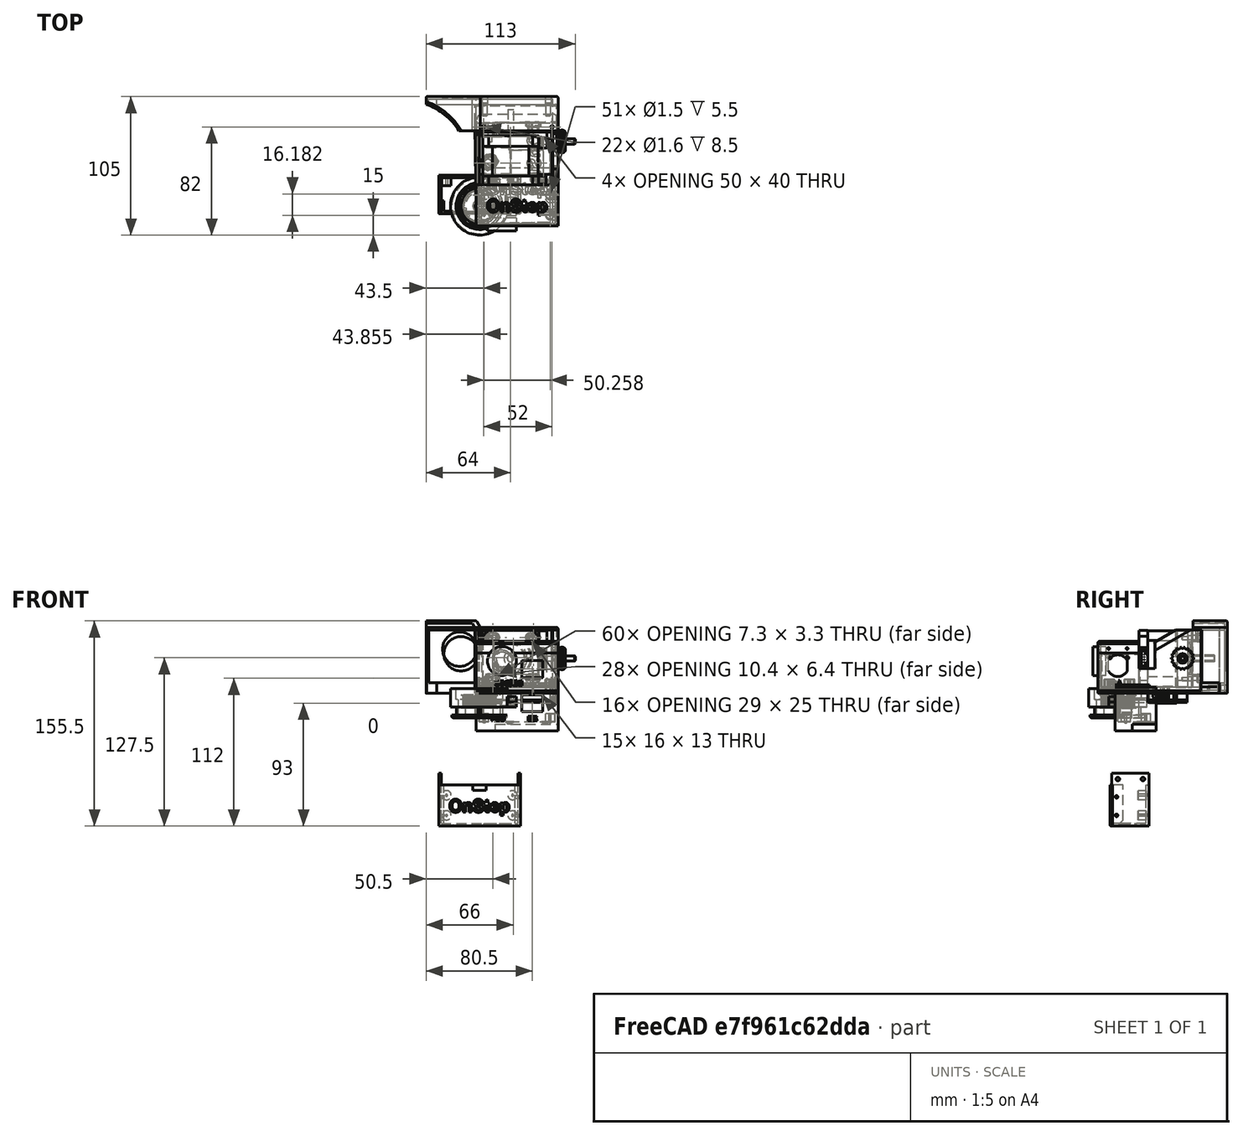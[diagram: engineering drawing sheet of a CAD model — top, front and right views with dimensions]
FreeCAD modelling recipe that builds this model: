
FCSTD DOCUMENT  (FreeCAD 0.20R29177 (Git))
Label: OnStep for EQ5
License: All rights reserved
LicenseURL: http://en.wikipedia.org/wiki/All_rights_reserved
objects: Part::Cylinder×304, Part::Box×205, Part::MultiFuse×163, Part::Cut×72, Part::Feature×53, Part::FeaturePython×28, Part::Part2DObjectPython×22, Part::Extrusion×22, Part::Fillet×14, App::Part×6, Mesh::Feature×4, Part::Chamfer×1
note: 884 computed .brp shape members not serialized (recipe doc carries the construction recipe); baked Part::Feature solids carry a one-line shape summary decoded from their .brp

FEATURE [Part::Part2DObjectPython] ShapeString016  # Draft 2D object (typed FeaturePython)
  FontFile = <path>
  Placement = pos=(15.3452,-2,30.5072) rot=(1,0,0;1.5708rad)
  Size = 0.01
  String = .
  Tracking = 0
FEATURE [Part::Part2DObjectPython] ShapeString013  # Draft 2D object (typed FeaturePython)
  FontFile = <path>
  Placement = pos=(15.3452,-2,30.5072) rot=(1,0,0;1.5708rad)
  Size = 10
  String = OnStep
  Tracking = 0
FEATURE [Part::Part2DObjectPython] ShapeString017  # Draft 2D object (typed FeaturePython)
  FontFile = <path>
  Placement = pos=(15.3452,-2,30.5072) rot=(1,0,0;1.5708rad)
  Size = 4
  String = DEC
  Tracking = 0
FEATURE [Part::Cylinder] Cylinder014005703  label="Válec620"
  Angle = 360
  AttacherType = Attacher::AttachEngine3D
  FirstAngle = 0
  Height = 70
  Placement = pos=(-5,6,16.5) rot=(0,1,0;1.5708rad)
  Radius = 1
  SecondAngle = 0
FEATURE [Part::Box] Box159  label="Krychle136"
  AttacherType = Attacher::AttachEngine3D
  Height = 2
  Length = 62
  Placement = pos=(-2.5,-2,23) rot=(0,0,1;0rad)
  Width = 31
FEATURE [Part::Box] Box161  label="Krychle138"
  AttacherType = Attacher::AttachEngine3D
  Height = 8
  Length = 58
  Placement = pos=(-0.5,0,15) rot=(0,0,1;0rad)
  Width = 29
FEATURE [Part::MultiFuse] Fusion001071
  Shapes = -> [Box159,Box161]
FEATURE [Part::Box] Box158  label="Krychle135"
  AttacherType = Attacher::AttachEngine3D
  Height = 4
  Length = 10
  Placement = pos=(-5,-8,-55) rot=(0,0,1;0rad)
  Width = 5
FEATURE [Part::Extrusion] Extrude071  label="OnStep005"
  Base = -> ShapeString013
  Dir = (0,-1,0)
  DirMode = 2
  FaceMakerClass = Part::FaceMakerBullseye
  LengthFwd = 1
  LengthRev = 0
  Placement = pos=(-10,-22,22) rot=(-1,0,0;1.5708rad)
  Solid = false
  Symmetric = false
FEATURE [Part::Cylinder] Cylinder014005704  label="Válec621"
  Angle = 360
  AttacherType = Attacher::AttachEngine3D
  FirstAngle = 0
  Height = 70
  Placement = pos=(-5,20,16.5) rot=(0,1,0;1.5708rad)
  Radius = 1
  SecondAngle = 0
FEATURE [Part::MultiFuse] Fusion001073  label="Horni diry009"
  Placement = pos=(0,0,3) rot=(0,0,1;0rad)
  Shapes = -> [Cylinder014005704,Cylinder014005703]
FEATURE [Part::Box] Box160  label="Krychle137"
  AttacherType = Attacher::AttachEngine3D
  Height = 8
  Length = 54
  Placement = pos=(1.5,0,15) rot=(0,0,1;0rad)
  Width = 29
FEATURE [Part::MultiFuse] Fusion001072
  Shapes = -> [Fusion001073,Box160]
FEATURE [Part::Cut] Cut061098066
  Base = -> Fusion001071
  Tool = -> Fusion001072
FEATURE [Part::Cut] Cut061098067  label="viko s texty005"
  Base = -> Cut061098066
  Tool = -> Extrude071
FEATURE [Part::Chamfer] Chamfer008017
  Base = -> Cut061098067
  Edges = 2 edges r=2.5: [Edge355,Edge357]
FEATURE [Part::Fillet] Fillet009  label="DEC vicko003"
  Base = -> Chamfer008017
  Edges = 3 edges r=1: [Edge36,Edge38,Edge39]
  Placement = pos=(-28.5,19,-80) rot=(1,0,0;1.5708rad)
FEATURE [Part::Cut] Cut061098065  label="DEC PCB Cap"
  Base = -> Fillet009
  Tool = -> Box158
FEATURE [Part::Extrusion] Extrude086  label="Text RA002"
  Base = -> ShapeString017
  Dir = (0,-1,0)
  DirMode = 2
  FaceMakerClass = Part::FaceMakerBullseye
  LengthFwd = 1
  LengthRev = 0
  Placement = pos=(18,0.5,-33) rot=(0,0,1;0rad)
  Solid = false
  Symmetric = false
FEATURE [Part::Cylinder] Cylinder014005791  label="Válec704"
  Angle = 360
  AttacherType = Attacher::AttachEngine3D
  FirstAngle = 0
  Height = 70
  Placement = pos=(-5,6,16.5) rot=(0,1,0;1.5708rad)
  Radius = 1
  SecondAngle = 0
FEATURE [Part::Cylinder] Cylinder014005799  label="Válec712"
  Angle = 360
  AttacherType = Attacher::AttachEngine3D
  FirstAngle = 0
  Height = 70
  Placement = pos=(-5,20,16.5) rot=(0,1,0;1.5708rad)
  Radius = 1
  SecondAngle = 0
FEATURE [Part::Cylinder] Cylinder014005792  label="Válec705"
  Angle = 360
  AttacherType = Attacher::AttachEngine3D
  FirstAngle = 0
  Height = 8
  Placement = pos=(53.5,21.25,0) rot=(0,0,1;0rad)
  Radius = 0.75
  SecondAngle = 0
FEATURE [Part::Cylinder] Cylinder014005795  label="Válec708"
  Angle = 360
  AttacherType = Attacher::AttachEngine3D
  FirstAngle = 0
  Height = 6.5
  Placement = pos=(53.5,6,0) rot=(0,0,1;0rad)
  Radius = 3.5
  SecondAngle = 0
FEATURE [Part::Box] Box203  label="Krychle178"
  AttacherType = Attacher::AttachEngine3D
  Height = 13
  Length = 2
  Placement = pos=(-31,-4.5,-55) rot=(0,0,1;0rad)
  Width = 28
FEATURE [Part::Cylinder] Cylinder014005796  label="Válec709"
  Angle = 360
  AttacherType = Attacher::AttachEngine3D
  FirstAngle = 0
  Height = 8
  Placement = pos=(53.5,6,0) rot=(0,0,1;0rad)
  Radius = 0.75
  SecondAngle = 0
FEATURE [Part::Box] Box202  label="Krychle177"
  AttacherType = Attacher::AttachEngine3D
  Height = 13
  Length = 2
  Placement = pos=(29,-4.5,-55) rot=(0,0,1;0rad)
  Width = 28
FEATURE [Part::Box] Box201  label="RJ056"
  AttacherType = Attacher::AttachEngine3D
  Height = 13
  Length = 16
  Placement = pos=(32,-5,4.5) rot=(0,0,1;0rad)
  Width = 18.5
FEATURE [Part::Cylinder] Cylinder014005793  label="Válec706"
  Angle = 360
  AttacherType = Attacher::AttachEngine3D
  FirstAngle = 0
  Height = 6.5
  Placement = pos=(3.5,21.25,0) rot=(0,0,1;0rad)
  Radius = 3.5
  SecondAngle = 0
FEATURE [Part::Cylinder] Cylinder014005802  label="Válec715"
  Angle = 360
  AttacherType = Attacher::AttachEngine3D
  FirstAngle = 0
  Height = 74
  Placement = pos=(-40,19,-46.5) rot=(0,1,0;1.5708rad)
  Radius = 1.4
  SecondAngle = 0
FEATURE [Part::Box] Box204  label="Krychle179"
  AttacherType = Attacher::AttachEngine3D
  Height = 28
  Length = 62
  Placement = pos=(-2.5,-2,-5) rot=(0,0,1;0rad)
  Width = 31
FEATURE [Part::Box] Box200  label="Krychle176"
  AttacherType = Attacher::AttachEngine3D
  Height = 26
  Length = 58
  Placement = pos=(-0.5,0,-3) rot=(0,0,1;0rad)
  Width = 29
FEATURE [Part::Cut] Cut061098120  label="Základ002"
  Base = -> Box204
  Tool = -> Box200
FEATURE [Part::Extrusion] Extrude087  label="Text TR002"
  Base = -> ShapeString016
  Dir = (0,-1,0)
  DirMode = 2
  FaceMakerClass = Part::FaceMakerBullseye
  LengthFwd = 1
  LengthRev = 0
  Placement = pos=(-6.75,0.5,-33) rot=(0,0,1;0rad)
  Solid = false
  Symmetric = false
FEATURE [Part::Cylinder] Cylinder014005800  label="Válec713"
  Angle = 360
  AttacherType = Attacher::AttachEngine3D
  FirstAngle = 0
  Height = 8
  Placement = pos=(3.5,21.25,0) rot=(0,0,1;0rad)
  Radius = 0.75
  SecondAngle = 0
FEATURE [Part::Cylinder] Cylinder014005801  label="Válec714"
  Angle = 360
  AttacherType = Attacher::AttachEngine3D
  FirstAngle = 0
  Height = 5
  Placement = pos=(14.25,1,9.5) rot=(1,0,0;1.5708rad)
  Radius = 0.01
  SecondAngle = 0
FEATURE [Part::Cylinder] Cylinder014005803  label="Válec716"
  Angle = 360
  AttacherType = Attacher::AttachEngine3D
  FirstAngle = 0
  Height = 74
  Placement = pos=(-40,0,-46.5) rot=(0,1,0;1.5708rad)
  Radius = 1.4
  SecondAngle = 0
FEATURE [Part::Cylinder] Cylinder014005797  label="Válec710"
  Angle = 360
  AttacherType = Attacher::AttachEngine3D
  FirstAngle = 0
  Height = 6.5
  Placement = pos=(53.5,21.25,0) rot=(0,0,1;0rad)
  Radius = 3.5
  SecondAngle = 0
FEATURE [Part::Cylinder] Cylinder014005798  label="Válec711"
  Angle = 360
  AttacherType = Attacher::AttachEngine3D
  FirstAngle = 0
  Height = 8
  Placement = pos=(3.5,6,0) rot=(0,0,1;0rad)
  Radius = 0.7
  SecondAngle = 0
FEATURE [Part::Cylinder] Cylinder014005794  label="Válec707"
  Angle = 360
  AttacherType = Attacher::AttachEngine3D
  FirstAngle = 0
  Height = 6.5
  Placement = pos=(3.5,6,0) rot=(0,0,1;0rad)
  Radius = 3.5
  SecondAngle = 0
FEATURE [Part::MultiFuse] Fusion001089071  label="Horni diry011"
  Placement = pos=(0,0,3) rot=(0,0,1;0rad)
  Shapes = -> [Cylinder014005799,Cylinder014005791]
FEATURE [Part::MultiFuse] Fusion001089075
  Shapes = -> [Extrude087,Extrude086]
FEATURE [Part::MultiFuse] Fusion001089077
  Shapes = -> [Box202,Box203]
FEATURE [Part::MultiFuse] Fusion001089068  label="diry017"
  Placement = pos=(0,0,-4) rot=(0,0,1;0rad)
  Shapes = -> [Cylinder014005800,Cylinder014005798,Cylinder014005792,Cylinder014005796]
FEATURE [Part::MultiFuse] Fusion001089070  label="RJ a LED002"
  Shapes = -> [Box201,Cylinder014005801]
FEATURE [Part::MultiFuse] Fusion001089072  label="sloupky005"
  Placement = pos=(0,0,-3.5) rot=(0,0,1;0rad)
  Shapes = -> [Cylinder014005793,Cylinder014005794,Cylinder014005797,Cylinder014005795]
FEATURE [Part::MultiFuse] Fusion001089073
  Shapes = -> [Cylinder014005803,Cylinder014005802]
FEATURE [Part::MultiFuse] Fusion001089074  label="bez der002"
  Shapes = -> [Cut061098120,Fusion001089072]
FEATURE [Part::MultiFuse] Fusion001089069
  Shapes = -> [Fusion001089068,Fusion001089070,Fusion001089071]
FEATURE [Part::Cut] Cut061098121
  Base = -> Fusion001089074
  Tool = -> Fusion001089069
FEATURE [Part::Cut] Cut061098118
  Base = -> Cut061098121
  Placement = pos=(-28.5,18.5,-80) rot=(1,0,0;1.5708rad)
  Tool = -> Fusion001089075
FEATURE [Part::MultiFuse] Fusion001089076  label="RA pcb box002"
  Shapes = -> [Cut061098118,Fusion001089077]
FEATURE [Part::Cut] Cut061098119  label="DEC PCB BOX For MiniPCB2"
  Base = -> Fusion001089076
  Tool = -> Fusion001089073
FEATURE [Part::Feature] Cut061098127012  label="DE 012"
  shape: bbox 62 x 31 x 33 mm, 80 faces (baked)
FEATURE [Part::Fillet] Fillet004005002  label="DE final"
  Base = -> Cut061098127012
  Edges = 5 edges r=1: [Edge94,Edge95,Edge96,Edge97,Edge98]
FEATURE [Part::Feature] Cut005023015002001  label="RA PCB003"
  shape: bbox 62 x 31 x 33 mm, 145 faces (baked)
FEATURE [App::Part] Part
  Group = -> [Fusion001089075,Fusion001089068,Fusion001089076,Fusion001089077,Fusion001089070,Fusion001089074,Fusion001089069,Fusion001089071,Fusion001089072,Fusion001089073,Cut061098118,Cut061098121,Cut061098120,Cylinder014005802,Box201,Cylinder014005803,Cylinder014005799,Cylinder014005795,Box202,Cylinder014005793,Box203,Extrude086,Cylinder014005791,Box200,Cylinder014005800,Cylinder014005797,Cylinder014005794,+28 more]
  Origin = -> Origin
FEATURE [Mesh::Feature] support_nema17_EQ5_A_D__v1_1  label="support_nema17_EQ5_A.D._v1.1"
FEATURE [Mesh::Feature] support_nema17_EQ5_Dec_v1_1  label="support_nema17_EQ5_Dec_v1.1"
  Placement = pos=(-2,-2,13) rot=(0,0,1;0rad)
FEATURE [Mesh::Feature] holderDEC
  Placement = pos=(0,0,6) rot=(0,0,1;0rad)
FEATURE [Mesh::Feature] holderRA
FEATURE [Part::Feature] Pocket004
  Placement = pos=(22.5,32.5,13.5) rot=(0,0,1;1.5708rad)
  shape: bbox 61 x 74.5 x 11 mm, 39 faces (baked)
FEATURE [Part::Box] Box  label="Krychle"
  AttacherType = Attacher::AttachEngine3D
  Height = 43
  Length = 59.5
  Placement = pos=(0,56,23) rot=(0,0,1;0rad)
  Width = 7
FEATURE [Part::Box] Box205  label="Krychle180"
  AttacherType = Attacher::AttachEngine3D
  Height = 43
  Length = 43
  Placement = pos=(2,53,23) rot=(0,0,1;0rad)
  Width = 3
FEATURE [Part::Cylinder] Cylinder014005804  label="Válec717"
  Angle = 360
  AttacherType = Attacher::AttachEngine3D
  FirstAngle = 0
  Height = 10
  Placement = pos=(8,57,29.5) rot=(1,0,0;1.5708rad)
  Radius = 1.65
  SecondAngle = 0
FEATURE [Part::Cylinder] Cylinder014005805  label="Válec718"
  Angle = 360
  AttacherType = Attacher::AttachEngine3D
  FirstAngle = 0
  Height = 10
  Placement = pos=(39,57,60.5) rot=(1,0,0;1.5708rad)
  Radius = 1.65
  SecondAngle = 0
FEATURE [Part::Cylinder] Cylinder014005806  label="Válec719"
  Angle = 360
  AttacherType = Attacher::AttachEngine3D
  FirstAngle = 0
  Height = 10
  Placement = pos=(39,57,29.5) rot=(1,0,0;1.5708rad)
  Radius = 1.65
  SecondAngle = 0
FEATURE [Part::Cylinder] Cylinder014005807  label="Válec720"
  Angle = 360
  AttacherType = Attacher::AttachEngine3D
  FirstAngle = 0
  Height = 10
  Placement = pos=(8,57,60.5) rot=(1,0,0;1.5708rad)
  Radius = 1.65
  SecondAngle = 0
FEATURE [Part::Cylinder] Cylinder014005808  label="Válec721"
  Angle = 360
  AttacherType = Attacher::AttachEngine3D
  FirstAngle = 0
  Height = 10
  Placement = pos=(23.5,59,45) rot=(1,0,0;1.5708rad)
  Radius = 12.5
  SecondAngle = 0
FEATURE [Part::Box] Box206  label="Krychle181"
  AttacherType = Attacher::AttachEngine3D
  Height = 43
  Length = 6
  Placement = pos=(45,44,23) rot=(0,0,1;0rad)
  Width = 12
FEATURE [Part::FeaturePython] Screw010  label="M4x25-Screw001"  # Fasteners workbench fastener (typed FeaturePython)
  Placement = pos=(47.5,49,45) rot=(0,-1,0;1.5708rad)
  diameter = 6
  invert = false
  length = 0
  matchOuter = false
  offset = 0
  thread = false
  type = 13
FEATURE [Part::MultiFuse] Fusion  label="diry jezdec"
  Shapes = -> [Cylinder014005804,Cylinder014005808,Cylinder014005807,Cylinder014005806,Cylinder014005805,Screw010]
FEATURE [Part::MultiFuse] Fusion001089078
  Shapes = -> [Box205,Box206]
FEATURE [Part::Cut] Cut  label="Jezdec"
  Base = -> Fusion001089078
  Tool = -> Fusion
FEATURE [Part::Cylinder] Cylinder014005809  label="Válec722"
  Angle = 360
  AttacherType = Attacher::AttachEngine3D
  FirstAngle = 0
  Height = 20
  Placement = pos=(23.5,64,45) rot=(1,0,0;1.5708rad)
  Radius = 12.5
  SecondAngle = 0
FEATURE [Part::Cylinder] Cylinder014005810  label="Válec723"
  Angle = 360
  AttacherType = Attacher::AttachEngine3D
  FirstAngle = 0
  Height = 10
  Placement = pos=(8,64,29.5) rot=(1,0,0;1.5708rad)
  Radius = 1.65
  SecondAngle = 0
FEATURE [Part::Cylinder] Cylinder014005811  label="Válec724"
  Angle = 360
  AttacherType = Attacher::AttachEngine3D
  FirstAngle = 0
  Height = 10
  Placement = pos=(8,64,60.5) rot=(1,0,0;1.5708rad)
  Radius = 1.65
  SecondAngle = 0
FEATURE [Part::Cylinder] Cylinder014005812  label="Válec725"
  Angle = 360
  AttacherType = Attacher::AttachEngine3D
  FirstAngle = 0
  Height = 10
  Placement = pos=(39,64,29.5) rot=(1,0,0;1.5708rad)
  Radius = 1.65
  SecondAngle = 0
FEATURE [Part::Cylinder] Cylinder014005813  label="Válec726"
  Angle = 360
  AttacherType = Attacher::AttachEngine3D
  FirstAngle = 0
  Height = 10
  Placement = pos=(39,64,60.5) rot=(1,0,0;1.5708rad)
  Radius = 1.65
  SecondAngle = 0
FEATURE [Part::FeaturePython] Screw011  label="M4x25-Screw002"  # Fasteners workbench fastener (typed FeaturePython)
  Placement = pos=(47.5,49,45) rot=(0,-1,0;1.5708rad)
  diameter = 6
  invert = false
  length = 0
  matchOuter = false
  offset = 0
  thread = false
  type = 13
FEATURE [Part::Box] Box207  label="Krychle182"
  AttacherType = Attacher::AttachEngine3D
  Height = 43
  Length = 4
  Placement = pos=(55.5,16,23) rot=(0,0,1;0rad)
  Width = 40
FEATURE [Part::Cylinder] Cylinder014005814  label="Válec727"
  Angle = 360
  AttacherType = Attacher::AttachEngine3D
  FirstAngle = 0
  Height = 10
  Placement = pos=(8,64,29.5) rot=(1,0,0;1.5708rad)
  Radius = 1.65
  SecondAngle = 0
FEATURE [Part::Cylinder] Cylinder014005815  label="Válec728"
  Angle = 360
  AttacherType = Attacher::AttachEngine3D
  FirstAngle = 0
  Height = 20
  Placement = pos=(23.5,64,45) rot=(1,0,0;1.5708rad)
  Radius = 12.5
  SecondAngle = 0
FEATURE [Part::Cylinder] Cylinder014005816  label="Válec729"
  Angle = 360
  AttacherType = Attacher::AttachEngine3D
  FirstAngle = 0
  Height = 10
  Placement = pos=(8,64,60.5) rot=(1,0,0;1.5708rad)
  Radius = 1.65
  SecondAngle = 0
FEATURE [Part::Cylinder] Cylinder014005817  label="Válec730"
  Angle = 360
  AttacherType = Attacher::AttachEngine3D
  FirstAngle = 0
  Height = 10
  Placement = pos=(39,64,29.5) rot=(1,0,0;1.5708rad)
  Radius = 1.65
  SecondAngle = 0
FEATURE [Part::Cylinder] Cylinder014005818  label="Válec731"
  Angle = 360
  AttacherType = Attacher::AttachEngine3D
  FirstAngle = 0
  Height = 10
  Placement = pos=(39,64,60.5) rot=(1,0,0;1.5708rad)
  Radius = 1.65
  SecondAngle = 0
FEATURE [Part::MultiFuse] Fusion001089080
  Placement = pos=(4,0,0) rot=(0,0,1;0rad)
  Shapes = -> [Cylinder014005814,Cylinder014005816,Cylinder014005818,Cylinder014005815,Cylinder014005817]
FEATURE [Part::Box] Box208  label="Krychle183"
  AttacherType = Attacher::AttachEngine3D
  Height = 25
  Length = 4
  Placement = pos=(23.5,56,32.5) rot=(0,0,1;0rad)
  Width = 8
FEATURE [Part::Box] Box209  label="Krychle184"
  AttacherType = Attacher::AttachEngine3D
  Height = 3.3
  Length = 4
  Placement = pos=(8,56,27.85) rot=(0,0,1;0rad)
  Width = 8
FEATURE [Part::Box] Box210  label="Krychle185"
  AttacherType = Attacher::AttachEngine3D
  Height = 3.3
  Length = 4
  Placement = pos=(39,56,58.85) rot=(0,0,1;0rad)
  Width = 8
FEATURE [Part::Box] Box211  label="Krychle186"
  AttacherType = Attacher::AttachEngine3D
  Height = 3.3
  Length = 4
  Placement = pos=(39,56,27.85) rot=(0,0,1;0rad)
  Width = 8
FEATURE [Part::Box] Box212  label="Krychle187"
  AttacherType = Attacher::AttachEngine3D
  Height = 3.3
  Length = 4
  Placement = pos=(8,56,58.85) rot=(0,0,1;0rad)
  Width = 8
FEATURE [Part::MultiFuse] Fusion001089081  label="Main"
  Placement = pos=(0,0,0.5) rot=(0,0,1;0rad)
  Shapes = -> [Box,Box207]
FEATURE [Part::Box] Box213  label="konektor"
  AttacherType = Attacher::AttachEngine3D
  Height = 29
  Length = 10
  Placement = pos=(50,16,37) rot=(0,0,1;0rad)
  Width = 12
FEATURE [Part::Box] Box214  label="Krychle188"
  AttacherType = Attacher::AttachEngine3D
  Height = 43
  Length = 4
  Placement = pos=(55.5,22,47) rot=(1,0,0;0.523599rad)
  Width = 40
FEATURE [Part::MultiFuse] Fusion001089079  label="diry"
  Placement = pos=(0,0,0.5) rot=(0,0,1;0rad)
  Shapes = -> [Cylinder014005810,Cylinder014005809,Cylinder014005811,Cylinder014005812,Cylinder014005813,Screw011,Fusion001089080,Box208,Box209,Box210,Box211,Box212,Box213,Box214]
FEATURE [Part::Cut] Cut005023015002002  label="RA"
  Base = -> Fusion001089081
  Tool = -> Fusion001089079
FEATURE [Part::Part2DObjectPython] ShapeString015  # Draft 2D object (typed FeaturePython)
  FontFile = <path>
  Placement = pos=(15.3452,-2,30.5072) rot=(1,0,0;1.5708rad)
  Size = 0.01
  String = .
  Tracking = 0
FEATURE [Part::Part2DObjectPython] ShapeString014  # Draft 2D object (typed FeaturePython)
  FontFile = <path>
  Placement = pos=(15.3452,-2,30.5072) rot=(1,0,0;1.5708rad)
  Size = 4
  String = RA
  Tracking = 0
FEATURE [Part::Cylinder] Cylinder014005783  label="Válec696"
  Angle = 360
  AttacherType = Attacher::AttachEngine3D
  FirstAngle = 0
  Height = 70
  Placement = pos=(-5,20,16.5) rot=(0,1,0;1.5708rad)
  Radius = 1
  SecondAngle = 0
FEATURE [Part::Extrusion] Extrude084  label="Text RA001"
  Base = -> ShapeString014
  Dir = (0,-1,0)
  DirMode = 2
  FaceMakerClass = Part::FaceMakerBullseye
  LengthFwd = 1
  LengthRev = 0
  Placement = pos=(4,0.7,-23.5) rot=(0,0,1;0rad)
  Solid = false
  Symmetric = false
FEATURE [Part::Cylinder] Cylinder014005778  label="Válec691"
  Angle = 360
  AttacherType = Attacher::AttachEngine3D
  FirstAngle = 0
  Height = 8
  Placement = pos=(3.5,6,0) rot=(0,0,1;0rad)
  Radius = 0.7
  SecondAngle = 0
FEATURE [Part::Cylinder] Cylinder014005779  label="Válec692"
  Angle = 360
  AttacherType = Attacher::AttachEngine3D
  FirstAngle = 0
  Height = 8
  Placement = pos=(53.5,21.25,0) rot=(0,0,1;0rad)
  Radius = 0.75
  SecondAngle = 0
FEATURE [Part::Cylinder] Cylinder014005780  label="Válec693"
  Angle = 360
  AttacherType = Attacher::AttachEngine3D
  FirstAngle = 0
  Height = 6.5
  Placement = pos=(3.5,6,0) rot=(0,0,1;0rad)
  Radius = 3.5
  SecondAngle = 0
FEATURE [Part::Box] Box195  label="Krychle172"
  AttacherType = Attacher::AttachEngine3D
  Height = 26
  Length = 58
  Placement = pos=(-0.5,0,-3) rot=(0,0,1;0rad)
  Width = 29
FEATURE [Part::Cylinder] Cylinder014005781  label="Válec694"
  Angle = 360
  AttacherType = Attacher::AttachEngine3D
  FirstAngle = 0
  Height = 6.5
  Placement = pos=(53.5,21.25,0) rot=(0,0,1;0rad)
  Radius = 3.5
  SecondAngle = 0
FEATURE [Part::Cylinder] Cylinder014005782  label="Válec695"
  Angle = 360
  AttacherType = Attacher::AttachEngine3D
  FirstAngle = 0
  Height = 8
  Placement = pos=(53.5,6,0) rot=(0,0,1;0rad)
  Radius = 0.75
  SecondAngle = 0
FEATURE [Part::Cylinder] Cylinder014005784  label="Válec697"
  Angle = 360
  AttacherType = Attacher::AttachEngine3D
  FirstAngle = 0
  Height = 70
  Placement = pos=(-5,6,16.5) rot=(0,1,0;1.5708rad)
  Radius = 1
  SecondAngle = 0
FEATURE [Part::Box] Box196  label="RJ055"
  AttacherType = Attacher::AttachEngine3D
  Height = 13
  Length = 16
  Placement = pos=(32,-5,4.5) rot=(0,0,1;0rad)
  Width = 18.5
FEATURE [Part::Cylinder] Cylinder014005786  label="Válec699"
  Angle = 360
  AttacherType = Attacher::AttachEngine3D
  FirstAngle = 0
  Height = 8
  Placement = pos=(3.5,21.25,0) rot=(0,0,1;0rad)
  Radius = 0.75
  SecondAngle = 0
FEATURE [Part::Cylinder] Cylinder014005787  label="Válec700"
  Angle = 360
  AttacherType = Attacher::AttachEngine3D
  FirstAngle = 0
  Height = 6.5
  Placement = pos=(3.5,21.25,0) rot=(0,0,1;0rad)
  Radius = 3.5
  SecondAngle = 0
FEATURE [Part::Cylinder] Cylinder014005785  label="Válec698"
  Angle = 360
  AttacherType = Attacher::AttachEngine3D
  FirstAngle = 0
  Height = 5
  Placement = pos=(14.25,1,9.5) rot=(1,0,0;1.5708rad)
  Radius = 0.01
  SecondAngle = 0
FEATURE [Part::Cylinder] Cylinder014005788  label="Válec701"
  Angle = 360
  AttacherType = Attacher::AttachEngine3D
  FirstAngle = 0
  Height = 6.5
  Placement = pos=(53.5,6,0) rot=(0,0,1;0rad)
  Radius = 3.5
  SecondAngle = 0
FEATURE [Part::Box] Box199  label="Krychle175"
  AttacherType = Attacher::AttachEngine3D
  Height = 28
  Length = 62
  Placement = pos=(-2.5,-2,-5) rot=(0,0,1;0rad)
  Width = 31
FEATURE [Part::Cut] Cut061098114  label="Základ001"
  Base = -> Box199
  Tool = -> Box195
FEATURE [Part::Extrusion] Extrude085  label="Text TR001"
  Base = -> ShapeString015
  Dir = (0,-1,0)
  DirMode = 2
  FaceMakerClass = Part::FaceMakerBullseye
  LengthFwd = 1
  LengthRev = 0
  Placement = pos=(-6.75,1,-33) rot=(0,0,1;0rad)
  Solid = false
  Symmetric = false
FEATURE [Part::MultiFuse] Fusion001089063
  Shapes = -> [Extrude085,Extrude084]
FEATURE [Part::MultiFuse] Fusion001089058  label="RJ a LED001"
  Shapes = -> [Box196,Cylinder014005785]
FEATURE [Part::MultiFuse] Fusion001089059  label="Horni diry010"
  Placement = pos=(0,0,3) rot=(0,0,1;0rad)
  Shapes = -> [Cylinder014005783,Cylinder014005784]
FEATURE [Part::MultiFuse] Fusion001089060  label="diry016"
  Placement = pos=(0,0,-4) rot=(0,0,1;0rad)
  Shapes = -> [Cylinder014005786,Cylinder014005778,Cylinder014005779,Cylinder014005782]
FEATURE [Part::MultiFuse] Fusion001089062
  Shapes = -> [Fusion001089060,Fusion001089058,Fusion001089059]
FEATURE [Part::MultiFuse] Fusion001089061  label="sloupky004"
  Placement = pos=(0,0,-3.5) rot=(0,0,1;0rad)
  Shapes = -> [Cylinder014005787,Cylinder014005780,Cylinder014005781,Cylinder014005788]
FEATURE [Part::MultiFuse] Fusion001089067  label="bez der001"
  Shapes = -> [Cut061098114,Fusion001089061]
FEATURE [Part::Cut] Cut061098117
  Base = -> Fusion001089067
  Tool = -> Fusion001089062
FEATURE [Part::Cut] Cut061098115  label="PCB"
  Base = -> Cut061098117
  Placement = pos=(0,-13,26) rot=(1,0,0;0rad)
  Tool = -> Fusion001089063
FEATURE [Part::Box] Box215  label="Krychle189"
  AttacherType = Attacher::AttachEngine3D
  Height = 3
  Length = 62
  Placement = pos=(-2.5,-15,20.5) rot=(0,0,1;0rad)
  Width = 78
FEATURE [Part::Box] Box216  label="Krychle190"
  AttacherType = Attacher::AttachEngine3D
  Height = 8
  Length = 24
  Placement = pos=(-1.5,12.5,13.5) rot=(0,0,1;0rad)
  Width = 40
FEATURE [Part::Box] Box217  label="Krychle191"
  AttacherType = Attacher::AttachEngine3D
  Height = 8
  Length = 26
  Placement = pos=(22.5,22.5,13.5) rot=(0,0,1;0rad)
  Width = 20
FEATURE [Part::Box] Box218  label="Krychle192"
  AttacherType = Attacher::AttachEngine3D
  Height = 8
  Length = 6
  Placement = pos=(53.5,22.5,13.5) rot=(0,0,1;0rad)
  Width = 20
FEATURE [Part::MultiFuse] Fusion001089082  label="spodek"
  Shapes = -> [Box215,Box218,Box216,Box217]
FEATURE [Part::FeaturePython] Screw  label="M6x12-Screw"  # Fasteners workbench fastener (typed FeaturePython)
  Placement = pos=(6.5,32.5,19.5) rot=(1,0,0;0rad)
  diameter = 8
  invert = false
  length = 0
  matchOuter = false
  offset = 0
  thread = false
  type = 14
FEATURE [Part::Cylinder] Cylinder  label="Válec"
  Angle = 360
  AttacherType = Attacher::AttachEngine3D
  FirstAngle = 0
  Height = 10
  Placement = pos=(52,28,16.5) rot=(0,1,0;1.5708rad)
  Radius = 1.65
  SecondAngle = 0
FEATURE [Part::Cylinder] Cylinder014005819  label="Válec732"
  Angle = 360
  AttacherType = Attacher::AttachEngine3D
  FirstAngle = 0
  Height = 10
  Placement = pos=(52,37,16.5) rot=(0,1,0;1.5708rad)
  Radius = 1.65
  SecondAngle = 0
FEATURE [Part::Box] Box219  label="Krychle193"
  AttacherType = Attacher::AttachEngine3D
  Height = 3.3
  Length = 10
  Placement = pos=(52,28,14.85) rot=(0,0,1;0rad)
  Width = 9
FEATURE [Part::MultiFuse] Fusion001089083  label="Diryspodek"
  Shapes = -> [Box219,Cylinder,Cylinder014005819,Screw]
FEATURE [Part::Cut] Cut005023015002003  label="Spodek"
  Base = -> Fusion001089082
  Tool = -> Fusion001089083
FEATURE [Part::MultiFuse] Fusion001089084
  Shapes = -> [Cut061098115,Cut005023015002003,Cut005023015002002]
FEATURE [Part::FeaturePython] Screw012  label="M4x25-Screw003"  # Fasteners workbench fastener (typed FeaturePython)
  Placement = pos=(47.5,49,45) rot=(0,-1,0;1.5708rad)
  diameter = 6
  invert = false
  length = 0
  matchOuter = false
  offset = 0
  thread = false
  type = 13
FEATURE [Part::FeaturePython] Screw013  label="M6x12-Screw001"  # Fasteners workbench fastener (typed FeaturePython)
  Placement = pos=(8.5,34,19.5) rot=(1,0,0;0rad)
  diameter = 8
  invert = false
  length = 0
  matchOuter = false
  offset = 0
  thread = false
  type = 14
FEATURE [Part::Cylinder] Cylinder014005820  label="Válec733"
  Angle = 360
  AttacherType = Attacher::AttachEngine3D
  FirstAngle = 0
  Height = 10
  Placement = pos=(8,64,60.5) rot=(1,0,0;1.5708rad)
  Radius = 1.65
  SecondAngle = 0
FEATURE [Part::Cylinder] Cylinder014005821  label="Válec734"
  Angle = 360
  AttacherType = Attacher::AttachEngine3D
  FirstAngle = 0
  Height = 10
  Placement = pos=(39,64,29.5) rot=(1,0,0;1.5708rad)
  Radius = 1.65
  SecondAngle = 0
FEATURE [Part::Cylinder] Cylinder014005822  label="Válec735"
  Angle = 360
  AttacherType = Attacher::AttachEngine3D
  FirstAngle = 0
  Height = 10
  Placement = pos=(8,64,60.5) rot=(1,0,0;1.5708rad)
  Radius = 1.65
  SecondAngle = 0
FEATURE [Part::Cylinder] Cylinder014005823  label="Válec736"
  Angle = 360
  AttacherType = Attacher::AttachEngine3D
  FirstAngle = 0
  Height = 10
  Placement = pos=(8,64,29.5) rot=(1,0,0;1.5708rad)
  Radius = 1.65
  SecondAngle = 0
FEATURE [Part::Cylinder] Cylinder014005824  label="Válec737"
  Angle = 360
  AttacherType = Attacher::AttachEngine3D
  FirstAngle = 0
  Height = 10
  Placement = pos=(39,64,29.5) rot=(1,0,0;1.5708rad)
  Radius = 1.65
  SecondAngle = 0
FEATURE [Part::Box] Box220  label="Krychle194"
  AttacherType = Attacher::AttachEngine3D
  Height = 43
  Length = 59.5
  Placement = pos=(0,56,23) rot=(0,0,1;0rad)
  Width = 7
FEATURE [Part::Box] Box221  label="Krychle195"
  AttacherType = Attacher::AttachEngine3D
  Height = 43
  Length = 4
  Placement = pos=(55.5,16,23) rot=(0,0,1;0rad)
  Width = 40
FEATURE [Part::Cylinder] Cylinder014005825  label="Válec738"
  Angle = 360
  AttacherType = Attacher::AttachEngine3D
  FirstAngle = 0
  Height = 20
  Placement = pos=(23.5,64,45) rot=(1,0,0;1.5708rad)
  Radius = 12.5
  SecondAngle = 0
FEATURE [Part::Cylinder] Cylinder014005826  label="Válec739"
  Angle = 360
  AttacherType = Attacher::AttachEngine3D
  FirstAngle = 0
  Height = 10
  Placement = pos=(39,64,60.5) rot=(1,0,0;1.5708rad)
  Radius = 1.65
  SecondAngle = 0
FEATURE [Part::Cylinder] Cylinder014005827  label="Válec740"
  Angle = 360
  AttacherType = Attacher::AttachEngine3D
  FirstAngle = 0
  Height = 10
  Placement = pos=(8,64,29.5) rot=(1,0,0;1.5708rad)
  Radius = 1.65
  SecondAngle = 0
FEATURE [Part::Cylinder] Cylinder014005828  label="Válec741"
  Angle = 360
  AttacherType = Attacher::AttachEngine3D
  FirstAngle = 0
  Height = 20
  Placement = pos=(23.5,64,45) rot=(1,0,0;1.5708rad)
  Radius = 12.5
  SecondAngle = 0
FEATURE [Part::MultiFuse] Fusion001089085  label="Main001"
  Placement = pos=(0,0,0.5) rot=(0,0,1;0rad)
  Shapes = -> [Box220,Box221]
FEATURE [Part::Cylinder] Cylinder014005829  label="Válec742"
  Angle = 360
  AttacherType = Attacher::AttachEngine3D
  FirstAngle = 0
  Height = 10
  Placement = pos=(39,64,60.5) rot=(1,0,0;1.5708rad)
  Radius = 1.65
  SecondAngle = 0
FEATURE [Part::MultiFuse] Fusion001089090
  Placement = pos=(4,0,0) rot=(0,0,1;0rad)
  Shapes = -> [Cylinder014005827,Cylinder014005820,Cylinder014005829,Cylinder014005828,Cylinder014005821]
FEATURE [Part::Box] Box224  label="Krychle198"
  AttacherType = Attacher::AttachEngine3D
  Height = 9
  Length = 26
  Placement = pos=(-2,24,13) rot=(0,0,1;0rad)
  Width = 20
FEATURE [Part::Box] Box225  label="Krychle199"
  AttacherType = Attacher::AttachEngine3D
  Height = 25
  Length = 4
  Placement = pos=(23.5,56,32.5) rot=(0,0,1;0rad)
  Width = 8
FEATURE [Part::Box] Box226  label="Krychle200"
  AttacherType = Attacher::AttachEngine3D
  Height = 3.3
  Length = 4
  Placement = pos=(39,56,58.85) rot=(0,0,1;0rad)
  Width = 8
FEATURE [Part::Box] Box227  label="Krychle201"
  AttacherType = Attacher::AttachEngine3D
  Height = 43
  Length = 4
  Placement = pos=(55.5,22,47) rot=(1,0,0;0.523599rad)
  Width = 40
FEATURE [Part::Box] Box228  label="konektor001"
  AttacherType = Attacher::AttachEngine3D
  Height = 29
  Length = 10
  Placement = pos=(50,16,37) rot=(0,0,1;0rad)
  Width = 12
FEATURE [Part::Box] Box229  label="Krychle202"
  AttacherType = Attacher::AttachEngine3D
  Height = 3.3
  Length = 4
  Placement = pos=(39,56,27.85) rot=(0,0,1;0rad)
  Width = 8
FEATURE [Part::Box] Box230  label="Krychle203"
  AttacherType = Attacher::AttachEngine3D
  Height = 3.3
  Length = 4
  Placement = pos=(8,56,27.85) rot=(0,0,1;0rad)
  Width = 8
FEATURE [Part::Box] Box232  label="Krychle204"
  AttacherType = Attacher::AttachEngine3D
  Height = 3
  Length = 62
  Placement = pos=(-2.5,-15,20.5) rot=(0,0,1;0rad)
  Width = 78
FEATURE [Part::MultiFuse] Fusion001089088  label="spodek001"
  Shapes = -> [Box232,Box224]
FEATURE [Part::Box] Box233  label="Krychle205"
  AttacherType = Attacher::AttachEngine3D
  Height = 3.3
  Length = 4
  Placement = pos=(8,56,58.85) rot=(0,0,1;0rad)
  Width = 8
FEATURE [Part::MultiFuse] Fusion001089091  label="diry018"
  Placement = pos=(0,0,0.5) rot=(0,0,1;0rad)
  Shapes = -> [Cylinder014005823,Cylinder014005825,Cylinder014005822,Cylinder014005824,Cylinder014005826,Screw012,Fusion001089090,Box225,Box230,Box226,Box229,Box233,Box228,Box227]
FEATURE [Part::Cut] Cut005023015002008  label="DEC"
  Base = -> Fusion001089085
  Tool = -> Fusion001089091
FEATURE [Part::Cut] Cut005023015002009  label="dec spodek"
  Base = -> Fusion001089088
  Tool = -> Screw013
FEATURE [Part::Part2DObjectPython] ShapeString018  # Draft 2D object (typed FeaturePython)
  FontFile = <path>
  Placement = pos=(15.3452,-2,30.5072) rot=(1,0,0;1.5708rad)
  Size = 4
  String = DEC
  Tracking = 0
FEATURE [Part::Part2DObjectPython] ShapeString019  # Draft 2D object (typed FeaturePython)
  FontFile = <path>
  Placement = pos=(15.3452,-2,30.5072) rot=(1,0,0;1.5708rad)
  Size = 0.01
  String = .
  Tracking = 0
FEATURE [Part::Box] Box234  label="Krychle206"
  AttacherType = Attacher::AttachEngine3D
  Height = 26
  Length = 58
  Placement = pos=(-0.5,0,-3) rot=(0,0,1;0rad)
  Width = 29
FEATURE [Part::Box] Box235  label="Krychle207"
  AttacherType = Attacher::AttachEngine3D
  Height = 28
  Length = 62
  Placement = pos=(-2.5,-2,-5) rot=(0,0,1;0rad)
  Width = 31
FEATURE [Part::Cut] Cut005023015002010  label="Základ003"
  Base = -> Box235
  Tool = -> Box234
FEATURE [Part::Cylinder] Cylinder014005830  label="Válec743"
  Angle = 360
  AttacherType = Attacher::AttachEngine3D
  FirstAngle = 0
  Height = 70
  Placement = pos=(-5,20,16.5) rot=(0,1,0;1.5708rad)
  Radius = 1
  SecondAngle = 0
FEATURE [Part::Extrusion] Extrude088  label="Text TR003"
  Base = -> ShapeString019
  Dir = (0,-1,0)
  DirMode = 2
  FaceMakerClass = Part::FaceMakerBullseye
  LengthFwd = 1
  LengthRev = 0
  Placement = pos=(-6.75,0.5,-33) rot=(0,0,1;0rad)
  Solid = false
  Symmetric = false
FEATURE [Part::Cylinder] Cylinder014005831  label="Válec744"
  Angle = 360
  AttacherType = Attacher::AttachEngine3D
  FirstAngle = 0
  Height = 8
  Placement = pos=(3.5,6,0) rot=(0,0,1;0rad)
  Radius = 0.7
  SecondAngle = 0
FEATURE [Part::Cylinder] Cylinder014005832  label="Válec745"
  Angle = 360
  AttacherType = Attacher::AttachEngine3D
  FirstAngle = 0
  Height = 8
  Placement = pos=(53.5,21.25,0) rot=(0,0,1;0rad)
  Radius = 0.75
  SecondAngle = 0
FEATURE [Part::Cylinder] Cylinder014005833  label="Válec746"
  Angle = 360
  AttacherType = Attacher::AttachEngine3D
  FirstAngle = 0
  Height = 6.5
  Placement = pos=(3.5,6,0) rot=(0,0,1;0rad)
  Radius = 3.5
  SecondAngle = 0
FEATURE [Part::Cylinder] Cylinder014005834  label="Válec747"
  Angle = 360
  AttacherType = Attacher::AttachEngine3D
  FirstAngle = 0
  Height = 6.5
  Placement = pos=(53.5,21.25,0) rot=(0,0,1;0rad)
  Radius = 3.5
  SecondAngle = 0
FEATURE [Part::Cylinder] Cylinder014005835  label="Válec748"
  Angle = 360
  AttacherType = Attacher::AttachEngine3D
  FirstAngle = 0
  Height = 8
  Placement = pos=(53.5,6,0) rot=(0,0,1;0rad)
  Radius = 0.75
  SecondAngle = 0
FEATURE [Part::Cylinder] Cylinder014005836  label="Válec749"
  Angle = 360
  AttacherType = Attacher::AttachEngine3D
  FirstAngle = 0
  Height = 70
  Placement = pos=(-5,6,16.5) rot=(0,1,0;1.5708rad)
  Radius = 1
  SecondAngle = 0
FEATURE [Part::MultiFuse] Fusion001089097  label="Horni diry012"
  Placement = pos=(0,0,3) rot=(0,0,1;0rad)
  Shapes = -> [Cylinder014005830,Cylinder014005836]
FEATURE [Part::Extrusion] Extrude089  label="Text RA003"
  Base = -> ShapeString018
  Dir = (0,-1,0)
  DirMode = 2
  FaceMakerClass = Part::FaceMakerBullseye
  LengthFwd = 1
  LengthRev = 0
  Placement = pos=(40,1,43.5) rot=(0,1,0;3.14159rad)
  Solid = false
  Symmetric = false
FEATURE [Part::MultiFuse] Fusion001089095
  Shapes = -> [Extrude088,Extrude089]
FEATURE [Part::Box] Box236  label="RJ057"
  AttacherType = Attacher::AttachEngine3D
  Height = 13
  Length = 16
  Placement = pos=(32,-5,4.5) rot=(0,0,1;0rad)
  Width = 18.5
FEATURE [Part::Cylinder] Cylinder014005837  label="Válec750"
  Angle = 360
  AttacherType = Attacher::AttachEngine3D
  FirstAngle = 0
  Height = 8
  Placement = pos=(3.5,21.25,0) rot=(0,0,1;0rad)
  Radius = 0.75
  SecondAngle = 0
FEATURE [Part::MultiFuse] Fusion001089098  label="diry019"
  Placement = pos=(0,0,-4) rot=(0,0,1;0rad)
  Shapes = -> [Cylinder014005837,Cylinder014005831,Cylinder014005832,Cylinder014005835]
FEATURE [Part::Cylinder] Cylinder014005838  label="Válec751"
  Angle = 360
  AttacherType = Attacher::AttachEngine3D
  FirstAngle = 0
  Height = 6.5
  Placement = pos=(3.5,21.25,0) rot=(0,0,1;0rad)
  Radius = 3.5
  SecondAngle = 0
FEATURE [Part::Cylinder] Cylinder014005839  label="Válec752"
  Angle = 360
  AttacherType = Attacher::AttachEngine3D
  FirstAngle = 0
  Height = 5
  Placement = pos=(14.25,1,9.5) rot=(1,0,0;1.5708rad)
  Radius = 0.01
  SecondAngle = 0
FEATURE [Part::MultiFuse] Fusion001089096  label="RJ a LED003"
  Shapes = -> [Box236,Cylinder014005839]
FEATURE [Part::MultiFuse] Fusion001089092
  Shapes = -> [Fusion001089098,Fusion001089096,Fusion001089097]
FEATURE [Part::Cylinder] Cylinder014005840  label="Válec753"
  Angle = 360
  AttacherType = Attacher::AttachEngine3D
  FirstAngle = 0
  Height = 6.5
  Placement = pos=(53.5,6,0) rot=(0,0,1;0rad)
  Radius = 3.5
  SecondAngle = 0
FEATURE [Part::MultiFuse] Fusion001089093  label="sloupky006"
  Placement = pos=(0,0,-3.5) rot=(0,0,1;0rad)
  Shapes = -> [Cylinder014005838,Cylinder014005833,Cylinder014005834,Cylinder014005840]
FEATURE [Part::MultiFuse] Fusion001089094  label="bez der003"
  Shapes = -> [Cut005023015002010,Fusion001089093]
FEATURE [Part::Cut] Cut005023015002011
  Base = -> Fusion001089094
  Tool = -> Fusion001089092
FEATURE [Part::Cut] Cut005023015002012  label="PCB001"
  Base = -> Cut005023015002011
  Placement = pos=(0,-13,26) rot=(1,0,0;0rad)
  Tool = -> Fusion001089095
FEATURE [Part::MultiFuse] Fusion001089099  label="Dec-fin"
  Shapes = -> [Cut005023015002012,Cut005023015002008,Cut005023015002009]
FEATURE [Part::Fillet] Fillet  label="RAv1"
  Base = -> Fusion001089084
  Edges = 2 edges r=2: [Edge279,Edge287]
FEATURE [Part::Part2DObjectPython] ShapeString020  # Draft 2D object (typed FeaturePython)
  FontFile = <path>
  Placement = pos=(15.3452,-2,30.5072) rot=(1,0,0;1.5708rad)
  Size = 0.01
  String = .
  Tracking = 0
FEATURE [Part::Extrusion] Extrude091  label="Text TR004"
  Base = -> ShapeString020
  Dir = (0,-1,0)
  DirMode = 2
  FaceMakerClass = Part::FaceMakerBullseye
  LengthFwd = 1
  LengthRev = 0
  Placement = pos=(-6.75,1,-33) rot=(0,0,1;0rad)
  Solid = false
  Symmetric = false
FEATURE [Part::Box] Box237  label="Krychle208"
  AttacherType = Attacher::AttachEngine3D
  Height = 43
  Length = 59.5
  Placement = pos=(0,56,23) rot=(0,0,1;0rad)
  Width = 7
FEATURE [Part::FeaturePython] Screw014  label="M6x12-Screw002"  # Fasteners workbench fastener (typed FeaturePython)
  Placement = pos=(6.5,32.5,20.5) rot=(1,0,0;0rad)
  diameter = 8
  invert = false
  length = 0
  matchOuter = false
  offset = 0
  thread = false
  type = 14
FEATURE [Part::FeaturePython] Screw015  label="M4x25-Screw004"  # Fasteners workbench fastener (typed FeaturePython)
  Placement = pos=(47.5,49,45) rot=(0,-1,0;1.5708rad)
  diameter = 6
  invert = false
  length = 0
  matchOuter = false
  offset = 0
  thread = false
  type = 13
FEATURE [Part::Part2DObjectPython] ShapeString021  # Draft 2D object (typed FeaturePython)
  FontFile = <path>
  Placement = pos=(15.3452,-2,30.5072) rot=(1,0,0;1.5708rad)
  Size = 4
  String = RA
  Tracking = 0
FEATURE [Part::Extrusion] Extrude090  label="Text RA004"
  Base = -> ShapeString021
  Dir = (0,-1,0)
  DirMode = 2
  FaceMakerClass = Part::FaceMakerBullseye
  LengthFwd = 1
  LengthRev = 0
  Placement = pos=(4,0.7,-23.5) rot=(0,0,1;0rad)
  Solid = false
  Symmetric = false
FEATURE [Part::MultiFuse] Fusion001089103
  Shapes = -> [Extrude091,Extrude090]
FEATURE [Part::Box] Box238  label="Krychle209"
  AttacherType = Attacher::AttachEngine3D
  Height = 3.3
  Length = 4
  Placement = pos=(39,56,58.85) rot=(0,0,1;0rad)
  Width = 8
FEATURE [Part::Cylinder] Cylinder014005841  label="Válec754"
  Angle = 360
  AttacherType = Attacher::AttachEngine3D
  FirstAngle = 0
  Height = 6.5
  Placement = pos=(53.5,21.25,0) rot=(0,0,1;0rad)
  Radius = 3.5
  SecondAngle = 0
FEATURE [Part::Cylinder] Cylinder014005842  label="Válec755"
  Angle = 360
  AttacherType = Attacher::AttachEngine3D
  FirstAngle = 0
  Height = 10
  Placement = pos=(8,64,60.5) rot=(1,0,0;1.5708rad)
  Radius = 1.65
  SecondAngle = 0
FEATURE [Part::Cylinder] Cylinder014005843  label="Válec756"
  Angle = 360
  AttacherType = Attacher::AttachEngine3D
  FirstAngle = 0
  Height = 20
  Placement = pos=(23.5,64,45) rot=(1,0,0;1.5708rad)
  Radius = 12.5
  SecondAngle = 0
FEATURE [Part::Box] Box239  label="konektor002"
  AttacherType = Attacher::AttachEngine3D
  Height = 29
  Length = 10
  Placement = pos=(50,16,37) rot=(0,0,1;0rad)
  Width = 12
FEATURE [Part::Box] Box240  label="Krychle210"
  AttacherType = Attacher::AttachEngine3D
  Height = 43
  Length = 65
  Placement = pos=(-5,15.5,49.5) rot=(1,0,0;0.523599rad)
  Width = 48
FEATURE [Part::Cylinder] Cylinder014005844  label="Válec757"
  Angle = 360
  AttacherType = Attacher::AttachEngine3D
  FirstAngle = 0
  Height = 10
  Placement = pos=(8,64,29.5) rot=(1,0,0;1.5708rad)
  Radius = 1.65
  SecondAngle = 0
FEATURE [Part::Cylinder] Cylinder014005845  label="Válec758"
  Angle = 360
  AttacherType = Attacher::AttachEngine3D
  FirstAngle = 0
  Height = 10
  Placement = pos=(39,64,29.5) rot=(1,0,0;1.5708rad)
  Radius = 1.65
  SecondAngle = 0
FEATURE [Part::Box] Box241  label="Krychle211"
  AttacherType = Attacher::AttachEngine3D
  Height = 43
  Length = 4
  Placement = pos=(55.5,16,23) rot=(0,0,1;0rad)
  Width = 40
FEATURE [Part::Cylinder] Cylinder014005846  label="Válec759"
  Angle = 360
  AttacherType = Attacher::AttachEngine3D
  FirstAngle = 0
  Height = 10
  Placement = pos=(8,64,29.5) rot=(1,0,0;1.5708rad)
  Radius = 1.65
  SecondAngle = 0
FEATURE [Part::Cylinder] Cylinder014005847  label="Válec760"
  Angle = 360
  AttacherType = Attacher::AttachEngine3D
  FirstAngle = 0
  Height = 8
  Placement = pos=(3.5,6,0) rot=(0,0,1;0rad)
  Radius = 0.7
  SecondAngle = 0
FEATURE [Part::Box] Box242  label="Krychle212"
  AttacherType = Attacher::AttachEngine3D
  Height = 3.3
  Length = 4
  Placement = pos=(8,56,58.85) rot=(0,0,1;0rad)
  Width = 8
FEATURE [Part::Cylinder] Cylinder014005848  label="Válec761"
  Angle = 360
  AttacherType = Attacher::AttachEngine3D
  FirstAngle = 0
  Height = 10
  Placement = pos=(8,64,60.5) rot=(1,0,0;1.5708rad)
  Radius = 1.65
  SecondAngle = 0
FEATURE [Part::Box] Box243  label="Krychle213"
  AttacherType = Attacher::AttachEngine3D
  Height = 3.3
  Length = 4
  Placement = pos=(39,56,27.85) rot=(0,0,1;0rad)
  Width = 8
FEATURE [Part::Cylinder] Cylinder014005849  label="Válec762"
  Angle = 360
  AttacherType = Attacher::AttachEngine3D
  FirstAngle = 0
  Height = 20
  Placement = pos=(23.5,64,45) rot=(1,0,0;1.5708rad)
  Radius = 12.5
  SecondAngle = 0
FEATURE [Part::Cylinder] Cylinder014005850  label="Válec763"
  Angle = 360
  AttacherType = Attacher::AttachEngine3D
  FirstAngle = 0
  Height = 10
  Placement = pos=(39,64,29.5) rot=(1,0,0;1.5708rad)
  Radius = 1.65
  SecondAngle = 0
FEATURE [Part::Box] Box244  label="Krychle214"
  AttacherType = Attacher::AttachEngine3D
  Height = 3.3
  Length = 4
  Placement = pos=(8,56,27.85) rot=(0,0,1;0rad)
  Width = 8
FEATURE [Part::Cylinder] Cylinder014005851  label="Válec764"
  Angle = 360
  AttacherType = Attacher::AttachEngine3D
  FirstAngle = 0
  Height = 70
  Placement = pos=(-5,20,16.5) rot=(0,1,0;1.5708rad)
  Radius = 1
  SecondAngle = 0
FEATURE [Part::Cylinder] Cylinder014005852  label="Válec765"
  Angle = 360
  AttacherType = Attacher::AttachEngine3D
  FirstAngle = 0
  Height = 10
  Placement = pos=(39,64,60.5) rot=(1,0,0;1.5708rad)
  Radius = 1.65
  SecondAngle = 0
FEATURE [Part::Box] Box245  label="Krychle215"
  AttacherType = Attacher::AttachEngine3D
  Height = 25
  Length = 4
  Placement = pos=(23.5,56,32.5) rot=(0,0,1;0rad)
  Width = 8
FEATURE [Part::Cylinder] Cylinder014005853  label="Válec766"
  Angle = 360
  AttacherType = Attacher::AttachEngine3D
  FirstAngle = 0
  Height = 8
  Placement = pos=(53.5,21.25,0) rot=(0,0,1;0rad)
  Radius = 0.75
  SecondAngle = 0
FEATURE [Part::Cylinder] Cylinder014005854  label="Válec767"
  Angle = 360
  AttacherType = Attacher::AttachEngine3D
  FirstAngle = 0
  Height = 10
  Placement = pos=(39,64,60.5) rot=(1,0,0;1.5708rad)
  Radius = 1.65
  SecondAngle = 0
FEATURE [Part::MultiFuse] Fusion001089102
  Placement = pos=(4,0,0) rot=(0,0,1;0rad)
  Shapes = -> [Cylinder014005846,Cylinder014005842,Cylinder014005854,Cylinder014005843,Cylinder014005850]
FEATURE [Part::Box] Box246  label="Krychle216"
  AttacherType = Attacher::AttachEngine3D
  Height = 26
  Length = 58
  Placement = pos=(-0.5,0,-3) rot=(0,0,1;0rad)
  Width = 29
FEATURE [Part::Cylinder] Cylinder014005855  label="Válec768"
  Angle = 360
  AttacherType = Attacher::AttachEngine3D
  FirstAngle = 0
  Height = 6.5
  Placement = pos=(3.5,6,0) rot=(0,0,1;0rad)
  Radius = 3.5
  SecondAngle = 0
FEATURE [Part::Box] Box247  label="Krychle217"
  AttacherType = Attacher::AttachEngine3D
  Height = 28
  Length = 62
  Placement = pos=(-2.5,-2,-5) rot=(0,0,1;0rad)
  Width = 31
FEATURE [Part::Cut] Cut005023015002016  label="Základ004"
  Base = -> Box247
  Tool = -> Box246
FEATURE [Part::Box] Box248  label="Krychle218"
  AttacherType = Attacher::AttachEngine3D
  Height = 8
  Length = 26
  Placement = pos=(22.5,22.5,13.5) rot=(0,0,1;0rad)
  Width = 20
FEATURE [Part::Cylinder] Cylinder014005856  label="Válec769"
  Angle = 360
  AttacherType = Attacher::AttachEngine3D
  FirstAngle = 0
  Height = 6.5
  Placement = pos=(53.5,6,0) rot=(0,0,1;0rad)
  Radius = 3.5
  SecondAngle = 0
FEATURE [Part::Box] Box249  label="Krychle219"
  AttacherType = Attacher::AttachEngine3D
  Height = 8
  Length = 24
  Placement = pos=(-1.5,12.5,13.5) rot=(0,0,1;0rad)
  Width = 40
FEATURE [Part::Cylinder] Cylinder014005857  label="Válec770"
  Angle = 360
  AttacherType = Attacher::AttachEngine3D
  FirstAngle = 0
  Height = 8
  Placement = pos=(3.5,21.25,0) rot=(0,0,1;0rad)
  Radius = 0.75
  SecondAngle = 0
FEATURE [Part::Cylinder] Cylinder014005858  label="Válec771"
  Angle = 360
  AttacherType = Attacher::AttachEngine3D
  FirstAngle = 0
  Height = 70
  Placement = pos=(-5,6,16.5) rot=(0,1,0;1.5708rad)
  Radius = 1
  SecondAngle = 0
FEATURE [Part::MultiFuse] Fusion001089104  label="Horni diry013"
  Placement = pos=(0,0,3) rot=(0,0,1;0rad)
  Shapes = -> [Cylinder014005851,Cylinder014005858]
FEATURE [Part::Box] Box250  label="RJ058"
  AttacherType = Attacher::AttachEngine3D
  Height = 13
  Length = 16
  Placement = pos=(32,-5,4.5) rot=(0,0,1;0rad)
  Width = 18.5
FEATURE [Part::Cylinder] Cylinder014005859  label="Válec772"
  Angle = 360
  AttacherType = Attacher::AttachEngine3D
  FirstAngle = 0
  Height = 6.5
  Placement = pos=(3.5,21.25,0) rot=(0,0,1;0rad)
  Radius = 3.5
  SecondAngle = 0
FEATURE [Part::MultiFuse] Fusion001089108  label="sloupky007"
  Placement = pos=(0,0,-3.5) rot=(0,0,1;0rad)
  Shapes = -> [Cylinder014005859,Cylinder014005855,Cylinder014005841,Cylinder014005856]
FEATURE [Part::MultiFuse] Fusion001089107  label="bez der004"
  Shapes = -> [Cut005023015002016,Fusion001089108]
FEATURE [Part::Box] Box251  label="Krychle220"
  AttacherType = Attacher::AttachEngine3D
  Height = 5
  Length = 62
  Placement = pos=(-2.5,-15,20.5) rot=(0,0,1;0rad)
  Width = 92
FEATURE [Part::Cylinder] Cylinder014005860  label="Válec773"
  Angle = 360
  AttacherType = Attacher::AttachEngine3D
  FirstAngle = 0
  Height = 8
  Placement = pos=(53.5,6,0) rot=(0,0,1;0rad)
  Radius = 0.75
  SecondAngle = 0
FEATURE [Part::MultiFuse] Fusion001089106  label="diry021"
  Placement = pos=(0,0,-4) rot=(0,0,1;0rad)
  Shapes = -> [Cylinder014005857,Cylinder014005847,Cylinder014005853,Cylinder014005860]
FEATURE [Part::Cylinder] Cylinder014005861  label="Válec774"
  Angle = 360
  AttacherType = Attacher::AttachEngine3D
  FirstAngle = 0
  Height = 5
  Placement = pos=(14.25,1,9.5) rot=(1,0,0;1.5708rad)
  Radius = 0.01
  SecondAngle = 0
FEATURE [Part::MultiFuse] Fusion001089100  label="RJ a LED004"
  Shapes = -> [Box250,Cylinder014005861]
FEATURE [Part::MultiFuse] Fusion001089111
  Shapes = -> [Fusion001089106,Fusion001089100,Fusion001089104]
FEATURE [Part::Cut] Cut005023015002017
  Base = -> Fusion001089107
  Tool = -> Fusion001089111
FEATURE [Part::Cut] Cut005023015002013  label="PCB002"
  Base = -> Cut005023015002017
  Placement = pos=(0,-13,26) rot=(1,0,0;0rad)
  Tool = -> Fusion001089103
FEATURE [Part::Box] Box252  label="Krychle221"
  AttacherType = Attacher::AttachEngine3D
  Height = 3.3
  Length = 10
  Placement = pos=(52,31,14.85) rot=(0,0,1;0rad)
  Width = 6
FEATURE [Part::Cylinder] Cylinder014005862  label="Válec775"
  Angle = 360
  AttacherType = Attacher::AttachEngine3D
  FirstAngle = 0
  Height = 10
  Placement = pos=(52,37,16.5) rot=(0,1,0;1.5708rad)
  Radius = 1.65
  SecondAngle = 0
FEATURE [Part::Box] Box253  label="Krychle222"
  AttacherType = Attacher::AttachEngine3D
  Height = 8
  Length = 6
  Placement = pos=(53.5,22.5,13.5) rot=(0,0,1;0rad)
  Width = 20
FEATURE [Part::MultiFuse] Fusion001089109  label="spodek002"
  Shapes = -> [Box251,Box253,Box249,Box248]
FEATURE [Part::Cylinder] Cylinder014005863  label="Válec776"
  Angle = 360
  AttacherType = Attacher::AttachEngine3D
  FirstAngle = 0
  Height = 10
  Placement = pos=(52,31,16.5) rot=(0,1,0;1.5708rad)
  Radius = 1.65
  SecondAngle = 0
FEATURE [Part::FeaturePython] Screw016  label="M6x12-Screw003"  # Fasteners workbench fastener (typed FeaturePython)
  Placement = pos=(6.5,32.5,21.5) rot=(1,0,0;0rad)
  diameter = 8
  invert = false
  length = 0
  matchOuter = false
  offset = 0
  thread = false
  type = 14
FEATURE [Part::MultiFuse] Fusion001089101  label="Diryspodek001"
  Shapes = -> [Box252,Cylinder014005863,Cylinder014005862,Screw014,Screw016]
FEATURE [Part::Cut] Cut005023015002014  label="Spodek001"
  Base = -> Fusion001089109
  Placement = pos=(0,0,-2) rot=(0,0,1;0rad)
  Tool = -> Fusion001089101
FEATURE [Part::Box] Box254  label="Krychle223"
  AttacherType = Attacher::AttachEngine3D
  Height = 43
  Length = 2.5
  Placement = pos=(-2.5,16,23) rot=(0,0,1;0rad)
  Width = 47
FEATURE [Part::MultiFuse] Fusion001089112  label="Main002"
  Placement = pos=(0,0,0.5) rot=(0,0,1;0rad)
  Shapes = -> [Box237,Box241,Box254]
FEATURE [Part::Cylinder] Cylinder014005864  label="Válec777"
  Angle = 360
  AttacherType = Attacher::AttachEngine3D
  FirstAngle = 0
  Height = 3
  Placement = pos=(12,63,29.5) rot=(1,0,0;1.5708rad)
  Radius = 3.2
  SecondAngle = 0
FEATURE [Part::Cylinder] Cylinder014005865  label="Válec778"
  Angle = 360
  AttacherType = Attacher::AttachEngine3D
  FirstAngle = 0
  Height = 3
  Placement = pos=(8,63,29.5) rot=(1,0,0;1.5708rad)
  Radius = 3.2
  SecondAngle = 0
FEATURE [Part::Box] Box255  label="Krychle224"
  AttacherType = Attacher::AttachEngine3D
  Height = 6.4
  Length = 4
  Placement = pos=(8,60,26.3) rot=(0,0,1;0rad)
  Width = 3
FEATURE [Part::MultiFuse] Fusion001089113  label="Imbus"
  Shapes = -> [Cylinder014005864,Cylinder014005865,Box255]
FEATURE [Part::Feature] Fusion001089113001  label="Imbus001"
  Placement = pos=(31,0,0) rot=(0,0,1;0rad)
  shape: bbox 10.4 x 3 x 6.4 mm, 6 faces (baked)
FEATURE [Part::Feature] Fusion001089113002  label="Imbus002"
  Placement = pos=(31,0,31) rot=(0,0,1;0rad)
  shape: bbox 10.4 x 3 x 6.4 mm, 6 faces (baked)
FEATURE [Part::Feature] Fusion001089113003  label="Imbus003"
  Placement = pos=(0,0,31) rot=(0,0,1;0rad)
  shape: bbox 10.4 x 3 x 6.4 mm, 6 faces (baked)
FEATURE [Part::MultiFuse] Fusion001089105  label="diry020"
  Placement = pos=(0,0,0.5) rot=(0,0,1;0rad)
  Shapes = -> [Cylinder014005844,Cylinder014005849,Cylinder014005848,Cylinder014005845,Cylinder014005852,Screw015,Fusion001089102,Box245,Box244,Box238,Box243,Box242,Box239,Box240,Fusion001089113,Fusion001089113001,Fusion001089113002,Fusion001089113003]
FEATURE [Part::Cut] Cut005023015002015  label="RA002"
  Base = -> Fusion001089112
  Tool = -> Fusion001089105
FEATURE [Part::MultiFuse] Fusion001089110  label="Raxxx"
  Shapes = -> [Cut005023015002013,Cut005023015002014,Cut005023015002015]
FEATURE [Part::Fillet] Fillet004005003  label="RA FinV2"
  Base = -> Fusion001089110
  Edges = 12 edges: [Edge1 r=1,Edge5 r=1,Edge8 r=1,Edge13 r=1,Edge16 r=2,Edge21 r=1,Edge58 r=1,Edge59 r=1,Edge78 r=1,Edge79 r=2,Edge221 r=2,Edge229 r=2]
FEATURE [Part::Feature] Fusion001089113007  label="Motor-with-connector-final003"
  Placement = pos=(23.5,16,45) rot=(-1,0,0;1.5708rad)
  shape: bbox 48 x 60.1 x 42.3 mm, 110 faces (baked)
FEATURE [Part::Box] Box258  label="Krychle227"
  AttacherType = Attacher::AttachEngine3D
  Height = 70
  Length = 73
  Width = 19
FEATURE [Part::Cut] Cut005023015002020  label="Motor"
  Base = -> Fusion001089113007
  Placement = pos=(0,-3,0) rot=(0,0,1;0rad)
  Tool = -> Box258
FEATURE [App::Part] Part001
  Group = -> [support_nema17_EQ5_A_D__v1_1,support_nema17_EQ5_Dec_v1_1,holderDEC,holderRA,Box258,Fusion001089113007,Cut005023015002020]
  Origin = -> Origin001
FEATURE [Part::Feature] Cut005023015002020001  label="Motor001"
  shape: bbox 48 x 57.1 x 42.3 mm, 100 faces (baked)
FEATURE [Part::FeaturePython] Screw018  label="M6x12-Screw004"  # Fasteners workbench fastener (typed FeaturePython)
  Placement = pos=(8.5,34,20.5) rot=(1,0,0;0rad)
  diameter = 8
  invert = false
  length = 0
  matchOuter = false
  offset = 0
  thread = false
  type = 14
FEATURE [Part::Part2DObjectPython] ShapeString022  # Draft 2D object (typed FeaturePython)
  FontFile = <path>
  Placement = pos=(15.3452,-2,30.5072) rot=(1,0,0;1.5708rad)
  Size = 4
  String = DEC
  Tracking = 0
FEATURE [Part::Part2DObjectPython] ShapeString023  # Draft 2D object (typed FeaturePython)
  FontFile = <path>
  Placement = pos=(15.3452,-2,30.5072) rot=(1,0,0;1.5708rad)
  Size = 0.01
  String = .
  Tracking = 0
FEATURE [Part::Extrusion] Extrude092  label="Text TR005"
  Base = -> ShapeString023
  Dir = (0,-1,0)
  DirMode = 2
  FaceMakerClass = Part::FaceMakerBullseye
  LengthFwd = 1
  LengthRev = 0
  Placement = pos=(-6.75,0.5,-33) rot=(0,0,1;0rad)
  Solid = false
  Symmetric = false
FEATURE [Part::Extrusion] Extrude093  label="Text RA005"
  Base = -> ShapeString022
  Dir = (0,-1,0)
  DirMode = 2
  FaceMakerClass = Part::FaceMakerBullseye
  LengthFwd = 1
  LengthRev = 0
  Placement = pos=(40,1,43.5) rot=(0,1,0;3.14159rad)
  Solid = false
  Symmetric = false
FEATURE [Part::Cylinder] Cylinder014005873  label="Válec786"
  Angle = 360
  AttacherType = Attacher::AttachEngine3D
  FirstAngle = 0
  Height = 6.5
  Placement = pos=(53.5,21.25,0) rot=(0,0,1;0rad)
  Radius = 3.5
  SecondAngle = 0
FEATURE [Part::Cylinder] Cylinder014005874  label="Válec787"
  Angle = 360
  AttacherType = Attacher::AttachEngine3D
  FirstAngle = 0
  Height = 8
  Placement = pos=(3.5,21.25,0) rot=(0,0,1;0rad)
  Radius = 0.75
  SecondAngle = 0
FEATURE [Part::Cylinder] Cylinder014005876  label="Válec789"
  Angle = 360
  AttacherType = Attacher::AttachEngine3D
  FirstAngle = 0
  Height = 70
  Placement = pos=(-5,20,16.5) rot=(0,1,0;1.5708rad)
  Radius = 1
  SecondAngle = 0
FEATURE [Part::Box] Box263  label="Krychle232"
  AttacherType = Attacher::AttachEngine3D
  Height = 9
  Length = 26
  Placement = pos=(-2,24,13) rot=(0,0,1;0rad)
  Width = 20
FEATURE [Part::Cylinder] Cylinder014005877  label="Válec790"
  Angle = 360
  AttacherType = Attacher::AttachEngine3D
  FirstAngle = 0
  Height = 8
  Placement = pos=(53.5,21.25,0) rot=(0,0,1;0rad)
  Radius = 0.75
  SecondAngle = 0
FEATURE [Part::Box] Box264  label="RJ059"
  AttacherType = Attacher::AttachEngine3D
  Height = 13
  Length = 16
  Placement = pos=(32,-5,4.5) rot=(0,0,1;0rad)
  Width = 18.5
FEATURE [Part::Cylinder] Cylinder014005878  label="Válec791"
  Angle = 360
  AttacherType = Attacher::AttachEngine3D
  FirstAngle = 0
  Height = 8
  Placement = pos=(3.5,6,0) rot=(0,0,1;0rad)
  Radius = 0.7
  SecondAngle = 0
FEATURE [Part::Cylinder] Cylinder014005879  label="Válec792"
  Angle = 360
  AttacherType = Attacher::AttachEngine3D
  FirstAngle = 0
  Height = 6.5
  Placement = pos=(3.5,21.25,0) rot=(0,0,1;0rad)
  Radius = 3.5
  SecondAngle = 0
FEATURE [Part::Cylinder] Cylinder014005881  label="Válec794"
  Angle = 360
  AttacherType = Attacher::AttachEngine3D
  FirstAngle = 0
  Height = 8
  Placement = pos=(53.5,6,0) rot=(0,0,1;0rad)
  Radius = 0.75
  SecondAngle = 0
FEATURE [Part::Box] Box269  label="Krychle237"
  AttacherType = Attacher::AttachEngine3D
  Height = 26
  Length = 58
  Placement = pos=(-0.5,0,-3) rot=(0,0,1;0rad)
  Width = 29
FEATURE [Part::Cylinder] Cylinder014005882  label="Válec795"
  Angle = 360
  AttacherType = Attacher::AttachEngine3D
  FirstAngle = 0
  Height = 70
  Placement = pos=(-5,6,16.5) rot=(0,1,0;1.5708rad)
  Radius = 1
  SecondAngle = 0
FEATURE [Part::Box] Box271  label="Krychle238"
  AttacherType = Attacher::AttachEngine3D
  Height = 28
  Length = 62
  Placement = pos=(-2.5,-2,-5) rot=(0,0,1;0rad)
  Width = 31
FEATURE [Part::Cut] Cut005023015002020006  label="Základ005"
  Base = -> Box271
  Tool = -> Box269
FEATURE [Part::Cylinder] Cylinder014005884  label="Válec797"
  Angle = 360
  AttacherType = Attacher::AttachEngine3D
  FirstAngle = 0
  Height = 6.5
  Placement = pos=(3.5,6,0) rot=(0,0,1;0rad)
  Radius = 3.5
  SecondAngle = 0
FEATURE [Part::Box] Box272  label="Krychle239"
  AttacherType = Attacher::AttachEngine3D
  Height = 5
  Length = 62
  Placement = pos=(-2.5,-15,20.5) rot=(0,0,1;0rad)
  Width = 78
FEATURE [Part::MultiFuse] Fusion001089113009  label="spodek003"
  Shapes = -> [Box272,Box263]
FEATURE [Part::MultiFuse] Fusion001089113012  label="diry022"
  Placement = pos=(0,0,-4) rot=(0,0,1;0rad)
  Shapes = -> [Cylinder014005874,Cylinder014005878,Cylinder014005877,Cylinder014005881]
FEATURE [Part::MultiFuse] Fusion001089113015  label="Horni diry014"
  Placement = pos=(0,0,3) rot=(0,0,1;0rad)
  Shapes = -> [Cylinder014005876,Cylinder014005882]
FEATURE [Part::MultiFuse] Fusion001089113018
  Shapes = -> [Extrude092,Extrude093]
FEATURE [Part::Cylinder] Cylinder014005885  label="Válec798"
  Angle = 360
  AttacherType = Attacher::AttachEngine3D
  FirstAngle = 0
  Height = 5
  Placement = pos=(14.25,1,9.5) rot=(1,0,0;1.5708rad)
  Radius = 0.01
  SecondAngle = 0
FEATURE [Part::MultiFuse] Fusion001089113016  label="RJ a LED005"
  Shapes = -> [Box264,Cylinder014005885]
FEATURE [Part::MultiFuse] Fusion001089113017
  Shapes = -> [Fusion001089113012,Fusion001089113016,Fusion001089113015]
FEATURE [Part::Cylinder] Cylinder014005886  label="Válec799"
  Angle = 360
  AttacherType = Attacher::AttachEngine3D
  FirstAngle = 0
  Height = 6.5
  Placement = pos=(53.5,6,0) rot=(0,0,1;0rad)
  Radius = 3.5
  SecondAngle = 0
FEATURE [Part::MultiFuse] Fusion001089113014  label="sloupky008"
  Placement = pos=(0,0,-3.5) rot=(0,0,1;0rad)
  Shapes = -> [Cylinder014005879,Cylinder014005884,Cylinder014005873,Cylinder014005886]
FEATURE [Part::MultiFuse] Fusion001089113010  label="bez der005"
  Shapes = -> [Cut005023015002020006,Fusion001089113014]
FEATURE [Part::Cut] Cut005023015002020004
  Base = -> Fusion001089113010
  Tool = -> Fusion001089113017
FEATURE [Part::Cut] Cut005023015002020003  label="PCB003"
  Base = -> Cut005023015002020004
  Placement = pos=(0,-13,26) rot=(1,0,0;0rad)
  Tool = -> Fusion001089113018
FEATURE [Part::FeaturePython] Screw019  label="M4x25-Screw006"  # Fasteners workbench fastener (typed FeaturePython)
  Placement = pos=(47.5,49,45) rot=(0,-1,0;1.5708rad)
  diameter = 6
  invert = false
  length = 0
  matchOuter = false
  offset = 0
  thread = false
  type = 13
FEATURE [Part::Feature] Fusion001089113020  label="Imbus004"
  Placement = pos=(0,0,31) rot=(0,0,1;0rad)
  shape: bbox 10.4 x 3 x 6.4 mm, 6 faces (baked)
FEATURE [Part::Feature] Fusion001089113021  label="Imbus005"
  Placement = pos=(31,0,31) rot=(0,0,1;0rad)
  shape: bbox 10.4 x 3 x 6.4 mm, 6 faces (baked)
FEATURE [Part::Feature] Fusion001089113022  label="Imbus006"
  Placement = pos=(31,0,0) rot=(0,0,1;0rad)
  shape: bbox 10.4 x 3 x 6.4 mm, 6 faces (baked)
FEATURE [Part::Box] Box273  label="Krychle240"
  AttacherType = Attacher::AttachEngine3D
  Height = 43
  Length = 65
  Placement = pos=(-5,15.5,49.5) rot=(1,0,0;0.523599rad)
  Width = 48
FEATURE [Part::Cylinder] Cylinder014005887  label="Válec800"
  Angle = 360
  AttacherType = Attacher::AttachEngine3D
  FirstAngle = 0
  Height = 10
  Placement = pos=(8,64,29.5) rot=(1,0,0;1.5708rad)
  Radius = 1.65
  SecondAngle = 0
FEATURE [Part::Box] Box274  label="konektor004"
  AttacherType = Attacher::AttachEngine3D
  Height = 29
  Length = 10
  Placement = pos=(50,16,37) rot=(0,0,1;0rad)
  Width = 12
FEATURE [Part::Box] Box275  label="Krychle241"
  AttacherType = Attacher::AttachEngine3D
  Height = 43
  Length = 4
  Placement = pos=(55.5,16,23) rot=(0,0,1;0rad)
  Width = 40
FEATURE [Part::Box] Box276  label="Krychle242"
  AttacherType = Attacher::AttachEngine3D
  Height = 25
  Length = 4
  Placement = pos=(23.5,56,32.5) rot=(0,0,1;0rad)
  Width = 8
FEATURE [Part::Box] Box277  label="Krychle243"
  AttacherType = Attacher::AttachEngine3D
  Height = 3.3
  Length = 4
  Placement = pos=(8,56,27.85) rot=(0,0,1;0rad)
  Width = 8
FEATURE [Part::Cylinder] Cylinder014005888  label="Válec801"
  Angle = 360
  AttacherType = Attacher::AttachEngine3D
  FirstAngle = 0
  Height = 10
  Placement = pos=(39,64,60.5) rot=(1,0,0;1.5708rad)
  Radius = 1.65
  SecondAngle = 0
FEATURE [Part::Box] Box278  label="Krychle244"
  AttacherType = Attacher::AttachEngine3D
  Height = 43
  Length = 59.5
  Placement = pos=(0,56,23) rot=(0,0,1;0rad)
  Width = 7
FEATURE [Part::Cylinder] Cylinder014005889  label="Válec802"
  Angle = 360
  AttacherType = Attacher::AttachEngine3D
  FirstAngle = 0
  Height = 10
  Placement = pos=(8,64,60.5) rot=(1,0,0;1.5708rad)
  Radius = 1.65
  SecondAngle = 0
FEATURE [Part::Cylinder] Cylinder014005890  label="Válec803"
  Angle = 360
  AttacherType = Attacher::AttachEngine3D
  FirstAngle = 0
  Height = 20
  Placement = pos=(23.5,64,45) rot=(1,0,0;1.5708rad)
  Radius = 12.5
  SecondAngle = 0
FEATURE [Part::Cylinder] Cylinder014005891  label="Válec804"
  Angle = 360
  AttacherType = Attacher::AttachEngine3D
  FirstAngle = 0
  Height = 10
  Placement = pos=(8,64,60.5) rot=(1,0,0;1.5708rad)
  Radius = 1.65
  SecondAngle = 0
FEATURE [Part::Box] Box279  label="Krychle245"
  AttacherType = Attacher::AttachEngine3D
  Height = 3.3
  Length = 4
  Placement = pos=(8,56,58.85) rot=(0,0,1;0rad)
  Width = 8
FEATURE [Part::Box] Box280  label="Krychle246"
  AttacherType = Attacher::AttachEngine3D
  Height = 3.3
  Length = 4
  Placement = pos=(39,56,27.85) rot=(0,0,1;0rad)
  Width = 8
FEATURE [Part::Cylinder] Cylinder014005892  label="Válec805"
  Angle = 360
  AttacherType = Attacher::AttachEngine3D
  FirstAngle = 0
  Height = 10
  Placement = pos=(39,64,29.5) rot=(1,0,0;1.5708rad)
  Radius = 1.65
  SecondAngle = 0
FEATURE [Part::Cylinder] Cylinder014005893  label="Válec806"
  Angle = 360
  AttacherType = Attacher::AttachEngine3D
  FirstAngle = 0
  Height = 10
  Placement = pos=(39,64,29.5) rot=(1,0,0;1.5708rad)
  Radius = 1.65
  SecondAngle = 0
FEATURE [Part::Cylinder] Cylinder014005894  label="Válec807"
  Angle = 360
  AttacherType = Attacher::AttachEngine3D
  FirstAngle = 0
  Height = 10
  Placement = pos=(8,64,29.5) rot=(1,0,0;1.5708rad)
  Radius = 1.65
  SecondAngle = 0
FEATURE [Part::Cylinder] Cylinder014005895  label="Válec808"
  Angle = 360
  AttacherType = Attacher::AttachEngine3D
  FirstAngle = 0
  Height = 20
  Placement = pos=(23.5,64,45) rot=(1,0,0;1.5708rad)
  Radius = 12.5
  SecondAngle = 0
FEATURE [Part::Box] Box281  label="Krychle247"
  AttacherType = Attacher::AttachEngine3D
  Height = 3.3
  Length = 4
  Placement = pos=(39,56,58.85) rot=(0,0,1;0rad)
  Width = 8
FEATURE [Part::Cylinder] Cylinder014005896  label="Válec809"
  Angle = 360
  AttacherType = Attacher::AttachEngine3D
  FirstAngle = 0
  Height = 10
  Placement = pos=(39,64,60.5) rot=(1,0,0;1.5708rad)
  Radius = 1.65
  SecondAngle = 0
FEATURE [Part::MultiFuse] Fusion001089113023
  Placement = pos=(4,0,0) rot=(0,0,1;0rad)
  Shapes = -> [Cylinder014005894,Cylinder014005889,Cylinder014005896,Cylinder014005890,Cylinder014005893]
FEATURE [Part::Cylinder] Cylinder014005897  label="Válec810"
  Angle = 360
  AttacherType = Attacher::AttachEngine3D
  FirstAngle = 0
  Height = 3
  Placement = pos=(8,63,29.5) rot=(1,0,0;1.5708rad)
  Radius = 3.2
  SecondAngle = 0
FEATURE [Part::Box] Box282  label="Krychle248"
  AttacherType = Attacher::AttachEngine3D
  Height = 6.4
  Length = 4
  Placement = pos=(8,60,26.3) rot=(0,0,1;0rad)
  Width = 3
FEATURE [Part::Box] Box283  label="Krychle249"
  AttacherType = Attacher::AttachEngine3D
  Height = 43
  Length = 2.5
  Placement = pos=(-2.5,16,23) rot=(0,0,1;0rad)
  Width = 47
FEATURE [Part::MultiFuse] Fusion001089113025  label="Main004"
  Placement = pos=(0,0,0.5) rot=(0,0,1;0rad)
  Shapes = -> [Box278,Box275,Box283]
FEATURE [Part::Cylinder] Cylinder014005898  label="Válec811"
  Angle = 360
  AttacherType = Attacher::AttachEngine3D
  FirstAngle = 0
  Height = 3
  Placement = pos=(12,63,29.5) rot=(1,0,0;1.5708rad)
  Radius = 3.2
  SecondAngle = 0
FEATURE [Part::MultiFuse] Fusion001089113026  label="Imbus007"
  Shapes = -> [Cylinder014005898,Cylinder014005897,Box282]
FEATURE [Part::MultiFuse] Fusion001089113024  label="diry024"
  Placement = pos=(0,0,0.5) rot=(0,0,1;0rad)
  Shapes = -> [Cylinder014005887,Cylinder014005895,Cylinder014005891,Cylinder014005892,Cylinder014005888,Screw019,Fusion001089113023,Box276,Box277,Box281,Box280,Box279,Box274,Box273,Fusion001089113026,Fusion001089113022,Fusion001089113021,Fusion001089113020]
FEATURE [Part::Cut] Cut005023015002020007  label="DE003"
  Base = -> Fusion001089113025
  Tool = -> Fusion001089113024
FEATURE [Part::FeaturePython] Screw020  label="M6x12-Screw005"  # Fasteners workbench fastener (typed FeaturePython)
  Placement = pos=(8.5,34,21.5) rot=(1,0,0;0rad)
  diameter = 8
  invert = false
  length = 0
  matchOuter = false
  offset = 0
  thread = false
  type = 14
FEATURE [Part::MultiFuse] Fusion001089113027
  Shapes = -> [Screw020,Screw018]
FEATURE [Part::Cut] Cut005023015002020008
  Base = -> Fusion001089113009
  Placement = pos=(0,0,-2) rot=(0,0,1;0rad)
  Tool = -> Fusion001089113027
FEATURE [Part::MultiFuse] Fusion001089113028  label="DECV2"
  Shapes = -> [Cut005023015002020003,Cut005023015002020007,Cut005023015002020008]
FEATURE [Part::Fillet] Fillet004005003002  label="DEv2"
  Base = -> Fusion001089113028
  Edges = 13 edges r=1: [Edge9,Edge48,Edge101,Edge104,Edge181,Edge273,Edge274,Edge375,Edge376,Edge388,Edge389,Edge391,Edge396]
FEATURE [Part::Feature] Fillet004005003002001  label="DEv003"
  shape: bbox 62 x 78 x 55.5 mm, 180 faces (baked)
FEATURE [Part::Feature] Cut005023015002020009  label="Jezdec001"
  shape: bbox 49 x 12 x 43 mm, 24 faces (baked)
FEATURE [Part::FeaturePython] Screw021  label="M4x25-Screw007"  # Fasteners workbench fastener (typed FeaturePython)
  Placement = pos=(47.5,49,45) rot=(0,-1,0;1.5708rad)
  diameter = 6
  invert = false
  length = 0
  matchOuter = false
  offset = 0
  thread = false
  type = 13
FEATURE [Part::Feature] Fillet004005003002002  label="RA FinV003"
  shape: bbox 62 x 92 x 55 mm, 179 faces (baked)
FEATURE [Part::Part2DObjectPython] ShapeString004  # Draft 2D object (typed FeaturePython)
  FontFile = <path>
  Placement = pos=(15.3452,-2,30.5072) rot=(1,0,0;1.5708rad)
  Size = 10
  String = OnStep
  Tracking = 0
FEATURE [Part::Box] Box022  label="Krychle011"
  AttacherType = Attacher::AttachEngine3D
  Height = 2
  Length = 62
  Placement = pos=(-2.5,-2,23) rot=(0,0,1;0rad)
  Width = 26
FEATURE [Part::Box] Box023  label="Krychle012"
  AttacherType = Attacher::AttachEngine3D
  Height = 8
  Length = 58
  Placement = pos=(-0.5,0,15) rot=(0,0,1;0rad)
  Width = 23
FEATURE [Part::MultiFuse] Fusion029
  Shapes = -> [Box022,Box023]
FEATURE [Part::Box] Box024  label="Krychle013"
  AttacherType = Attacher::AttachEngine3D
  Height = 8
  Length = 54
  Placement = pos=(1.5,0,15) rot=(0,0,1;0rad)
  Width = 29
FEATURE [Part::Cylinder] Cylinder040  label="Válec039"
  Angle = 360
  AttacherType = Attacher::AttachEngine3D
  FirstAngle = 0
  Height = 70
  Placement = pos=(-5,20,16.5) rot=(0,1,0;1.5708rad)
  Radius = 1
  SecondAngle = 0
FEATURE [Part::Cylinder] Cylinder039  label="Válec038"
  Angle = 360
  AttacherType = Attacher::AttachEngine3D
  FirstAngle = 0
  Height = 70
  Placement = pos=(-5,6,16.5) rot=(0,1,0;1.5708rad)
  Radius = 1
  SecondAngle = 0
FEATURE [Part::MultiFuse] Fusion028  label="Horni diry002"
  Placement = pos=(0,0,3) rot=(0,0,1;0rad)
  Shapes = -> [Cylinder040,Cylinder039]
FEATURE [Part::MultiFuse] Fusion030
  Shapes = -> [Fusion028,Box024]
FEATURE [Part::Cut] Cut018
  Base = -> Fusion029
  Tool = -> Fusion030
FEATURE [Part::Extrusion] Extrude004  label="OnStep"
  Base = -> ShapeString004
  Dir = (0,-1,0)
  DirMode = 2
  FaceMakerClass = Part::FaceMakerBullseye
  LengthFwd = 1
  LengthRev = 0
  Placement = pos=(-10,-22,22) rot=(-1,0,0;1.5708rad)
  Solid = false
  Symmetric = false
FEATURE [Part::Cut] Cut019  label="viko s texty"
  Base = -> Cut018
  Tool = -> Extrude004
FEATURE [Part::FeaturePython] Screw009  label="M4x30-Screw003"  # Fasteners workbench fastener (typed FeaturePython)
  Placement = pos=(0,0,2.25) rot=(0,0,1;0rad)
  diameter = 6
  invert = false
  length = 1
  matchOuter = false
  offset = 0
  thread = false
  type = 13
FEATURE [Part::Feature] Cylinder112024025003003006010004077  label="Válec229"
  Placement = pos=(0,0,0) rot=(0,0,1;0.349066rad)
  shape: bbox 2 x 2 x 10 mm, 3 faces (baked)
FEATURE [Part::Feature] Fusion005043005007002046
  Placement = pos=(0,0,0) rot=(0,0,1;2.0944rad)
  shape: bbox 6.25 x 14.82 x 10 mm, 18 faces, 6 solids (baked)
FEATURE [Part::Feature] Cylinder112024025003003006010004078  label="Válec230"
  Placement = pos=(0,0,0) rot=(0,0,1;0.698132rad)
  shape: bbox 2 x 2 x 10 mm, 3 faces (baked)
FEATURE [Part::Cylinder] Cylinder112024025003003006010004076  label="Válec228"
  Angle = 360
  AttacherType = Attacher::AttachEngine3D
  FirstAngle = 0
  Height = 5
  Radius = 8.5
  SecondAngle = 0
FEATURE [Part::Cut] Cut018020020009027020002003004004023
  Base = -> Cylinder112024025003003006010004076
  Tool = -> Screw009
FEATURE [Part::Fillet] Fillet024  label="knob003"
  Base = -> Cut018020020009027020002003004004023
  Edges = 2 edges r=2: [Edge1,Edge3]
FEATURE [Part::Cylinder] Cylinder112024025003003006010004075  label="Válec227"
  Angle = 360
  AttacherType = Attacher::AttachEngine3D
  FirstAngle = 0
  Height = 10
  Placement = pos=(8.5,0,0) rot=(0,0,1;0.349066rad)
  Radius = 1
  SecondAngle = 0
FEATURE [Part::MultiFuse] Fusion005043005007002045
  Shapes = -> [Cylinder112024025003003006010004075,Cylinder112024025003003006010004077,Cylinder112024025003003006010004078]
FEATURE [Part::Feature] Fusion005043005007002048
  Placement = pos=(0,0,0) rot=(0,0,1;4.18879rad)
  shape: bbox 14.24 x 7.464 x 10 mm, 18 faces, 6 solids (baked)
FEATURE [Part::Feature] Fusion005043005007002047
  Placement = pos=(0,0,0) rot=(0,0,1;1.0472rad)
  shape: bbox 7.726 x 3.01 x 10 mm, 9 faces, 3 solids (baked)
FEATURE [Part::MultiFuse] Fusion005043005007002044
  Shapes = -> [Fusion005043005007002045,Fusion005043005007002047]
FEATURE [Part::MultiFuse] Fusion005043005007002043
  Shapes = -> [Fusion005043005007002048,Fusion005043005007002046,Fusion005043005007002044]
FEATURE [Part::Cut] Cut018020020009027020002003004004024  label="Knob M4 v003"
  Base = -> Fillet024
  Placement = pos=(60,49,45) rot=(0,1,0;1.5708rad)
  Tool = -> Fusion005043005007002043
FEATURE [Part::Cylinder] Cylinder112024025003003006010004079  label="Válec812"
  Angle = 360
  AttacherType = Attacher::AttachEngine3D
  FirstAngle = 0
  Height = 22
  Radius = 17.6
  SecondAngle = 0
FEATURE [Part::Cylinder] Cylinder112024025003003006010004080  label="Válec813"
  Angle = 360
  AttacherType = Attacher::AttachEngine3D
  FirstAngle = 0
  Height = 14
  Placement = pos=(0,0,8) rot=(0,0,1;0rad)
  Radius = 22
  SecondAngle = 0
FEATURE [Part::Cylinder] Cylinder112024025003003006010004081  label="Válec814"
  Angle = 360
  AttacherType = Attacher::AttachEngine3D
  FirstAngle = 0
  Height = 8
  Placement = pos=(0,0,14) rot=(0,0,1;0rad)
  Radius = 17.8
  SecondAngle = 0
FEATURE [Part::Cylinder] Cylinder112024025003003006010004082  label="Válec815"
  Angle = 360
  AttacherType = Attacher::AttachEngine3D
  FirstAngle = 0
  Height = 25
  Radius = 16
  SecondAngle = 0
FEATURE [Part::Cylinder] Cylinder112024025003003006010004083  label="Válec816"
  Angle = 360
  AttacherType = Attacher::AttachEngine3D
  FirstAngle = 0
  Height = 13
  Placement = pos=(15,0,12) rot=(0,1,0;1.5708rad)
  Radius = 1.8
  SecondAngle = 0
FEATURE [Part::Box] Box284  label="Krychle250"
  AttacherType = Attacher::AttachEngine3D
  Height = 8
  Length = 10
  Placement = pos=(18,-7,8) rot=(0,0,1;0rad)
  Width = 14
FEATURE [Part::MultiFuse] Fusion005043005007002049  label="telo"
  Shapes = -> [Cylinder112024025003003006010004079,Cylinder112024025003003006010004080,Box284]
FEATURE [Part::Box] Box285  label="Krychle251"
  AttacherType = Attacher::AttachEngine3D
  Height = 8
  Length = 2
  Placement = pos=(-1,-20,0) rot=(0,0,1;0rad)
  Width = 40
FEATURE [Part::Box] Box286  label="Krychle252"
  AttacherType = Attacher::AttachEngine3D
  Height = 8
  Length = 40
  Placement = pos=(-20,-1,0) rot=(0,0,1;0rad)
  Width = 2
FEATURE [Part::Cylinder] Cylinder112024025003003006010004084  label="Válec817"
  Angle = 360
  AttacherType = Attacher::AttachEngine3D
  FirstAngle = 0
  Height = 11
  Placement = pos=(25,4,12) rot=(0,0,1;0rad)
  Radius = 1
  SecondAngle = 0
FEATURE [Part::Cylinder] Cylinder112024025003003006010004085  label="Válec818"
  Angle = 360
  AttacherType = Attacher::AttachEngine3D
  FirstAngle = 0
  Height = 11
  Placement = pos=(25,-4,12) rot=(0,0,1;0rad)
  Radius = 1
  SecondAngle = 0
FEATURE [Part::Box] Box287  label="Krychle253"
  AttacherType = Attacher::AttachEngine3D
  Height = 4
  Length = 6
  Placement = pos=(22,-7,12) rot=(0,0,1;0rad)
  Width = 14
FEATURE [Part::Box] Box288  label="Krychle254"
  AttacherType = Attacher::AttachEngine3D
  Height = 4
  Length = 6
  Placement = pos=(22,-7,12) rot=(0,0,1;0rad)
  Width = 14
FEATURE [Part::Cylinder] Cylinder112024025003003006010004086  label="Válec819"
  Angle = 360
  AttacherType = Attacher::AttachEngine3D
  FirstAngle = 0
  Height = 11
  Placement = pos=(25,4,12) rot=(0,0,1;0rad)
  Radius = 1
  SecondAngle = 0
FEATURE [Part::Cylinder] Cylinder112024025003003006010004087  label="Válec820"
  Angle = 360
  AttacherType = Attacher::AttachEngine3D
  FirstAngle = 0
  Height = 11
  Placement = pos=(25,-4,12) rot=(0,0,1;0rad)
  Radius = 1
  SecondAngle = 0
FEATURE [Part::Cylinder] Cylinder112024025003003006010004088  label="Válec821"
  Angle = 360
  AttacherType = Attacher::AttachEngine3D
  FirstAngle = 0
  Height = 13
  Placement = pos=(15,0,12) rot=(0,1,0;1.5708rad)
  Radius = 1.5
  SecondAngle = 0
FEATURE [Part::MultiFuse] Fusion005043005007002051
  Shapes = -> [Cylinder112024025003003006010004086,Cylinder112024025003003006010004087,Cylinder112024025003003006010004088]
FEATURE [Part::Cut] Cut018020020009027020002003004004026  label="CableHolder"
  Base = -> Box288
  Tool = -> Fusion005043005007002051
FEATURE [Part::Cylinder] Cylinder112024025003003006010004089  label="Válec822"
  Angle = 360
  AttacherType = Attacher::AttachEngine3D
  FirstAngle = 0
  Height = 13
  Placement = pos=(9,0,11.5) rot=(0,1,0;1.5708rad)
  Radius = 2.2
  SecondAngle = 0
FEATURE [Part::MultiFuse] Fusion005043005007002050  label="diry025"
  Shapes = -> [Cylinder112024025003003006010004081,Cylinder112024025003003006010004082,Cylinder112024025003003006010004083,Box285,Box286,Cylinder112024025003003006010004084,Cylinder112024025003003006010004085,Box287,Cylinder112024025003003006010004089]
FEATURE [Part::Cut] Cut018020020009027020002003004004025  label="Polar scope Iluminator"
  Base = -> Fusion005043005007002049
  Tool = -> Fusion005043005007002050
FEATURE [App::Part] Part003  label="iIluminator"
  Group = -> [Fusion005043005007002050,Fusion005043005007002049,Box285,Cylinder112024025003003006010004085,Cylinder112024025003003006010004079,Cylinder112024025003003006010004082,Cylinder112024025003003006010004080,Cylinder112024025003003006010004081,Cylinder112024025003003006010004083,Box284,Box286,Box287,Cylinder112024025003003006010004089,Cylinder112024025003003006010004084,+7 more]
  Origin = -> Origin003
FEATURE [Part::Box] Box289  label="Krychle255"
  AttacherType = Attacher::AttachEngine3D
  Height = 16.5
  Length = 10
  Placement = pos=(-5,1.6,0) rot=(0,0,1;0rad)
  Width = 1.6
FEATURE [Part::Cylinder] Cylinder112024025003003006010004090  label="Válec823"
  Angle = 360
  AttacherType = Attacher::AttachEngine3D
  FirstAngle = 0
  Height = 13
  Placement = pos=(0,12,5.5) rot=(1,0,0;1.5708rad)
  Radius = 1.5
  SecondAngle = 0
FEATURE [Part::Feature] difference001002  label="difference003"
  Placement = pos=(0,0,0) rot=(0,0,1;1.0472rad)
  shape: bbox 27.96 x 27.96 x 17.5 mm, 1020 faces (baked)
FEATURE [Part::Cylinder] Cylinder112024025003003006010004091  label="Válec824"
  Angle = 360
  AttacherType = Attacher::AttachEngine3D
  FirstAngle = 0
  Height = 1.5
  Radius = 5
  SecondAngle = 0
FEATURE [Part::Cylinder] Cylinder112024025003003006010004092  label="Válec825"
  Angle = 360
  AttacherType = Attacher::AttachEngine3D
  FirstAngle = 0
  Height = 10
  Radius = 3.3
  SecondAngle = 0
FEATURE [Part::Cut] Cut018020020009027020002003004004028  label="Ring"
  Base = -> Cylinder112024025003003006010004091
  Tool = -> Cylinder112024025003003006010004092
FEATURE [Part::Cylinder] Cylinder112024025003003006010004093  label="Válec826"
  Angle = 360
  AttacherType = Attacher::AttachEngine3D
  FirstAngle = 0
  Height = 10
  Radius = 10.5
  SecondAngle = 0
FEATURE [Part::Cylinder] Cylinder112024025003003006010004094  label="Válec827"
  Angle = 360
  AttacherType = Attacher::AttachEngine3D
  FirstAngle = 0
  Height = 10
  Radius = 3.2
  SecondAngle = 0
FEATURE [Part::Cut] Cut018020020009027020002003004004029
  Base = -> Cylinder112024025003003006010004093
  Tool = -> Cylinder112024025003003006010004094
FEATURE [Part::MultiFuse] Fusion005043005007002052
  Shapes = -> [Box289,difference001002,Cut018020020009027020002003004004029]
FEATURE [Part::Cut] Cut018020020009027020002003004004027  label="Pulley40"
  Base = -> Fusion005043005007002052
  Tool = -> Cylinder112024025003003006010004090
FEATURE [Part::Feature] Cut018020020009027020002003004004027001  label="Pulley041"
  shape: bbox 27.96 x 27.96 x 17.5 mm, 994 faces (baked)
FEATURE [Part::FeaturePython] Screw022  label="M6x12-Screw006"  # Fasteners workbench fastener (typed FeaturePython)
  Placement = pos=(6.5,32.5,20.5) rot=(1,0,0;0rad)
  diameter = 8
  invert = false
  length = 0
  matchOuter = false
  offset = 0
  thread = false
  type = 14
FEATURE [Part::FeaturePython] Screw023  label="M4x25-Screw008"  # Fasteners workbench fastener (typed FeaturePython)
  Placement = pos=(47.5,49,45) rot=(0,-1,0;1.5708rad)
  diameter = 6
  invert = false
  length = 0
  matchOuter = false
  offset = 0
  thread = false
  type = 13
FEATURE [Part::FeaturePython] Screw024  label="M6x12-Screw007"  # Fasteners workbench fastener (typed FeaturePython)
  Placement = pos=(6.5,32.5,21.5) rot=(1,0,0;0rad)
  diameter = 8
  invert = false
  length = 0
  matchOuter = false
  offset = 0
  thread = false
  type = 14
FEATURE [Part::Feature] Fusion005043005007002053  label="Imbus008"
  Placement = pos=(31,0,0) rot=(0,0,1;0rad)
  shape: bbox 10.4 x 3 x 6.4 mm, 6 faces (baked)
FEATURE [Part::Feature] Fusion005043005007002054  label="Imbus009"
  Placement = pos=(31,0,31) rot=(0,0,1;0rad)
  shape: bbox 10.4 x 3 x 6.4 mm, 6 faces (baked)
FEATURE [Part::Feature] Fusion005043005007002055  label="Imbus010"
  Placement = pos=(0,0,31) rot=(0,0,1;0rad)
  shape: bbox 10.4 x 3 x 6.4 mm, 6 faces (baked)
FEATURE [Part::Part2DObjectPython] ShapeString024  # Draft 2D object (typed FeaturePython)
  FontFile = <path>
  Placement = pos=(15.3452,-2,30.5072) rot=(1,0,0;1.5708rad)
  Size = 4
  String = RA
  Tracking = 0
FEATURE [Part::Part2DObjectPython] ShapeString025  # Draft 2D object (typed FeaturePython)
  FontFile = <path>
  Placement = pos=(15.3452,-2,30.5072) rot=(1,0,0;1.5708rad)
  Size = 0.01
  String = .
  Tracking = 0
FEATURE [Part::Extrusion] Extrude094  label="Text TR006"
  Base = -> ShapeString025
  Dir = (0,-1,0)
  DirMode = 2
  FaceMakerClass = Part::FaceMakerBullseye
  LengthFwd = 1
  LengthRev = 0
  Placement = pos=(-6.75,1,-33) rot=(0,0,1;0rad)
  Solid = false
  Symmetric = false
FEATURE [Part::Extrusion] Extrude095  label="Text RA006"
  Base = -> ShapeString024
  Dir = (0,-1,0)
  DirMode = 2
  FaceMakerClass = Part::FaceMakerBullseye
  LengthFwd = 1
  LengthRev = 0
  Placement = pos=(4,0.7,-23.5) rot=(0,0,1;0rad)
  Solid = false
  Symmetric = false
FEATURE [Part::Cylinder] Cylinder112024025003003006010004095  label="Válec828"
  Angle = 360
  AttacherType = Attacher::AttachEngine3D
  FirstAngle = 0
  Height = 6.5
  Placement = pos=(53.5,21.25,0) rot=(0,0,1;0rad)
  Radius = 3.5
  SecondAngle = 0
FEATURE [Part::Cylinder] Cylinder112024025003003006010004096  label="Válec829"
  Angle = 360
  AttacherType = Attacher::AttachEngine3D
  FirstAngle = 0
  Height = 10
  Placement = pos=(8,64,60.5) rot=(1,0,0;1.5708rad)
  Radius = 1.65
  SecondAngle = 0
FEATURE [Part::Cylinder] Cylinder112024025003003006010004097  label="Válec830"
  Angle = 360
  AttacherType = Attacher::AttachEngine3D
  FirstAngle = 0
  Height = 10
  Placement = pos=(8,64,29.5) rot=(1,0,0;1.5708rad)
  Radius = 1.65
  SecondAngle = 0
FEATURE [Part::Box] Box290  label="Krychle256"
  AttacherType = Attacher::AttachEngine3D
  Height = 43
  Length = 65
  Placement = pos=(-5,15.5,49.5) rot=(1,0,0;0.523599rad)
  Width = 48
FEATURE [Part::Cylinder] Cylinder112024025003003006010004098  label="Válec831"
  Angle = 360
  AttacherType = Attacher::AttachEngine3D
  FirstAngle = 0
  Height = 10
  Placement = pos=(39,64,29.5) rot=(1,0,0;1.5708rad)
  Radius = 1.65
  SecondAngle = 0
FEATURE [Part::Box] Box291  label="konektor005"
  AttacherType = Attacher::AttachEngine3D
  Height = 29
  Length = 10
  Placement = pos=(50,16,37) rot=(0,0,1;0rad)
  Width = 12
FEATURE [Part::Box] Box292  label="Krychle257"
  AttacherType = Attacher::AttachEngine3D
  Height = 43
  Length = 59.5
  Placement = pos=(0,56,23) rot=(0,0,1;0rad)
  Width = 7
FEATURE [Part::Cylinder] Cylinder112024025003003006010004099  label="Válec832"
  Angle = 360
  AttacherType = Attacher::AttachEngine3D
  FirstAngle = 0
  Height = 20
  Placement = pos=(23.5,64,45) rot=(1,0,0;1.5708rad)
  Radius = 12.5
  SecondAngle = 0
FEATURE [Part::Box] Box293  label="Krychle258"
  AttacherType = Attacher::AttachEngine3D
  Height = 3.3
  Length = 4
  Placement = pos=(39,56,58.85) rot=(0,0,1;0rad)
  Width = 8
FEATURE [Part::MultiFuse] Fusion005043005007002058
  Shapes = -> [Extrude094,Extrude095]
FEATURE [Part::Box] Box294  label="Krychle259"
  AttacherType = Attacher::AttachEngine3D
  Height = 26
  Length = 58
  Placement = pos=(-0.5,0,-3) rot=(0,0,1;0rad)
  Width = 29
FEATURE [Part::Box] Box295  label="Krychle260"
  AttacherType = Attacher::AttachEngine3D
  Height = 3.3
  Length = 4
  Placement = pos=(8,56,27.85) rot=(0,0,1;0rad)
  Width = 8
FEATURE [Part::Cylinder] Cylinder112024025003003006010004100  label="Válec833"
  Angle = 360
  AttacherType = Attacher::AttachEngine3D
  FirstAngle = 0
  Height = 20
  Placement = pos=(23.5,64,45) rot=(1,0,0;1.5708rad)
  Radius = 12.5
  SecondAngle = 0
FEATURE [Part::Cylinder] Cylinder112024025003003006010004101  label="Válec834"
  Angle = 360
  AttacherType = Attacher::AttachEngine3D
  FirstAngle = 0
  Height = 10
  Placement = pos=(39,64,60.5) rot=(1,0,0;1.5708rad)
  Radius = 1.65
  SecondAngle = 0
FEATURE [Part::Box] Box296  label="Krychle261"
  AttacherType = Attacher::AttachEngine3D
  Height = 43
  Length = 4
  Placement = pos=(55.5,16,23) rot=(0,0,1;0rad)
  Width = 40
FEATURE [Part::Cylinder] Cylinder112024025003003006010004102  label="Válec835"
  Angle = 360
  AttacherType = Attacher::AttachEngine3D
  FirstAngle = 0
  Height = 10
  Placement = pos=(52,31,16.5) rot=(0,1,0;1.5708rad)
  Radius = 1.65
  SecondAngle = 0
FEATURE [Part::Box] Box297  label="Krychle262"
  AttacherType = Attacher::AttachEngine3D
  Height = 3.3
  Length = 4
  Placement = pos=(8,56,58.85) rot=(0,0,1;0rad)
  Width = 8
FEATURE [Part::Cylinder] Cylinder112024025003003006010004103  label="Válec836"
  Angle = 360
  AttacherType = Attacher::AttachEngine3D
  FirstAngle = 0
  Height = 8
  Placement = pos=(3.5,6,0) rot=(0,0,1;0rad)
  Radius = 0.7
  SecondAngle = 0
FEATURE [Part::Box] Box298  label="Krychle263"
  AttacherType = Attacher::AttachEngine3D
  Height = 3.3
  Length = 4
  Placement = pos=(39,56,27.85) rot=(0,0,1;0rad)
  Width = 8
FEATURE [Part::Cylinder] Cylinder112024025003003006010004104  label="Válec837"
  Angle = 360
  AttacherType = Attacher::AttachEngine3D
  FirstAngle = 0
  Height = 10
  Placement = pos=(39,64,60.5) rot=(1,0,0;1.5708rad)
  Radius = 1.65
  SecondAngle = 0
FEATURE [Part::Cylinder] Cylinder112024025003003006010004105  label="Válec838"
  Angle = 360
  AttacherType = Attacher::AttachEngine3D
  FirstAngle = 0
  Height = 70
  Placement = pos=(-5,20,16.5) rot=(0,1,0;1.5708rad)
  Radius = 1
  SecondAngle = 0
FEATURE [Part::Cylinder] Cylinder112024025003003006010004106  label="Válec839"
  Angle = 360
  AttacherType = Attacher::AttachEngine3D
  FirstAngle = 0
  Height = 10
  Placement = pos=(8,64,29.5) rot=(1,0,0;1.5708rad)
  Radius = 1.65
  SecondAngle = 0
FEATURE [Part::Box] Box299  label="Krychle264"
  AttacherType = Attacher::AttachEngine3D
  Height = 25
  Length = 4
  Placement = pos=(23.5,56,32.5) rot=(0,0,1;0rad)
  Width = 8
FEATURE [Part::Cylinder] Cylinder112024025003003006010004107  label="Válec840"
  Angle = 360
  AttacherType = Attacher::AttachEngine3D
  FirstAngle = 0
  Height = 6.5
  Placement = pos=(3.5,6,0) rot=(0,0,1;0rad)
  Radius = 3.5
  SecondAngle = 0
FEATURE [Part::Box] Box300  label="RJ060"
  AttacherType = Attacher::AttachEngine3D
  Height = 13
  Length = 16
  Placement = pos=(32,-5,4.5) rot=(0,0,1;0rad)
  Width = 18.5
FEATURE [Part::Cylinder] Cylinder112024025003003006010004108  label="Válec841"
  Angle = 360
  AttacherType = Attacher::AttachEngine3D
  FirstAngle = 0
  Height = 6.5
  Placement = pos=(53.5,6,0) rot=(0,0,1;0rad)
  Radius = 3.5
  SecondAngle = 0
FEATURE [Part::Cylinder] Cylinder112024025003003006010004109  label="Válec842"
  Angle = 360
  AttacherType = Attacher::AttachEngine3D
  FirstAngle = 0
  Height = 10
  Placement = pos=(39,64,29.5) rot=(1,0,0;1.5708rad)
  Radius = 1.65
  SecondAngle = 0
FEATURE [Part::MultiFuse] Fusion005043005007002059
  Placement = pos=(4,0,0) rot=(0,0,1;0rad)
  Shapes = -> [Cylinder112024025003003006010004106,Cylinder112024025003003006010004096,Cylinder112024025003003006010004104,Cylinder112024025003003006010004099,Cylinder112024025003003006010004109]
FEATURE [Part::Box] Box301  label="Krychle265"
  AttacherType = Attacher::AttachEngine3D
  Height = 8
  Length = 24
  Placement = pos=(-1.5,12.5,13.5) rot=(0,0,1;0rad)
  Width = 40
FEATURE [Part::Box] Box302  label="Krychle266"
  AttacherType = Attacher::AttachEngine3D
  Height = 28
  Length = 62
  Placement = pos=(-2.5,-2,-5) rot=(0,0,1;0rad)
  Width = 31
FEATURE [Part::Cut] Cut018020020009027020002003004004027006  label="Základ006"
  Base = -> Box302
  Tool = -> Box294
FEATURE [Part::Cylinder] Cylinder112024025003003006010004110  label="Válec843"
  Angle = 360
  AttacherType = Attacher::AttachEngine3D
  FirstAngle = 0
  Height = 8
  Placement = pos=(3.5,21.25,0) rot=(0,0,1;0rad)
  Radius = 0.75
  SecondAngle = 0
FEATURE [Part::Cylinder] Cylinder112024025003003006010004111  label="Válec844"
  Angle = 360
  AttacherType = Attacher::AttachEngine3D
  FirstAngle = 0
  Height = 6.5
  Placement = pos=(3.5,21.25,0) rot=(0,0,1;0rad)
  Radius = 3.5
  SecondAngle = 0
FEATURE [Part::MultiFuse] Fusion005043005007002065  label="sloupky009"
  Placement = pos=(0,0,-3.5) rot=(0,0,1;0rad)
  Shapes = -> [Cylinder112024025003003006010004111,Cylinder112024025003003006010004107,Cylinder112024025003003006010004095,Cylinder112024025003003006010004108]
FEATURE [Part::MultiFuse] Fusion005043005007002060  label="bez der006"
  Shapes = -> [Cut018020020009027020002003004004027006,Fusion005043005007002065]
FEATURE [Part::Box] Box303  label="Krychle267"
  AttacherType = Attacher::AttachEngine3D
  Height = 5
  Length = 62
  Placement = pos=(-2.5,-15,20.5) rot=(0,0,1;0rad)
  Width = 92
FEATURE [Part::Cylinder] Cylinder112024025003003006010004112  label="Válec845"
  Angle = 360
  AttacherType = Attacher::AttachEngine3D
  FirstAngle = 0
  Height = 8
  Placement = pos=(53.5,6,0) rot=(0,0,1;0rad)
  Radius = 0.75
  SecondAngle = 0
FEATURE [Part::Cylinder] Cylinder112024025003003006010004113  label="Válec846"
  Angle = 360
  AttacherType = Attacher::AttachEngine3D
  FirstAngle = 0
  Height = 10
  Placement = pos=(8,64,60.5) rot=(1,0,0;1.5708rad)
  Radius = 1.65
  SecondAngle = 0
FEATURE [Part::Cylinder] Cylinder112024025003003006010004114  label="Válec847"
  Angle = 360
  AttacherType = Attacher::AttachEngine3D
  FirstAngle = 0
  Height = 8
  Placement = pos=(53.5,21.25,0) rot=(0,0,1;0rad)
  Radius = 0.75
  SecondAngle = 0
FEATURE [Part::MultiFuse] Fusion005043005007002064  label="diry027"
  Placement = pos=(0,0,-4) rot=(0,0,1;0rad)
  Shapes = -> [Cylinder112024025003003006010004110,Cylinder112024025003003006010004103,Cylinder112024025003003006010004114,Cylinder112024025003003006010004112]
FEATURE [Part::Box] Box304  label="Krychle268"
  AttacherType = Attacher::AttachEngine3D
  Height = 8
  Length = 26
  Placement = pos=(22.5,22.5,13.5) rot=(0,0,1;0rad)
  Width = 20
FEATURE [Part::Cylinder] Cylinder112024025003003006010004115  label="Válec848"
  Angle = 360
  AttacherType = Attacher::AttachEngine3D
  FirstAngle = 0
  Height = 70
  Placement = pos=(-5,6,16.5) rot=(0,1,0;1.5708rad)
  Radius = 1
  SecondAngle = 0
FEATURE [Part::MultiFuse] Fusion005043005007002062  label="Horni diry015"
  Placement = pos=(0,0,3) rot=(0,0,1;0rad)
  Shapes = -> [Cylinder112024025003003006010004105,Cylinder112024025003003006010004115]
FEATURE [Part::Cylinder] Cylinder112024025003003006010004116  label="Válec849"
  Angle = 360
  AttacherType = Attacher::AttachEngine3D
  FirstAngle = 0
  Height = 5
  Placement = pos=(14.25,1,9.5) rot=(1,0,0;1.5708rad)
  Radius = 0.01
  SecondAngle = 0
FEATURE [Part::MultiFuse] Fusion005043005007002057  label="RJ a LED006"
  Shapes = -> [Box300,Cylinder112024025003003006010004116]
FEATURE [Part::MultiFuse] Fusion005043005007002067
  Shapes = -> [Fusion005043005007002064,Fusion005043005007002057,Fusion005043005007002062]
FEATURE [Part::Cut] Cut018020020009027020002003004004027002
  Base = -> Fusion005043005007002060
  Tool = -> Fusion005043005007002067
FEATURE [Part::Cut] Cut018020020009027020002003004004027004  label="PCB004"
  Base = -> Cut018020020009027020002003004004027002
  Placement = pos=(0,-13,26) rot=(1,0,0;0rad)
  Tool = -> Fusion005043005007002058
FEATURE [Part::Box] Box305  label="Krychle269"
  AttacherType = Attacher::AttachEngine3D
  Height = 3.3
  Length = 10
  Placement = pos=(52,31,14.85) rot=(0,0,1;0rad)
  Width = 6
FEATURE [Part::Cylinder] Cylinder112024025003003006010004117  label="Válec850"
  Angle = 360
  AttacherType = Attacher::AttachEngine3D
  FirstAngle = 0
  Height = 10
  Placement = pos=(52,37,16.5) rot=(0,1,0;1.5708rad)
  Radius = 1.65
  SecondAngle = 0
FEATURE [Part::MultiFuse] Fusion005043005007002061  label="Diryspodek002"
  Shapes = -> [Box305,Cylinder112024025003003006010004102,Cylinder112024025003003006010004117,Screw022,Screw024]
FEATURE [Part::Box] Box306  label="Krychle270"
  AttacherType = Attacher::AttachEngine3D
  Height = 8
  Length = 6
  Placement = pos=(53.5,22.5,13.5) rot=(0,0,1;0rad)
  Width = 20
FEATURE [Part::MultiFuse] Fusion005043005007002056  label="spodek004"
  Shapes = -> [Box303,Box306,Box301,Box304]
FEATURE [Part::Cut] Cut018020020009027020002003004004027003  label="Spodek002"
  Base = -> Fusion005043005007002056
  Placement = pos=(0,0,-2) rot=(0,0,1;0rad)
  Tool = -> Fusion005043005007002061
FEATURE [Part::Cylinder] Cylinder112024025003003006010004118  label="Válec851"
  Angle = 360
  AttacherType = Attacher::AttachEngine3D
  FirstAngle = 0
  Height = 3
  Placement = pos=(8,63,29.5) rot=(1,0,0;1.5708rad)
  Radius = 3.2
  SecondAngle = 0
FEATURE [Part::Box] Box307  label="Krychle271"
  AttacherType = Attacher::AttachEngine3D
  Height = 6.4
  Length = 4
  Placement = pos=(8,60,26.3) rot=(0,0,1;0rad)
  Width = 3
FEATURE [Part::Cylinder] Cylinder112024025003003006010004119  label="Válec852"
  Angle = 360
  AttacherType = Attacher::AttachEngine3D
  FirstAngle = 0
  Height = 3
  Placement = pos=(12,63,29.5) rot=(1,0,0;1.5708rad)
  Radius = 3.2
  SecondAngle = 0
FEATURE [Part::MultiFuse] Fusion005043005007002069  label="Imbus011"
  Shapes = -> [Cylinder112024025003003006010004119,Cylinder112024025003003006010004118,Box307]
FEATURE [Part::MultiFuse] Fusion005043005007002063  label="diry026"
  Placement = pos=(0,0,0.5) rot=(0,0,1;0rad)
  Shapes = -> [Cylinder112024025003003006010004097,Cylinder112024025003003006010004100,Cylinder112024025003003006010004113,Cylinder112024025003003006010004098,Cylinder112024025003003006010004101,Screw023,Fusion005043005007002059,Box299,Box295,Box293,Box298,Box297,Box291,Box290,Fusion005043005007002069,Fusion005043005007002053,Fusion005043005007002054,Fusion005043005007002055]
FEATURE [Part::Box] Box308  label="Krychle272"
  AttacherType = Attacher::AttachEngine3D
  Height = 43
  Length = 2.5
  Placement = pos=(-2.5,16,23) rot=(0,0,1;0rad)
  Width = 47
FEATURE [Part::MultiFuse] Fusion005043005007002068  label="Main005"
  Placement = pos=(0,0,0.5) rot=(0,0,1;0rad)
  Shapes = -> [Box292,Box296,Box308]
FEATURE [Part::Cut] Cut018020020009027020002003004004027005  label="RA003"
  Base = -> Fusion005043005007002068
  Tool = -> Fusion005043005007002063
FEATURE [Part::Box] Box309  label="Krychle273"
  AttacherType = Attacher::AttachEngine3D
  Height = 8
  Length = 62
  Placement = pos=(-2.5,63,18.5) rot=(0,0,1;0rad)
  Width = 14
FEATURE [Part::MultiFuse] Fusion005043005007002066  label="Raxxx001"
  Shapes = -> [Cut018020020009027020002003004004027004,Cut018020020009027020002003004004027003,Cut018020020009027020002003004004027005,Box309]
FEATURE [Part::Cylinder] Cylinder112024025003003006010004120  label="Válec853"
  Angle = 360
  AttacherType = Attacher::AttachEngine3D
  FirstAngle = 0
  Height = 10
  Placement = pos=(3,60,58) rot=(0,0,1;0rad)
  Radius = 0.8
  SecondAngle = 0
FEATURE [Part::Cylinder] Cylinder112024025003003006010004121  label="Válec854"
  Angle = 360
  AttacherType = Attacher::AttachEngine3D
  FirstAngle = 0
  Height = 10
  Placement = pos=(55,60,58) rot=(0,0,1;0rad)
  Radius = 0.8
  SecondAngle = 0
FEATURE [Part::FeaturePython] Screw025  label="M6x12-Screw008"  # Fasteners workbench fastener (typed FeaturePython)
  Placement = pos=(8.5,34,21.5) rot=(1,0,0;0rad)
  diameter = 8
  invert = false
  length = 0
  matchOuter = false
  offset = 0
  thread = false
  type = 14
FEATURE [Part::FeaturePython] Screw026  label="M6x12-Screw009"  # Fasteners workbench fastener (typed FeaturePython)
  Placement = pos=(8.5,34,20.5) rot=(1,0,0;0rad)
  diameter = 8
  invert = false
  length = 0
  matchOuter = false
  offset = 0
  thread = false
  type = 14
FEATURE [Part::FeaturePython] Screw027  label="M4x25-Screw009"  # Fasteners workbench fastener (typed FeaturePython)
  Placement = pos=(47.5,49,45) rot=(0,-1,0;1.5708rad)
  diameter = 6
  invert = false
  length = 0
  matchOuter = false
  offset = 0
  thread = false
  type = 13
FEATURE [Part::Part2DObjectPython] ShapeString026  # Draft 2D object (typed FeaturePython)
  FontFile = <path>
  Placement = pos=(15.3452,-2,30.5072) rot=(1,0,0;1.5708rad)
  Size = 4
  String = DEC
  Tracking = 0
FEATURE [Part::MultiFuse] Fusion005043005007002080
  Shapes = -> [Screw025,Screw026]
FEATURE [Part::Cylinder] Cylinder112024025003003006010004124  label="Válec857"
  Angle = 360
  AttacherType = Attacher::AttachEngine3D
  FirstAngle = 0
  Height = 6.5
  Placement = pos=(53.5,21.25,0) rot=(0,0,1;0rad)
  Radius = 3.5
  SecondAngle = 0
FEATURE [Part::Cylinder] Cylinder112024025003003006010004125  label="Válec858"
  Angle = 360
  AttacherType = Attacher::AttachEngine3D
  FirstAngle = 0
  Height = 70
  Placement = pos=(-5,20,16.5) rot=(0,1,0;1.5708rad)
  Radius = 1
  SecondAngle = 0
FEATURE [Part::Box] Box310  label="Krychle274"
  AttacherType = Attacher::AttachEngine3D
  Height = 9
  Length = 26
  Placement = pos=(-2,24,13) rot=(0,0,1;0rad)
  Width = 20
FEATURE [Part::Cylinder] Cylinder112024025003003006010004126  label="Válec859"
  Angle = 360
  AttacherType = Attacher::AttachEngine3D
  FirstAngle = 0
  Height = 8
  Placement = pos=(53.5,21.25,0) rot=(0,0,1;0rad)
  Radius = 0.75
  SecondAngle = 0
FEATURE [Part::Cylinder] Cylinder112024025003003006010004127  label="Válec860"
  Angle = 360
  AttacherType = Attacher::AttachEngine3D
  FirstAngle = 0
  Height = 8
  Placement = pos=(3.5,6,0) rot=(0,0,1;0rad)
  Radius = 0.7
  SecondAngle = 0
FEATURE [Part::Extrusion] Extrude097  label="Text RA007"
  Base = -> ShapeString026
  Dir = (0,-1,0)
  DirMode = 2
  FaceMakerClass = Part::FaceMakerBullseye
  LengthFwd = 1
  LengthRev = 0
  Placement = pos=(48,1,32.5) rot=(0,1,0;3.14159rad)
  Solid = false
  Symmetric = false
FEATURE [Part::Cylinder] Cylinder112024025003003006010004128  label="Válec861"
  Angle = 360
  AttacherType = Attacher::AttachEngine3D
  FirstAngle = 0
  Height = 8
  Placement = pos=(53.5,6,0) rot=(0,0,1;0rad)
  Radius = 0.75
  SecondAngle = 0
FEATURE [Part::Box] Box311  label="Krychle275"
  AttacherType = Attacher::AttachEngine3D
  Height = 26
  Length = 58
  Placement = pos=(-0.5,0,-3) rot=(0,0,1;0rad)
  Width = 29
FEATURE [Part::Box] Box312  label="RJ061"
  AttacherType = Attacher::AttachEngine3D
  Height = 13
  Length = 16
  Placement = pos=(32,-5,4.5) rot=(0,0,1;0rad)
  Width = 18.5
FEATURE [Part::Cylinder] Cylinder112024025003003006010004129  label="Válec862"
  Angle = 360
  AttacherType = Attacher::AttachEngine3D
  FirstAngle = 0
  Height = 70
  Placement = pos=(-5,6,16.5) rot=(0,1,0;1.5708rad)
  Radius = 1
  SecondAngle = 0
FEATURE [Part::MultiFuse] Fusion005043005007002072  label="Horni diry016"
  Placement = pos=(0,0,3) rot=(0,0,1;0rad)
  Shapes = -> [Cylinder112024025003003006010004125,Cylinder112024025003003006010004129]
FEATURE [Part::Box] Box313  label="Krychle276"
  AttacherType = Attacher::AttachEngine3D
  Height = 28
  Length = 62
  Placement = pos=(-2.5,-2,-5) rot=(0,0,1;0rad)
  Width = 31
FEATURE [Part::Cylinder] Cylinder112024025003003006010004130  label="Válec863"
  Angle = 360
  AttacherType = Attacher::AttachEngine3D
  FirstAngle = 0
  Height = 6.5
  Placement = pos=(3.5,21.25,0) rot=(0,0,1;0rad)
  Radius = 3.5
  SecondAngle = 0
FEATURE [Part::Cylinder] Cylinder112024025003003006010004131  label="Válec864"
  Angle = 360
  AttacherType = Attacher::AttachEngine3D
  FirstAngle = 0
  Height = 6.5
  Placement = pos=(3.5,6,0) rot=(0,0,1;0rad)
  Radius = 3.5
  SecondAngle = 0
FEATURE [Part::Box] Box314  label="Krychle277"
  AttacherType = Attacher::AttachEngine3D
  Height = 5
  Length = 62
  Placement = pos=(-2.5,-15,20.5) rot=(0,0,1;0rad)
  Width = 78
FEATURE [Part::MultiFuse] Fusion005043005007002081  label="spodek005"
  Shapes = -> [Box314,Box310]
FEATURE [Part::Cylinder] Cylinder112024025003003006010004132  label="Válec865"
  Angle = 360
  AttacherType = Attacher::AttachEngine3D
  FirstAngle = 0
  Height = 5
  Placement = pos=(14.25,1,9.5) rot=(1,0,0;1.5708rad)
  Radius = 0.01
  SecondAngle = 0
FEATURE [Part::MultiFuse] Fusion005043005007002075  label="RJ a LED007"
  Shapes = -> [Box312,Cylinder112024025003003006010004132]
FEATURE [Part::Cylinder] Cylinder112024025003003006010004133  label="Válec866"
  Angle = 360
  AttacherType = Attacher::AttachEngine3D
  FirstAngle = 0
  Height = 8
  Placement = pos=(3.5,21.25,0) rot=(0,0,1;0rad)
  Radius = 0.75
  SecondAngle = 0
FEATURE [Part::MultiFuse] Fusion005043005007002078  label="diry028"
  Placement = pos=(0,0,-4) rot=(0,0,1;0rad)
  Shapes = -> [Cylinder112024025003003006010004133,Cylinder112024025003003006010004127,Cylinder112024025003003006010004126,Cylinder112024025003003006010004128]
FEATURE [Part::MultiFuse] Fusion005043005007002083
  Shapes = -> [Fusion005043005007002078,Fusion005043005007002075,Fusion005043005007002072]
FEATURE [Part::Cut] Cut018020020009027020002003004004027010  label="Základ007"
  Base = -> Box313
  Tool = -> Box311
FEATURE [Part::Cut] Cut018020020009027020002003004004027011
  Base = -> Fusion005043005007002081
  Placement = pos=(0,0,-2) rot=(0,0,1;0rad)
  Tool = -> Fusion005043005007002080
FEATURE [Part::Feature] Fusion005043005007002085  label="Imbus013"
  Placement = pos=(31,0,0) rot=(0,0,1;0rad)
  shape: bbox 10.4 x 3 x 6.4 mm, 6 faces (baked)
FEATURE [Part::Feature] Fusion005043005007002086  label="Imbus014"
  Placement = pos=(31,0,31) rot=(0,0,1;0rad)
  shape: bbox 10.4 x 3 x 6.4 mm, 6 faces (baked)
FEATURE [Part::Feature] Fusion005043005007002087  label="Imbus015"
  Placement = pos=(0,0,31) rot=(0,0,1;0rad)
  shape: bbox 10.4 x 3 x 6.4 mm, 6 faces (baked)
FEATURE [Part::Cylinder] Cylinder112024025003003006010004134  label="Válec867"
  Angle = 360
  AttacherType = Attacher::AttachEngine3D
  FirstAngle = 0
  Height = 10
  Placement = pos=(39,64,60.5) rot=(1,0,0;1.5708rad)
  Radius = 1.65
  SecondAngle = 0
FEATURE [Part::Box] Box315  label="konektor006"
  AttacherType = Attacher::AttachEngine3D
  Height = 29
  Length = 10
  Placement = pos=(50,16,37) rot=(0,0,1;0rad)
  Width = 12
FEATURE [Part::Cylinder] Cylinder112024025003003006010004135  label="Válec868"
  Angle = 360
  AttacherType = Attacher::AttachEngine3D
  FirstAngle = 0
  Height = 10
  Placement = pos=(8,64,29.5) rot=(1,0,0;1.5708rad)
  Radius = 1.65
  SecondAngle = 0
FEATURE [Part::Box] Box316  label="Krychle278"
  AttacherType = Attacher::AttachEngine3D
  Height = 3.3
  Length = 4
  Placement = pos=(8,56,27.85) rot=(0,0,1;0rad)
  Width = 8
FEATURE [Part::Cylinder] Cylinder112024025003003006010004136  label="Válec869"
  Angle = 360
  AttacherType = Attacher::AttachEngine3D
  FirstAngle = 0
  Height = 3
  Placement = pos=(12,63,29.5) rot=(1,0,0;1.5708rad)
  Radius = 3.2
  SecondAngle = 0
FEATURE [Part::Cylinder] Cylinder112024025003003006010004137  label="Válec870"
  Angle = 360
  AttacherType = Attacher::AttachEngine3D
  FirstAngle = 0
  Height = 6.5
  Placement = pos=(53.5,6,0) rot=(0,0,1;0rad)
  Radius = 3.5
  SecondAngle = 0
FEATURE [Part::MultiFuse] Fusion005043005007002073  label="sloupky010"
  Placement = pos=(0,0,-3.5) rot=(0,0,1;0rad)
  Shapes = -> [Cylinder112024025003003006010004130,Cylinder112024025003003006010004131,Cylinder112024025003003006010004124,Cylinder112024025003003006010004137]
FEATURE [Part::MultiFuse] Fusion005043005007002074  label="bez der007"
  Shapes = -> [Cut018020020009027020002003004004027010,Fusion005043005007002073]
FEATURE [Part::Cut] Cut018020020009027020002003004004027012
  Base = -> Fusion005043005007002074
  Tool = -> Fusion005043005007002083
FEATURE [Part::Box] Box317  label="Krychle279"
  AttacherType = Attacher::AttachEngine3D
  Height = 25
  Length = 4
  Placement = pos=(23.5,56,32.5) rot=(0,0,1;0rad)
  Width = 8
FEATURE [Part::Cylinder] Cylinder112024025003003006010004138  label="Válec871"
  Angle = 360
  AttacherType = Attacher::AttachEngine3D
  FirstAngle = 0
  Height = 20
  Placement = pos=(23.5,64,45) rot=(1,0,0;1.5708rad)
  Radius = 12.5
  SecondAngle = 0
FEATURE [Part::Box] Box318  label="Krychle280"
  AttacherType = Attacher::AttachEngine3D
  Height = 43
  Length = 59.5
  Placement = pos=(0,56,23) rot=(0,0,1;0rad)
  Width = 7
FEATURE [Part::Cylinder] Cylinder112024025003003006010004139  label="Válec872"
  Angle = 360
  AttacherType = Attacher::AttachEngine3D
  FirstAngle = 0
  Height = 10
  Placement = pos=(8,64,60.5) rot=(1,0,0;1.5708rad)
  Radius = 1.65
  SecondAngle = 0
FEATURE [Part::Box] Box319  label="Krychle281"
  AttacherType = Attacher::AttachEngine3D
  Height = 3.3
  Length = 4
  Placement = pos=(8,56,58.85) rot=(0,0,1;0rad)
  Width = 8
FEATURE [Part::Cylinder] Cylinder112024025003003006010004140  label="Válec873"
  Angle = 360
  AttacherType = Attacher::AttachEngine3D
  FirstAngle = 0
  Height = 10
  Placement = pos=(39,64,29.5) rot=(1,0,0;1.5708rad)
  Radius = 1.65
  SecondAngle = 0
FEATURE [Part::Cylinder] Cylinder112024025003003006010004141  label="Válec874"
  Angle = 360
  AttacherType = Attacher::AttachEngine3D
  FirstAngle = 0
  Height = 10
  Placement = pos=(39,64,60.5) rot=(1,0,0;1.5708rad)
  Radius = 1.65
  SecondAngle = 0
FEATURE [Part::Box] Box320  label="Krychle282"
  AttacherType = Attacher::AttachEngine3D
  Height = 3.3
  Length = 4
  Placement = pos=(39,56,27.85) rot=(0,0,1;0rad)
  Width = 8
FEATURE [Part::Cylinder] Cylinder112024025003003006010004142  label="Válec875"
  Angle = 360
  AttacherType = Attacher::AttachEngine3D
  FirstAngle = 0
  Height = 10
  Placement = pos=(8,64,29.5) rot=(1,0,0;1.5708rad)
  Radius = 1.65
  SecondAngle = 0
FEATURE [Part::Box] Box321  label="Krychle283"
  AttacherType = Attacher::AttachEngine3D
  Height = 43
  Length = 4
  Placement = pos=(55.5,16,23) rot=(0,0,1;0rad)
  Width = 40
FEATURE [Part::Box] Box322  label="Krychle284"
  AttacherType = Attacher::AttachEngine3D
  Height = 43
  Length = 65
  Placement = pos=(-5,15.5,49.5) rot=(1,0,0;0.523599rad)
  Width = 48
FEATURE [Part::Cylinder] Cylinder112024025003003006010004143  label="Válec876"
  Angle = 360
  AttacherType = Attacher::AttachEngine3D
  FirstAngle = 0
  Height = 10
  Placement = pos=(8,64,60.5) rot=(1,0,0;1.5708rad)
  Radius = 1.65
  SecondAngle = 0
FEATURE [Part::Cylinder] Cylinder112024025003003006010004144  label="Válec877"
  Angle = 360
  AttacherType = Attacher::AttachEngine3D
  FirstAngle = 0
  Height = 10
  Placement = pos=(39,64,29.5) rot=(1,0,0;1.5708rad)
  Radius = 1.65
  SecondAngle = 0
FEATURE [Part::Box] Box323  label="Krychle285"
  AttacherType = Attacher::AttachEngine3D
  Height = 3.3
  Length = 4
  Placement = pos=(39,56,58.85) rot=(0,0,1;0rad)
  Width = 8
FEATURE [Part::Cylinder] Cylinder112024025003003006010004145  label="Válec878"
  Angle = 360
  AttacherType = Attacher::AttachEngine3D
  FirstAngle = 0
  Height = 3
  Placement = pos=(8,63,29.5) rot=(1,0,0;1.5708rad)
  Radius = 3.2
  SecondAngle = 0
FEATURE [Part::Box] Box324  label="Krychle286"
  AttacherType = Attacher::AttachEngine3D
  Height = 6.4
  Length = 4
  Placement = pos=(8,60,26.3) rot=(0,0,1;0rad)
  Width = 3
FEATURE [Part::MultiFuse] Fusion005043005007002079  label="Imbus012"
  Shapes = -> [Cylinder112024025003003006010004136,Cylinder112024025003003006010004145,Box324]
FEATURE [Part::Box] Box325  label="Krychle287"
  AttacherType = Attacher::AttachEngine3D
  Height = 43
  Length = 2.5
  Placement = pos=(-2.5,16,23) rot=(0,0,1;0rad)
  Width = 47
FEATURE [Part::MultiFuse] Fusion005043005007002082  label="Main006"
  Placement = pos=(0,0,0.5) rot=(0,0,1;0rad)
  Shapes = -> [Box318,Box321,Box325]
FEATURE [Part::Cylinder] Cylinder112024025003003006010004146  label="Válec879"
  Angle = 360
  AttacherType = Attacher::AttachEngine3D
  FirstAngle = 0
  Height = 20
  Placement = pos=(23.5,64,45) rot=(1,0,0;1.5708rad)
  Radius = 12.5
  SecondAngle = 0
FEATURE [Part::MultiFuse] Fusion005043005007002077
  Placement = pos=(4,0,0) rot=(0,0,1;0rad)
  Shapes = -> [Cylinder112024025003003006010004142,Cylinder112024025003003006010004143,Cylinder112024025003003006010004141,Cylinder112024025003003006010004146,Cylinder112024025003003006010004140]
FEATURE [Part::MultiFuse] Fusion005043005007002084  label="diry029"
  Placement = pos=(0,0,0.5) rot=(0,0,1;0rad)
  Shapes = -> [Cylinder112024025003003006010004135,Cylinder112024025003003006010004138,Cylinder112024025003003006010004139,Cylinder112024025003003006010004144,Cylinder112024025003003006010004134,Screw027,Fusion005043005007002077,Box317,Box316,Box323,Box320,Box319,Box315,Box322,Fusion005043005007002079,Fusion005043005007002085,Fusion005043005007002086,Fusion005043005007002087]
FEATURE [Part::Cut] Cut018020020009027020002003004004027008  label="DE004"
  Base = -> Fusion005043005007002082
  Tool = -> Fusion005043005007002084
FEATURE [Part::Cylinder] Cylinder112024025003003006010004147  label="Válec880"
  Angle = 360
  AttacherType = Attacher::AttachEngine3D
  FirstAngle = 0
  Height = 10
  Placement = pos=(55,60,58) rot=(0,0,1;0rad)
  Radius = 0.8
  SecondAngle = 0
FEATURE [Part::Cylinder] Cylinder112024025003003006010004148  label="Válec881"
  Angle = 360
  AttacherType = Attacher::AttachEngine3D
  FirstAngle = 0
  Height = 10
  Placement = pos=(52,78,22.5) rot=(1,0,0;1.5708rad)
  Radius = 1.75
  SecondAngle = 0
FEATURE [Part::Cylinder] Cylinder112024025003003006010004149  label="Válec882"
  Angle = 360
  AttacherType = Attacher::AttachEngine3D
  FirstAngle = 0
  Height = 10
  Placement = pos=(3,60,58) rot=(0,0,1;0rad)
  Radius = 0.8
  SecondAngle = 0
FEATURE [Part::Cylinder] Cylinder112024025003003006010004150  label="Válec883"
  Angle = 360
  AttacherType = Attacher::AttachEngine3D
  FirstAngle = 0
  Height = 10
  Placement = pos=(4,78,22.5) rot=(1,0,0;1.5708rad)
  Radius = 1.75
  SecondAngle = 0
FEATURE [Part::Box] Box326  label="Krychle288"
  AttacherType = Attacher::AttachEngine3D
  Height = 8
  Length = 62
  Placement = pos=(-2.5,63,18.5) rot=(0,0,1;0rad)
  Width = 14
FEATURE [Part::Part2DObjectPython] ShapeString027  # Draft 2D object (typed FeaturePython)
  FontFile = <path>
  Placement = pos=(15.3452,-2,30.5072) rot=(1,0,0;1.5708rad)
  Size = 0.01
  String = .
  Tracking = 0
FEATURE [Part::Extrusion] Extrude096  label="Text TR007"
  Base = -> ShapeString027
  Dir = (0,-1,0)
  DirMode = 2
  FaceMakerClass = Part::FaceMakerBullseye
  LengthFwd = 1
  LengthRev = 0
  Placement = pos=(-6.75,1.5,-33) rot=(0,0,1;0rad)
  Solid = false
  Symmetric = false
FEATURE [Part::MultiFuse] Fusion005043005007002076
  Shapes = -> [Extrude096,Extrude097]
FEATURE [Part::Cut] Cut018020020009027020002003004004027009  label="PCB005"
  Base = -> Cut018020020009027020002003004004027012
  Placement = pos=(0,-13,26) rot=(1,0,0;0rad)
  Tool = -> Fusion005043005007002076
FEATURE [Part::MultiFuse] Fusion005043005007002071  label="DECV003"
  Shapes = -> [Cut018020020009027020002003004004027009,Cut018020020009027020002003004004027008,Cut018020020009027020002003004004027011]
FEATURE [Part::Feature] Fillet004005003002003002001  label="Dec red001"
  shape: bbox 63.32 x 91.01 x 55.5 mm, 323 faces (baked)
FEATURE [Part::Cylinder] Cylinder112024025003003006010004151  label="Válec884"
  Angle = 360
  AttacherType = Attacher::AttachEngine3D
  FirstAngle = 0
  Height = 10
  Placement = pos=(3,60,58) rot=(0,0,1;0rad)
  Radius = 0.8
  SecondAngle = 0
FEATURE [Part::Cylinder] Cylinder112024025003003006010004152  label="Válec885"
  Angle = 360
  AttacherType = Attacher::AttachEngine3D
  FirstAngle = 0
  Height = 10
  Placement = pos=(52,78,22.5) rot=(1,0,0;1.5708rad)
  Radius = 1.75
  SecondAngle = 0
FEATURE [Part::Cylinder] Cylinder112024025003003006010004153  label="Válec886"
  Angle = 360
  AttacherType = Attacher::AttachEngine3D
  FirstAngle = 0
  Height = 10
  Placement = pos=(55,60,58) rot=(0,0,1;0rad)
  Radius = 0.8
  SecondAngle = 0
FEATURE [Part::Cylinder] Cylinder112024025003003006010004154  label="Válec887"
  Angle = 360
  AttacherType = Attacher::AttachEngine3D
  FirstAngle = 0
  Height = 10
  Placement = pos=(4,78,22.5) rot=(1,0,0;1.5708rad)
  Radius = 1.75
  SecondAngle = 0
FEATURE [Part::MultiFuse] Fusion005043005007002070  label="dirky kryt"
  Shapes = -> [Cylinder112024025003003006010004120,Cylinder112024025003003006010004121,Cylinder112024025003003006010004152,Cylinder112024025003003006010004154]
FEATURE [Part::Cut] Cut018020020009027020002003004004027007
  Base = -> Fusion005043005007002066
  Tool = -> Fusion005043005007002070
FEATURE [Part::Fillet] Fillet004005003002003  label="RA red"
  Base = -> Cut018020020009027020002003004004027007
  Edges = 6 edges r=2: [Edge5,Edge24,Edge27,Edge67,Edge69,Edge149]
FEATURE [Part::MultiFuse] Fusion005043005007002090  label="dirky kryt002"
  Shapes = -> [Cylinder112024025003003006010004151,Cylinder112024025003003006010004153,Cylinder112024025003003006010004152,Cylinder112024025003003006010004154]
FEATURE [Part::Feature] Fillet004005003002003002002  label="RA red001"
  shape: bbox 62 x 92 x 55 mm, 181 faces (baked)
FEATURE [Part::Feature] Fillet004005003002003002003001  label="viko"
  shape: bbox 62 x 26 x 10 mm, 161 faces (baked)
FEATURE [Part::Feature] Fillet004005003002003002003003  label="RA red002"
  shape: bbox 62 x 92 x 55 mm, 181 faces (baked)
FEATURE [Part::Box] Box327  label="Krychle289"
  AttacherType = Attacher::AttachEngine3D
  Height = 55
  Length = 100
  Placement = pos=(-40.5,81,18.5) rot=(0,0,1;0rad)
  Width = 2
FEATURE [Part::Box] Box328  label="Krychle290"
  AttacherType = Attacher::AttachEngine3D
  Height = 8
  Length = 92
  Placement = pos=(-32.5,77,18.5) rot=(0,0,1;0rad)
  Width = 4
FEATURE [Part::Cylinder] Cylinder112024025003003006010004155  label="Válec888"
  Angle = 360
  AttacherType = Attacher::AttachEngine3D
  FirstAngle = 0
  Height = 100
  Placement = pos=(-57,32,0) rot=(0,0,1;0rad)
  Radius = 50
  SecondAngle = 0
FEATURE [Part::Box] Box329  label="Krychle291"
  AttacherType = Attacher::AttachEngine3D
  Height = 47
  Length = 4
  Placement = pos=(55.5,63.5,26.5) rot=(0,0,1;0rad)
  Width = 17.5
FEATURE [Part::Box] Box330  label="Krychle292"
  AttacherType = Attacher::AttachEngine3D
  Height = 7
  Length = 100
  Placement = pos=(-40.5,57,66.5) rot=(0,0,1;0rad)
  Width = 24
FEATURE [Part::MultiFuse] Fusion005043005007002091  label="Main007"
  Shapes = -> [Box330,Box327,Box328,Box329]
FEATURE [Part::Box] Box331  label="Krychle293"
  AttacherType = Attacher::AttachEngine3D
  Height = 5
  Length = 59
  Placement = pos=(0.5,57,68.5) rot=(0,0,1;0rad)
  Width = 26
FEATURE [Part::Cylinder] Cylinder112024025003003006010004156  label="Válec889"
  Angle = 360
  AttacherType = Attacher::AttachEngine3D
  FirstAngle = 0
  Height = 10
  Placement = pos=(55,60,61) rot=(0,0,1;0rad)
  Radius = 1.1
  SecondAngle = 0
FEATURE [Part::Cylinder] Cylinder112024025003003006010004157  label="Válec890"
  Angle = 360
  AttacherType = Attacher::AttachEngine3D
  FirstAngle = 0
  Height = 10
  Placement = pos=(3,60,60) rot=(0,0,1;0rad)
  Radius = 1.1
  SecondAngle = 0
FEATURE [Part::Cylinder] Cylinder112024025003003006010004158  label="Válec891"
  Angle = 360
  AttacherType = Attacher::AttachEngine3D
  FirstAngle = 0
  Height = 10
  Placement = pos=(52,86,22.5) rot=(1,0,0;1.5708rad)
  Radius = 2.1
  SecondAngle = 0
FEATURE [Part::Cylinder] Cylinder112024025003003006010004159  label="Válec892"
  Angle = 360
  AttacherType = Attacher::AttachEngine3D
  FirstAngle = 0
  Height = 10
  Placement = pos=(4,86,22.5) rot=(1,0,0;1.5708rad)
  Radius = 2.1
  SecondAngle = 0
FEATURE [Part::MultiFuse] Fusion005043005007002093  label="dirky kryt003"
  Shapes = -> [Cylinder112024025003003006010004157,Cylinder112024025003003006010004156,Cylinder112024025003003006010004158,Cylinder112024025003003006010004159]
FEATURE [Part::Box] Box332  label="Krychle294"
  AttacherType = Attacher::AttachEngine3D
  Height = 5
  Length = 35
  Placement = pos=(-40.5,57,66.5) rot=(0,0,1;0rad)
  Width = 24
FEATURE [Part::Box] Box333  label="Krychle295"
  AttacherType = Attacher::AttachEngine3D
  Height = 7
  Length = 4
  Placement = pos=(-5.5,57,63.5) rot=(0,-1,0;0.523599rad)
  Width = 24
FEATURE [Part::Box] Box334  label="Krychle296"
  AttacherType = Attacher::AttachEngine3D
  Height = 7
  Length = 4
  Placement = pos=(0.5,57,68.5) rot=(0,-1,0;0.523599rad)
  Width = 26
FEATURE [Part::Cylinder] Cylinder112024025003003006010004160  label="Válec893"
  Angle = 360
  AttacherType = Attacher::AttachEngine3D
  FirstAngle = 0
  Height = 10
  Placement = pos=(-15,86,52) rot=(1,0,0;1.5708rad)
  Radius = 13
  SecondAngle = 0
FEATURE [Part::MultiFuse] Fusion005043005007002092  label="Orez"
  Shapes = -> [Cylinder112024025003003006010004155,Box331,Fusion005043005007002093,Box332,Box333,Box334,Cylinder112024025003003006010004160]
FEATURE [Part::Cut] Cut018020020009027020002003004004027014  label="RA CAP"
  Base = -> Fusion005043005007002091
  Tool = -> Fusion005043005007002092
FEATURE [Part::Fillet] Fillet004005003002003002003004  label="RA-Cap"
  Base = -> Cut018020020009027020002003004004027014
  Edges = 11 edges r=1: [Edge6,Edge12,Edge19,Edge20,Edge22,Edge42,Edge43,Edge44,Edge52,Edge53,Edge54]
FEATURE [Part::Cylinder] Cylinder112024025003003006010004161  label="Válec894"
  Angle = 360
  AttacherType = Attacher::AttachEngine3D
  FirstAngle = 0
  Height = 10
  Placement = pos=(55,60,61) rot=(0,0,1;0rad)
  Radius = 1.1
  SecondAngle = 0
FEATURE [Part::Box] Box335  label="Krychle297"
  AttacherType = Attacher::AttachEngine3D
  Height = 55
  Length = 100
  Placement = pos=(-40.5,81,18.5) rot=(0,0,1;0rad)
  Width = 2
FEATURE [Part::Cylinder] Cylinder112024025003003006010004162  label="Válec895"
  Angle = 360
  AttacherType = Attacher::AttachEngine3D
  FirstAngle = 0
  Height = 100
  Placement = pos=(-57,31,0) rot=(0,0,1;0rad)
  Radius = 49
  SecondAngle = 0
FEATURE [Part::Cylinder] Cylinder112024025003003006010004163  label="Válec896"
  Angle = 360
  AttacherType = Attacher::AttachEngine3D
  FirstAngle = 0
  Height = 10
  Placement = pos=(-14,86,48.5) rot=(1,0,0;1.5708rad)
  Radius = 13
  SecondAngle = 0
FEATURE [Part::Box] Box336  label="Krychle298"
  AttacherType = Attacher::AttachEngine3D
  Height = 8
  Length = 100
  Placement = pos=(-40.5,77,18.5) rot=(0,0,1;0rad)
  Width = 4
FEATURE [Part::Box] Box337  label="Krychle299"
  AttacherType = Attacher::AttachEngine3D
  Height = 47
  Length = 4
  Placement = pos=(55.5,63.5,26.5) rot=(0,0,1;0rad)
  Width = 17.5
FEATURE [Part::Box] Box339  label="Krychle301"
  AttacherType = Attacher::AttachEngine3D
  Height = 7
  Length = 100
  Placement = pos=(-40.5,57,66.5) rot=(0,0,1;0rad)
  Width = 24
FEATURE [Part::Cylinder] Cylinder112024025003003006010004164  label="Válec897"
  Angle = 360
  AttacherType = Attacher::AttachEngine3D
  FirstAngle = 0
  Height = 10
  Placement = pos=(52,86,22.5) rot=(1,0,0;1.5708rad)
  Radius = 2.1
  SecondAngle = 0
FEATURE [Part::Cylinder] Cylinder112024025003003006010004165  label="Válec898"
  Angle = 360
  AttacherType = Attacher::AttachEngine3D
  FirstAngle = 0
  Height = 10
  Placement = pos=(4,86,22.5) rot=(1,0,0;1.5708rad)
  Radius = 2.1
  SecondAngle = 0
FEATURE [Part::Cylinder] Cylinder112024025003003006010004166  label="Válec899"
  Angle = 360
  AttacherType = Attacher::AttachEngine3D
  FirstAngle = 0
  Height = 10
  Placement = pos=(3,60,60) rot=(0,0,1;0rad)
  Radius = 1.1
  SecondAngle = 0
FEATURE [Part::Box] Box341  label="Krychle303"
  AttacherType = Attacher::AttachEngine3D
  Height = 5
  Length = 100
  Placement = pos=(-40.5,57,68.5) rot=(0,0,1;0rad)
  Width = 26
FEATURE [Part::MultiFuse] Fusion005043005007002096  label="dirky kryt004"
  Shapes = -> [Cylinder112024025003003006010004166,Cylinder112024025003003006010004161,Cylinder112024025003003006010004164,Cylinder112024025003003006010004165]
FEATURE [Part::MultiFuse] Fusion005043005007002095  label="Orez001"
  Shapes = -> [Cylinder112024025003003006010004162,Box341,Fusion005043005007002096,Cylinder112024025003003006010004163]
FEATURE [Part::Feature] Fillet004005003002003002003004003  label="RA-Cap001"
  shape: bbox 100 x 26 x 55 mm, 35 faces (baked)
FEATURE [Part::Feature] Fillet004005003002003002003004002001  label="De-Cap001"
  shape: bbox 100 x 26 x 50 mm, 25 faces (baked)
FEATURE [Part::Box] Box342  label="Krychle304"
  AttacherType = Attacher::AttachEngine3D
  Height = 48
  Length = 2
  Placement = pos=(-40.5,77,18.5) rot=(0,0,1;0rad)
  Width = 4
FEATURE [Part::MultiFuse] Fusion005043005007002094  label="Main008"
  Shapes = -> [Box339,Box335,Box336,Box337,Box342]
FEATURE [Part::Cut] Cut018020020009027020002003004004027014002  label="DE-Cap"
  Base = -> Fusion005043005007002094
  Tool = -> Fusion005043005007002095
FEATURE [Part::Fillet] Fillet004005003002003002003004002002  label="DE-Cap V2"
  Base = -> Cut018020020009027020002003004004027014002
  Edges = 6 edges r=1: [Edge6,Edge7,Edge8,Edge9,Edge16,Edge26]
FEATURE [Part::Feature] Fillet004005003002003002003004002002002001  label="DE-red"
  shape: bbox 62 x 92 x 55.5 mm, 183 faces (baked)
FEATURE [Part::Feature] Fillet004005003002003002003004002002002002  label="DE-Cap V004"
  shape: bbox 100 x 26 x 50 mm, 25 faces (baked)
FEATURE [Part::Feature] Cut005023015002007002039  label="Port16a012"
  Placement = pos=(17,-5,41.5) rot=(0,0,1;0rad)
  shape: bbox 14.5 x 15 x 16.4 mm, 6 faces (baked)
FEATURE [Part::Cylinder] Cylinder112024025003003006010004167  label="Válec900"
  Angle = 360
  AttacherType = Attacher::AttachEngine3D
  FirstAngle = 0
  Height = 10
  Placement = pos=(17,-9,43) rot=(1,0,0;1.5708rad)
  Radius = 11
  SecondAngle = 0
FEATURE [Part::Box] Box343  label="Krychle305"
  AttacherType = Attacher::AttachEngine3D
  Height = 12
  Length = 62
  Placement = pos=(-2.5,-15,44) rot=(0,0,1;0rad)
  Width = 31
FEATURE [Part::MultiFuse] Fusion005043005007002089  label="dec"
  Shapes = -> [Fusion005043005007002071,Box326,Box343]
FEATURE [Part::Box] Box344  label="Krychle306"
  AttacherType = Attacher::AttachEngine3D
  Height = 12
  Length = 58
  Placement = pos=(-0.5,-13,44) rot=(0,0,1;0rad)
  Width = 29
FEATURE [Part::Box] Box345  label="Krychle307"
  AttacherType = Attacher::AttachEngine3D
  Height = 12
  Length = 62
  Placement = pos=(-2.5,-15,44) rot=(0,0,1;0rad)
  Width = 31
FEATURE [Part::Box] Box346  label="Krychle308"
  AttacherType = Attacher::AttachEngine3D
  Height = 12
  Length = 58
  Placement = pos=(-0.5,-13,44) rot=(0,0,1;0rad)
  Width = 29
FEATURE [App::Part] Part005
  Origin = -> Origin005
FEATURE [Part::Feature] Cut018020020009027020002003004004027014003  label="Port16a013"
  Placement = pos=(17,-5,43) rot=(0,0,1;0rad)
  shape: bbox 14.5 x 15 x 16.4 mm, 6 faces (baked)
FEATURE [Part::Feature] Fillet009001  label="DEC vicko004"
  Placement = pos=(28.5,67,52) rot=(-1,0,0;1.5708rad)
  shape: bbox 62 x 31 x 10 mm, 160 faces (baked)
FEATURE [App::Part] Part002  label="Fin"
  Group = -> [Cylinder014005808,Box206,Box205,Cylinder014005804,Cylinder014005807,Cylinder014005806,Fusion,Cylinder014005805,Fusion001089078,Screw010,Cut,Fusion001089085,Cut005023015002010,Cut005023015002009,Cut005023015002008,Cut005023015002012,Cut005023015002011,Cylinder014005823,Cylinder014005826,Box224,Cylinder014005828,Cylinder014005829,Cylinder014005821,Box220,Box221,Box226,Cylinder014005820,+282 more]
  Origin = -> Origin002
FEATURE [Part::Cylinder] Cylinder112024025003003006010004168  label="Válec901"
  Angle = 360
  AttacherType = Attacher::AttachEngine3D
  FirstAngle = 0
  Height = 70
  Placement = pos=(-8,7,52.5) rot=(0,1,0;1.5708rad)
  Radius = 0.75
  SecondAngle = 0
FEATURE [Part::Cylinder] Cylinder112024025003003006010004169  label="Válec902"
  Angle = 360
  AttacherType = Attacher::AttachEngine3D
  FirstAngle = 0
  Height = 70
  Placement = pos=(-8,-7,52.5) rot=(0,1,0;1.5708rad)
  Radius = 0.75
  SecondAngle = 0
FEATURE [Part::Cylinder] Cylinder112024025003003006010004170  label="Válec903"
  Angle = 360
  AttacherType = Attacher::AttachEngine3D
  FirstAngle = 0
  Height = 70
  Placement = pos=(-8,7,52.5) rot=(0,1,0;1.5708rad)
  Radius = 0.75
  SecondAngle = 0
FEATURE [Part::Cylinder] Cylinder112024025003003006010004171  label="Válec904"
  Angle = 360
  AttacherType = Attacher::AttachEngine3D
  FirstAngle = 0
  Height = 70
  Placement = pos=(-8,-7,52.5) rot=(0,1,0;1.5708rad)
  Radius = 0.75
  SecondAngle = 0
FEATURE [Part::MultiFuse] Fusion005043005007002088  label="dirky kryt001"
  Shapes = -> [Cylinder112024025003003006010004149,Cylinder112024025003003006010004147,Cylinder112024025003003006010004148,Cylinder112024025003003006010004150,Box344,Cut018020020009027020002003004004027014003,Cylinder112024025003003006010004170,Cylinder112024025003003006010004171]
FEATURE [Part::Cut] Cut018020020009027020002003004004027013  label="Dec-red"
  Base = -> Fusion005043005007002089
  Tool = -> Fusion005043005007002088
FEATURE [Part::Fillet] Fillet004005003002003002003004002002002003  label="Dec red V5"
  Base = -> Cut018020020009027020002003004004027013
  Edges = 10 edges r=2: [Edge6,Edge27,Edge30,Edge37,Edge39,Edge43,Edge93,Edge103,Edge157,Edge241]
FEATURE [Part::Feature] Fillet004005003002003002003004002002002003001  label="Dec red GX16-4"
  shape: bbox 62 x 92 x 55.5 mm, 188 faces (baked)
FEATURE [Part::FeaturePython] Screw028  label="M4x25-Screw010"  # Fasteners workbench fastener (typed FeaturePython)
  Placement = pos=(47.5,49,45) rot=(0,-1,0;1.5708rad)
  diameter = 6
  invert = false
  length = 0
  matchOuter = false
  offset = 0
  thread = false
  type = 13
FEATURE [Part::FeaturePython] Screw029  label="M6x12-Screw010"  # Fasteners workbench fastener (typed FeaturePython)
  Placement = pos=(6.5,32.5,20.5) rot=(1,0,0;0rad)
  diameter = 8
  invert = false
  length = 0
  matchOuter = false
  offset = 0
  thread = false
  type = 14
FEATURE [Part::FeaturePython] Screw030  label="M6x12-Screw011"  # Fasteners workbench fastener (typed FeaturePython)
  Placement = pos=(6.5,32.5,21.5) rot=(1,0,0;0rad)
  diameter = 8
  invert = false
  length = 0
  matchOuter = false
  offset = 0
  thread = false
  type = 14
FEATURE [Part::Part2DObjectPython] ShapeString028  # Draft 2D object (typed FeaturePython)
  FontFile = <path>
  Placement = pos=(15.3452,-2,30.5072) rot=(1,0,0;1.5708rad)
  Size = 0.01
  String = .
  Tracking = 0
FEATURE [Part::Part2DObjectPython] ShapeString029  # Draft 2D object (typed FeaturePython)
  FontFile = <path>
  Placement = pos=(15.3452,-2,30.5072) rot=(1,0,0;1.5708rad)
  Size = 4
  String = RA
  Tracking = 0
FEATURE [Part::Extrusion] Extrude098  label="Text RA008"
  Base = -> ShapeString029
  Dir = (0,-1,0)
  DirMode = 2
  FaceMakerClass = Part::FaceMakerBullseye
  LengthFwd = 1
  LengthRev = 0
  Placement = pos=(7,0.4,-32) rot=(0,0,1;0rad)
  Solid = false
  Symmetric = false
FEATURE [Part::Box] Box347  label="konektor007"
  AttacherType = Attacher::AttachEngine3D
  Height = 29
  Length = 10
  Placement = pos=(50,16,37) rot=(0,0,1;0rad)
  Width = 12
FEATURE [Part::Box] Box348  label="Krychle309"
  AttacherType = Attacher::AttachEngine3D
  Height = 26
  Length = 58
  Placement = pos=(-0.5,0,-3) rot=(0,0,1;0rad)
  Width = 29
FEATURE [Part::Cylinder] Cylinder112024025003003006010004172  label="Válec905"
  Angle = 360
  AttacherType = Attacher::AttachEngine3D
  FirstAngle = 0
  Height = 10
  Placement = pos=(39,64,29.5) rot=(1,0,0;1.5708rad)
  Radius = 1.65
  SecondAngle = 0
FEATURE [Part::Cylinder] Cylinder112024025003003006010004173  label="Válec906"
  Angle = 360
  AttacherType = Attacher::AttachEngine3D
  FirstAngle = 0
  Height = 20
  Placement = pos=(23.5,64,45) rot=(1,0,0;1.5708rad)
  Radius = 12.5
  SecondAngle = 0
FEATURE [Part::Box] Box349  label="Krychle310"
  AttacherType = Attacher::AttachEngine3D
  Height = 43
  Length = 65
  Placement = pos=(-5,15.5,49.5) rot=(1,0,0;0.523599rad)
  Width = 48
FEATURE [Part::Cylinder] Cylinder112024025003003006010004174  label="Válec907"
  Angle = 360
  AttacherType = Attacher::AttachEngine3D
  FirstAngle = 0
  Height = 20
  Placement = pos=(23.5,64,45) rot=(1,0,0;1.5708rad)
  Radius = 12.5
  SecondAngle = 0
FEATURE [Part::Cylinder] Cylinder112024025003003006010004175  label="Válec908"
  Angle = 360
  AttacherType = Attacher::AttachEngine3D
  FirstAngle = 0
  Height = 10
  Placement = pos=(52,31,16.5) rot=(0,1,0;1.5708rad)
  Radius = 1.65
  SecondAngle = 0
FEATURE [Part::Box] Box350  label="Krychle311"
  AttacherType = Attacher::AttachEngine3D
  Height = 3.3
  Length = 4
  Placement = pos=(8,56,58.85) rot=(0,0,1;0rad)
  Width = 8
FEATURE [Part::Box] Box351  label="Krychle312"
  AttacherType = Attacher::AttachEngine3D
  Height = 3.3
  Length = 4
  Placement = pos=(8,56,27.85) rot=(0,0,1;0rad)
  Width = 8
FEATURE [Part::Box] Box352  label="Krychle313"
  AttacherType = Attacher::AttachEngine3D
  Height = 43
  Length = 4
  Placement = pos=(55.5,16,23) rot=(0,0,1;0rad)
  Width = 40
FEATURE [Part::Cylinder] Cylinder112024025003003006010004176  label="Válec909"
  Angle = 360
  AttacherType = Attacher::AttachEngine3D
  FirstAngle = 0
  Height = 10
  Placement = pos=(39,64,60.5) rot=(1,0,0;1.5708rad)
  Radius = 1.65
  SecondAngle = 0
FEATURE [Part::Box] Box353  label="Krychle314"
  AttacherType = Attacher::AttachEngine3D
  Height = 3.3
  Length = 4
  Placement = pos=(39,56,58.85) rot=(0,0,1;0rad)
  Width = 8
FEATURE [Part::Box] Box354  label="Krychle315"
  AttacherType = Attacher::AttachEngine3D
  Height = 3.3
  Length = 4
  Placement = pos=(39,56,27.85) rot=(0,0,1;0rad)
  Width = 8
FEATURE [Part::Extrusion] Extrude099  label="Text TR008"
  Base = -> ShapeString028
  Dir = (0,-1,0)
  DirMode = 2
  FaceMakerClass = Part::FaceMakerBullseye
  LengthFwd = 1
  LengthRev = 0
  Placement = pos=(-6.75,1,-33) rot=(0,0,1;0rad)
  Solid = false
  Symmetric = false
FEATURE [Part::Cylinder] Cylinder112024025003003006010004177  label="Válec910"
  Angle = 360
  AttacherType = Attacher::AttachEngine3D
  FirstAngle = 0
  Height = 8
  Placement = pos=(3.5,6,0) rot=(0,0,1;0rad)
  Radius = 0.7
  SecondAngle = 0
FEATURE [Part::Cylinder] Cylinder112024025003003006010004178  label="Válec911"
  Angle = 360
  AttacherType = Attacher::AttachEngine3D
  FirstAngle = 0
  Height = 10
  Placement = pos=(39,64,60.5) rot=(1,0,0;1.5708rad)
  Radius = 1.65
  SecondAngle = 0
FEATURE [Part::Cylinder] Cylinder112024025003003006010004179  label="Válec912"
  Angle = 360
  AttacherType = Attacher::AttachEngine3D
  FirstAngle = 0
  Height = 10
  Placement = pos=(8,64,29.5) rot=(1,0,0;1.5708rad)
  Radius = 1.65
  SecondAngle = 0
FEATURE [Part::Box] Box355  label="Krychle316"
  AttacherType = Attacher::AttachEngine3D
  Height = 43
  Length = 59.5
  Placement = pos=(0,56,23) rot=(0,0,1;0rad)
  Width = 7
FEATURE [Part::Cylinder] Cylinder112024025003003006010004180  label="Válec913"
  Angle = 360
  AttacherType = Attacher::AttachEngine3D
  FirstAngle = 0
  Height = 6.5
  Placement = pos=(53.5,21.25,0) rot=(0,0,1;0rad)
  Radius = 3.5
  SecondAngle = 0
FEATURE [Part::Cylinder] Cylinder112024025003003006010004181  label="Válec914"
  Angle = 360
  AttacherType = Attacher::AttachEngine3D
  FirstAngle = 0
  Height = 10
  Placement = pos=(8,64,60.5) rot=(1,0,0;1.5708rad)
  Radius = 1.65
  SecondAngle = 0
FEATURE [Part::MultiFuse] Fusion005043005007002101
  Shapes = -> [Extrude099,Extrude098]
FEATURE [Part::Feature] Fusion005043005007002109  label="Imbus016"
  Placement = pos=(31,0,31) rot=(0,0,1;0rad)
  shape: bbox 10.4 x 3 x 6.4 mm, 6 faces (baked)
FEATURE [Part::Feature] Fusion005043005007002110  label="Imbus017"
  Placement = pos=(31,0,0) rot=(0,0,1;0rad)
  shape: bbox 10.4 x 3 x 6.4 mm, 6 faces (baked)
FEATURE [Part::Feature] Fusion005043005007002111  label="Imbus018"
  Placement = pos=(0,0,31) rot=(0,0,1;0rad)
  shape: bbox 10.4 x 3 x 6.4 mm, 6 faces (baked)
FEATURE [Part::Box] Box356  label="Krychle317"
  AttacherType = Attacher::AttachEngine3D
  Height = 8
  Length = 6
  Placement = pos=(53.5,22.5,13.5) rot=(0,0,1;0rad)
  Width = 20
FEATURE [Part::Box] Box357  label="Krychle318"
  AttacherType = Attacher::AttachEngine3D
  Height = 6.4
  Length = 4
  Placement = pos=(8,60,26.3) rot=(0,0,1;0rad)
  Width = 3
FEATURE [Part::Cylinder] Cylinder112024025003003006010004182  label="Válec915"
  Angle = 360
  AttacherType = Attacher::AttachEngine3D
  FirstAngle = 0
  Height = 8
  Placement = pos=(53.5,21.25,0) rot=(0,0,1;0rad)
  Radius = 0.75
  SecondAngle = 0
FEATURE [Part::Cylinder] Cylinder112024025003003006010004183  label="Válec916"
  Angle = 360
  AttacherType = Attacher::AttachEngine3D
  FirstAngle = 0
  Height = 10
  Placement = pos=(3,60,58) rot=(0,0,1;0rad)
  Radius = 0.8
  SecondAngle = 0
FEATURE [Part::Box] Box358  label="Krychle319"
  AttacherType = Attacher::AttachEngine3D
  Height = 28
  Length = 62
  Placement = pos=(-2.5,-2,-5) rot=(0,0,1;0rad)
  Width = 31
FEATURE [Part::Cut] Cut018020020009027020002003004004027014007  label="Základ008"
  Base = -> Box358
  Tool = -> Box348
FEATURE [Part::Cylinder] Cylinder112024025003003006010004184  label="Válec917"
  Angle = 360
  AttacherType = Attacher::AttachEngine3D
  FirstAngle = 0
  Height = 6.5
  Placement = pos=(3.5,21.25,0) rot=(0,0,1;0rad)
  Radius = 3.5
  SecondAngle = 0
FEATURE [Part::Cylinder] Cylinder112024025003003006010004185  label="Válec918"
  Angle = 360
  AttacherType = Attacher::AttachEngine3D
  FirstAngle = 0
  Height = 3
  Placement = pos=(12,63,29.5) rot=(1,0,0;1.5708rad)
  Radius = 3.2
  SecondAngle = 0
FEATURE [Part::Cylinder] Cylinder112024025003003006010004186  label="Válec919"
  Angle = 360
  AttacherType = Attacher::AttachEngine3D
  FirstAngle = 0
  Height = 8
  Placement = pos=(53.5,6,0) rot=(0,0,1;0rad)
  Radius = 0.75
  SecondAngle = 0
FEATURE [Part::Box] Box359  label="Krychle320"
  AttacherType = Attacher::AttachEngine3D
  Height = 5
  Length = 62
  Placement = pos=(-2.5,-15,20.5) rot=(0,0,1;0rad)
  Width = 92
FEATURE [Part::Box] Box360  label="Krychle321"
  AttacherType = Attacher::AttachEngine3D
  Height = 25
  Length = 4
  Placement = pos=(23.5,56,32.5) rot=(0,0,1;0rad)
  Width = 8
FEATURE [Part::Cylinder] Cylinder112024025003003006010004187  label="Válec920"
  Angle = 360
  AttacherType = Attacher::AttachEngine3D
  FirstAngle = 0
  Height = 70
  Placement = pos=(-5,20,16.5) rot=(0,1,0;1.5708rad)
  Radius = 1
  SecondAngle = 0
FEATURE [Part::Cylinder] Cylinder112024025003003006010004188  label="Válec921"
  Angle = 360
  AttacherType = Attacher::AttachEngine3D
  FirstAngle = 0
  Height = 70
  Placement = pos=(-5,6,16.5) rot=(0,1,0;1.5708rad)
  Radius = 1
  SecondAngle = 0
FEATURE [Part::MultiFuse] Fusion005043005007002106  label="Horni diry017"
  Placement = pos=(0,0,3) rot=(0,0,1;0rad)
  Shapes = -> [Cylinder112024025003003006010004187,Cylinder112024025003003006010004188]
FEATURE [Part::Cylinder] Cylinder112024025003003006010004189  label="Válec922"
  Angle = 360
  AttacherType = Attacher::AttachEngine3D
  FirstAngle = 0
  Height = 5
  Placement = pos=(14.25,1,9.5) rot=(1,0,0;1.5708rad)
  Radius = 0.01
  SecondAngle = 0
FEATURE [Part::Cylinder] Cylinder112024025003003006010004190  label="Válec923"
  Angle = 360
  AttacherType = Attacher::AttachEngine3D
  FirstAngle = 0
  Height = 10
  Placement = pos=(52,37,16.5) rot=(0,1,0;1.5708rad)
  Radius = 1.65
  SecondAngle = 0
FEATURE [Part::Cylinder] Cylinder112024025003003006010004191  label="Válec924"
  Angle = 360
  AttacherType = Attacher::AttachEngine3D
  FirstAngle = 0
  Height = 10
  Placement = pos=(39,64,29.5) rot=(1,0,0;1.5708rad)
  Radius = 1.65
  SecondAngle = 0
FEATURE [Part::Box] Box361  label="Krychle322"
  AttacherType = Attacher::AttachEngine3D
  Height = 8
  Length = 26
  Placement = pos=(22.5,22.5,13.5) rot=(0,0,1;0rad)
  Width = 20
FEATURE [Part::Cylinder] Cylinder112024025003003006010004192  label="Válec925"
  Angle = 360
  AttacherType = Attacher::AttachEngine3D
  FirstAngle = 0
  Height = 10
  Placement = pos=(8,64,29.5) rot=(1,0,0;1.5708rad)
  Radius = 1.65
  SecondAngle = 0
FEATURE [Part::MultiFuse] Fusion005043005007002103
  Placement = pos=(4,0,0) rot=(0,0,1;0rad)
  Shapes = -> [Cylinder112024025003003006010004192,Cylinder112024025003003006010004181,Cylinder112024025003003006010004178,Cylinder112024025003003006010004173,Cylinder112024025003003006010004191]
FEATURE [Part::Cylinder] Cylinder112024025003003006010004193  label="Válec926"
  Angle = 360
  AttacherType = Attacher::AttachEngine3D
  FirstAngle = 0
  Height = 6.5
  Placement = pos=(3.5,6,0) rot=(0,0,1;0rad)
  Radius = 3.5
  SecondAngle = 0
FEATURE [Part::Cylinder] Cylinder112024025003003006010004194  label="Válec927"
  Angle = 360
  AttacherType = Attacher::AttachEngine3D
  FirstAngle = 0
  Height = 6.5
  Placement = pos=(53.5,6,0) rot=(0,0,1;0rad)
  Radius = 3.5
  SecondAngle = 0
FEATURE [Part::MultiFuse] Fusion005043005007002108  label="sloupky011"
  Placement = pos=(0,0,-3.5) rot=(0,0,1;0rad)
  Shapes = -> [Cylinder112024025003003006010004184,Cylinder112024025003003006010004193,Cylinder112024025003003006010004180,Cylinder112024025003003006010004194]
FEATURE [Part::MultiFuse] Fusion005043005007002104  label="bez der008"
  Shapes = -> [Cut018020020009027020002003004004027014007,Fusion005043005007002108]
FEATURE [Part::Box] Box362  label="Krychle323"
  AttacherType = Attacher::AttachEngine3D
  Height = 8
  Length = 24
  Placement = pos=(-1.5,12.5,13.5) rot=(0,0,1;0rad)
  Width = 40
FEATURE [Part::MultiFuse] Fusion005043005007002100  label="spodek006"
  Shapes = -> [Box359,Box356,Box362,Box361]
FEATURE [Part::Cylinder] Cylinder112024025003003006010004195  label="Válec928"
  Angle = 360
  AttacherType = Attacher::AttachEngine3D
  FirstAngle = 0
  Height = 8
  Placement = pos=(3.5,21.25,0) rot=(0,0,1;0rad)
  Radius = 0.75
  SecondAngle = 0
FEATURE [Part::MultiFuse] Fusion005043005007002107  label="diry031"
  Placement = pos=(0,0,-4) rot=(0,0,1;0rad)
  Shapes = -> [Cylinder112024025003003006010004195,Cylinder112024025003003006010004177,Cylinder112024025003003006010004182,Cylinder112024025003003006010004186]
FEATURE [Part::Cylinder] Cylinder112024025003003006010004196  label="Válec929"
  Angle = 360
  AttacherType = Attacher::AttachEngine3D
  FirstAngle = 0
  Height = 10
  Placement = pos=(8,64,60.5) rot=(1,0,0;1.5708rad)
  Radius = 1.65
  SecondAngle = 0
FEATURE [Part::Box] Box363  label="RJ062"
  AttacherType = Attacher::AttachEngine3D
  Height = 13
  Length = 16
  Placement = pos=(32,-5,4.5) rot=(0,0,1;0rad)
  Width = 18.5
FEATURE [Part::MultiFuse] Fusion005043005007002102  label="RJ a LED008"
  Shapes = -> [Box363,Cylinder112024025003003006010004189]
FEATURE [Part::MultiFuse] Fusion005043005007002099
  Shapes = -> [Fusion005043005007002107,Fusion005043005007002102,Fusion005043005007002106]
FEATURE [Part::Cut] Cut018020020009027020002003004004027014005
  Base = -> Fusion005043005007002104
  Tool = -> Fusion005043005007002099
FEATURE [Part::Cut] Cut018020020009027020002003004004027014006  label="PCB006"
  Base = -> Cut018020020009027020002003004004027014005
  Placement = pos=(0,-13,26) rot=(1,0,0;0rad)
  Tool = -> Fusion005043005007002101
FEATURE [Part::Box] Box364  label="Krychle324"
  AttacherType = Attacher::AttachEngine3D
  Height = 3.3
  Length = 10
  Placement = pos=(52,31,14.85) rot=(0,0,1;0rad)
  Width = 6
FEATURE [Part::MultiFuse] Fusion005043005007002105  label="Diryspodek003"
  Shapes = -> [Box364,Cylinder112024025003003006010004175,Cylinder112024025003003006010004190,Screw029,Screw030]
FEATURE [Part::Cut] Cut018020020009027020002003004004027014004  label="Spodek003"
  Base = -> Fusion005043005007002100
  Placement = pos=(0,0,-2) rot=(0,0,1;0rad)
  Tool = -> Fusion005043005007002105
FEATURE [Part::Cylinder] Cylinder112024025003003006010004197  label="Válec930"
  Angle = 360
  AttacherType = Attacher::AttachEngine3D
  FirstAngle = 0
  Height = 3
  Placement = pos=(8,63,29.5) rot=(1,0,0;1.5708rad)
  Radius = 3.2
  SecondAngle = 0
FEATURE [Part::MultiFuse] Fusion005043005007002114  label="Imbus019"
  Shapes = -> [Cylinder112024025003003006010004185,Cylinder112024025003003006010004197,Box357]
FEATURE [Part::MultiFuse] Fusion005043005007002098  label="diry030"
  Placement = pos=(0,0,0.5) rot=(0,0,1;0rad)
  Shapes = -> [Cylinder112024025003003006010004179,Cylinder112024025003003006010004174,Cylinder112024025003003006010004196,Cylinder112024025003003006010004172,Cylinder112024025003003006010004176,Screw028,Fusion005043005007002103,Box360,Box351,Box353,Box354,Box350,Box347,Box349,Fusion005043005007002114,Fusion005043005007002110,Fusion005043005007002109,Fusion005043005007002111]
FEATURE [Part::Box] Box365  label="Krychle325"
  AttacherType = Attacher::AttachEngine3D
  Height = 43
  Length = 2.5
  Placement = pos=(-2.5,16,23) rot=(0,0,1;0rad)
  Width = 47
FEATURE [Part::MultiFuse] Fusion005043005007002112  label="Main009"
  Placement = pos=(0,0,0.5) rot=(0,0,1;0rad)
  Shapes = -> [Box355,Box352,Box365]
FEATURE [Part::Cut] Cut018020020009027020002003004004027014009  label="RA004"
  Base = -> Fusion005043005007002112
  Tool = -> Fusion005043005007002098
FEATURE [Part::Box] Box366  label="Krychle326"
  AttacherType = Attacher::AttachEngine3D
  Height = 8
  Length = 62
  Placement = pos=(-2.5,63,18.5) rot=(0,0,1;0rad)
  Width = 14
FEATURE [Part::MultiFuse] Fusion005043005007002097  label="Raxxx002"
  Shapes = -> [Cut018020020009027020002003004004027014006,Cut018020020009027020002003004004027014004,Cut018020020009027020002003004004027014009,Box366,Box345]
FEATURE [Part::Cylinder] Cylinder112024025003003006010004198  label="Válec931"
  Angle = 360
  AttacherType = Attacher::AttachEngine3D
  FirstAngle = 0
  Height = 10
  Placement = pos=(55,60,58) rot=(0,0,1;0rad)
  Radius = 0.8
  SecondAngle = 0
FEATURE [Part::Cylinder] Cylinder112024025003003006010004199  label="Válec932"
  Angle = 360
  AttacherType = Attacher::AttachEngine3D
  FirstAngle = 0
  Height = 10
  Placement = pos=(52,78,22.5) rot=(1,0,0;1.5708rad)
  Radius = 1.75
  SecondAngle = 0
FEATURE [Part::Cylinder] Cylinder112024025003003006010004200  label="Válec933"
  Angle = 360
  AttacherType = Attacher::AttachEngine3D
  FirstAngle = 0
  Height = 10
  Placement = pos=(4,78,22.5) rot=(1,0,0;1.5708rad)
  Radius = 1.75
  SecondAngle = 0
FEATURE [Part::MultiFuse] Fusion005043005007002113  label="dirky kryt005"
  Shapes = -> [Cylinder112024025003003006010004183,Cylinder112024025003003006010004198,Cylinder112024025003003006010004199,Cylinder112024025003003006010004200,Box346,Cylinder112024025003003006010004168,Cylinder112024025003003006010004169,Cut005023015002007002039]
FEATURE [Part::Cut] Cut018020020009027020002003004004027014008
  Base = -> Fusion005043005007002097
  Tool = -> Fusion005043005007002113
FEATURE [Part::Fillet] Fillet004005003002003002003004002002002003002  label="Ra Red V5"
  Base = -> Cut018020020009027020002003004004027014008
  Edges = 10 edges r=2: [Edge5,Edge24,Edge27,Edge68,Edge70,Edge72,Edge76,Edge154,Edge197,Edge293]
FEATURE [Part::Feature] Fillet004005003002003002003004002002002003002001  label="Ra Red EQ-GX16-4"
  shape: bbox 62 x 92 x 55 mm, 185 faces (baked)
FEATURE [App::Part] Part004  label="Red edition"
  Group = -> [Fillet004005003002003002001,Cylinder112024025003003006010004153,Cylinder112024025003003006010004151,Cylinder112024025003003006010004152,Cylinder112024025003003006010004154,ShapeString024,ShapeString025,Screw022,Screw023,Screw024,Cut018020020009027020002003004004027004,Cut018020020009027020002003004004027006,Cut018020020009027020002003004004027007,Cut018020020009027020002003004004027005,+296 more]
  Origin = -> Origin004
FEATURE [Part::FeaturePython] Screw031  label="M4x25-Screw011"  # Fasteners workbench fastener (typed FeaturePython)
  Placement = pos=(47.5,49,45) rot=(0,-1,0;1.5708rad)
  diameter = 6
  invert = false
  length = 0
  matchOuter = false
  offset = 0
  thread = false
  type = 13
FEATURE [Part::FeaturePython] Screw032  label="M6x12-Screw012"  # Fasteners workbench fastener (typed FeaturePython)
  Placement = pos=(6.5,32.5,20.5) rot=(1,0,0;0rad)
  diameter = 8
  invert = false
  length = 0
  matchOuter = false
  offset = 0
  thread = false
  type = 14
FEATURE [Part::FeaturePython] Screw033  label="M6x12-Screw013"  # Fasteners workbench fastener (typed FeaturePython)
  Placement = pos=(6.5,32.5,21.5) rot=(1,0,0;0rad)
  diameter = 8
  invert = false
  length = 0
  matchOuter = false
  offset = 0
  thread = false
  type = 14
FEATURE [Part::Feature] Fusion005043005007002115  label="Imbus020"
  Placement = pos=(31,0,0) rot=(0,0,1;0rad)
  shape: bbox 10.4 x 3 x 6.4 mm, 6 faces (baked)
FEATURE [Part::Feature] Fusion005043005007002116  label="Imbus021"
  Placement = pos=(0,0,31) rot=(0,0,1;0rad)
  shape: bbox 10.4 x 3 x 6.4 mm, 6 faces (baked)
FEATURE [Part::Feature] Cut018020020009027020002003004004027014010  label="Port16a014"
  Placement = pos=(50,0,39.5) rot=(0,0,1;1.5708rad)
  shape: bbox 15 x 14.5 x 16.4 mm, 6 faces (baked)
FEATURE [Part::Feature] Fusion005043005007002117  label="Imbus022"
  Placement = pos=(31,0,31) rot=(0,0,1;0rad)
  shape: bbox 10.4 x 3 x 6.4 mm, 6 faces (baked)
FEATURE [Part::Part2DObjectPython] ShapeString030  # Draft 2D object (typed FeaturePython)
  FontFile = <path>
  Placement = pos=(15.3452,-2,30.5072) rot=(1,0,0;1.5708rad)
  Size = 4
  String = RA
  Tracking = 0
FEATURE [Part::Part2DObjectPython] ShapeString031  # Draft 2D object (typed FeaturePython)
  FontFile = <path>
  Placement = pos=(15.3452,-2,30.5072) rot=(1,0,0;1.5708rad)
  Size = 0.01
  String = .
  Tracking = 0
FEATURE [Part::Box] Box367  label="Krychle327"
  AttacherType = Attacher::AttachEngine3D
  Height = 12
  Length = 62
  Placement = pos=(-2.5,-15,44) rot=(0,0,1;0rad)
  Width = 31
FEATURE [Part::Box] Box368  label="Krychle328"
  AttacherType = Attacher::AttachEngine3D
  Height = 12
  Length = 58
  Placement = pos=(-0.5,-13,44) rot=(0,0,1;0rad)
  Width = 29
FEATURE [Part::Cylinder] Cylinder112024025003003006010004201  label="Válec934"
  Angle = 360
  AttacherType = Attacher::AttachEngine3D
  FirstAngle = 0
  Height = 70
  Placement = pos=(-8,7,52.5) rot=(0,1,0;1.5708rad)
  Radius = 0.75
  SecondAngle = 0
FEATURE [Part::Cylinder] Cylinder112024025003003006010004202  label="Válec935"
  Angle = 360
  AttacherType = Attacher::AttachEngine3D
  FirstAngle = 0
  Height = 70
  Placement = pos=(-8,-7,52.5) rot=(0,1,0;1.5708rad)
  Radius = 0.75
  SecondAngle = 0
FEATURE [Part::Extrusion] Extrude100  label="Text RA009"
  Base = -> ShapeString030
  Dir = (0,-1,0)
  DirMode = 2
  FaceMakerClass = Part::FaceMakerBullseye
  LengthFwd = 1
  LengthRev = 0
  Placement = pos=(56.5,-7,-32) rot=(0,0,1;1.5708rad)
  Solid = false
  Symmetric = false
FEATURE [Part::Box] Box369  label="konektor008"
  AttacherType = Attacher::AttachEngine3D
  Height = 29
  Length = 10
  Placement = pos=(50,16,37) rot=(0,0,1;0rad)
  Width = 12
FEATURE [Part::Box] Box370  label="Krychle329"
  AttacherType = Attacher::AttachEngine3D
  Height = 28
  Length = 62
  Placement = pos=(-2.5,-2,-5) rot=(0,0,1;0rad)
  Width = 31
FEATURE [Part::Cylinder] Cylinder112024025003003006010004203  label="Válec936"
  Angle = 360
  AttacherType = Attacher::AttachEngine3D
  FirstAngle = 0
  Height = 10
  Placement = pos=(39,64,60.5) rot=(1,0,0;1.5708rad)
  Radius = 1.65
  SecondAngle = 0
FEATURE [Part::Box] Box371  label="Krychle330"
  AttacherType = Attacher::AttachEngine3D
  Height = 43
  Length = 65
  Placement = pos=(-5,15.5,49.5) rot=(1,0,0;0.523599rad)
  Width = 48
FEATURE [Part::Box] Box372  label="Krychle331"
  AttacherType = Attacher::AttachEngine3D
  Height = 3.3
  Length = 4
  Placement = pos=(8,56,58.85) rot=(0,0,1;0rad)
  Width = 8
FEATURE [Part::Box] Box373  label="Krychle332"
  AttacherType = Attacher::AttachEngine3D
  Height = 3.3
  Length = 4
  Placement = pos=(39,56,58.85) rot=(0,0,1;0rad)
  Width = 8
FEATURE [Part::Cylinder] Cylinder112024025003003006010004204  label="Válec937"
  Angle = 360
  AttacherType = Attacher::AttachEngine3D
  FirstAngle = 0
  Height = 8
  Placement = pos=(3.5,6,0) rot=(0,0,1;0rad)
  Radius = 0.7
  SecondAngle = 0
FEATURE [Part::Cylinder] Cylinder112024025003003006010004205  label="Válec938"
  Angle = 360
  AttacherType = Attacher::AttachEngine3D
  FirstAngle = 0
  Height = 10
  Placement = pos=(39,64,60.5) rot=(1,0,0;1.5708rad)
  Radius = 1.65
  SecondAngle = 0
FEATURE [Part::Box] Box374  label="Krychle333"
  AttacherType = Attacher::AttachEngine3D
  Height = 6.4
  Length = 4
  Placement = pos=(8,60,26.3) rot=(0,0,1;0rad)
  Width = 3
FEATURE [Part::Cylinder] Cylinder112024025003003006010004206  label="Válec939"
  Angle = 360
  AttacherType = Attacher::AttachEngine3D
  FirstAngle = 0
  Height = 70
  Placement = pos=(-5,6,16.5) rot=(0,1,0;1.5708rad)
  Radius = 1
  SecondAngle = 0
FEATURE [Part::Box] Box375  label="Krychle334"
  AttacherType = Attacher::AttachEngine3D
  Height = 8
  Length = 26
  Placement = pos=(22.5,22.5,13.5) rot=(0,0,1;0rad)
  Width = 20
FEATURE [Part::Box] Box376  label="Krychle335"
  AttacherType = Attacher::AttachEngine3D
  Height = 3.3
  Length = 4
  Placement = pos=(39,56,27.85) rot=(0,0,1;0rad)
  Width = 8
FEATURE [Part::Extrusion] Extrude101  label="Text TR009"
  Base = -> ShapeString031
  Dir = (0,-1,0)
  DirMode = 2
  FaceMakerClass = Part::FaceMakerBullseye
  LengthFwd = 1
  LengthRev = 0
  Placement = pos=(-6.75,1,-33) rot=(0,0,1;0rad)
  Solid = false
  Symmetric = false
FEATURE [Part::MultiFuse] Fusion005043005007002120
  Shapes = -> [Extrude101,Extrude100]
FEATURE [Part::Box] Box377  label="Krychle336"
  AttacherType = Attacher::AttachEngine3D
  Height = 3.3
  Length = 4
  Placement = pos=(8,56,27.85) rot=(0,0,1;0rad)
  Width = 8
FEATURE [Part::Cylinder] Cylinder112024025003003006010004207  label="Válec940"
  Angle = 360
  AttacherType = Attacher::AttachEngine3D
  FirstAngle = 0
  Height = 10
  Placement = pos=(39,64,29.5) rot=(1,0,0;1.5708rad)
  Radius = 1.65
  SecondAngle = 0
FEATURE [Part::Cylinder] Cylinder112024025003003006010004208  label="Válec941"
  Angle = 360
  AttacherType = Attacher::AttachEngine3D
  FirstAngle = 0
  Height = 10
  Placement = pos=(8,64,29.5) rot=(1,0,0;1.5708rad)
  Radius = 1.65
  SecondAngle = 0
FEATURE [Part::Cylinder] Cylinder112024025003003006010004209  label="Válec942"
  Angle = 360
  AttacherType = Attacher::AttachEngine3D
  FirstAngle = 0
  Height = 20
  Placement = pos=(23.5,64,45) rot=(1,0,0;1.5708rad)
  Radius = 12.5
  SecondAngle = 0
FEATURE [Part::Box] Box378  label="Krychle337"
  AttacherType = Attacher::AttachEngine3D
  Height = 43
  Length = 59.5
  Placement = pos=(0,56,23) rot=(0,0,1;0rad)
  Width = 7
FEATURE [Part::Cylinder] Cylinder112024025003003006010004210  label="Válec943"
  Angle = 360
  AttacherType = Attacher::AttachEngine3D
  FirstAngle = 0
  Height = 6.5
  Placement = pos=(53.5,21.25,0) rot=(0,0,1;0rad)
  Radius = 3.5
  SecondAngle = 0
FEATURE [Part::Cylinder] Cylinder112024025003003006010004211  label="Válec944"
  Angle = 360
  AttacherType = Attacher::AttachEngine3D
  FirstAngle = 0
  Height = 8
  Placement = pos=(53.5,21.25,0) rot=(0,0,1;0rad)
  Radius = 0.75
  SecondAngle = 0
FEATURE [Part::Cylinder] Cylinder112024025003003006010004212  label="Válec945"
  Angle = 360
  AttacherType = Attacher::AttachEngine3D
  FirstAngle = 0
  Height = 20
  Placement = pos=(23.5,64,45) rot=(1,0,0;1.5708rad)
  Radius = 12.5
  SecondAngle = 0
FEATURE [Part::Cylinder] Cylinder112024025003003006010004213  label="Válec946"
  Angle = 360
  AttacherType = Attacher::AttachEngine3D
  FirstAngle = 0
  Height = 10
  Placement = pos=(52,31,16.5) rot=(0,1,0;1.5708rad)
  Radius = 1.65
  SecondAngle = 0
FEATURE [Part::Box] Box379  label="Krychle338"
  AttacherType = Attacher::AttachEngine3D
  Height = 43
  Length = 4
  Placement = pos=(55.5,16,23) rot=(0,0,1;0rad)
  Width = 40
FEATURE [Part::Cylinder] Cylinder112024025003003006010004214  label="Válec947"
  Angle = 360
  AttacherType = Attacher::AttachEngine3D
  FirstAngle = 0
  Height = 10
  Placement = pos=(8,64,60.5) rot=(1,0,0;1.5708rad)
  Radius = 1.65
  SecondAngle = 0
FEATURE [Part::Cylinder] Cylinder112024025003003006010004215  label="Válec948"
  Angle = 360
  AttacherType = Attacher::AttachEngine3D
  FirstAngle = 0
  Height = 10
  Placement = pos=(3,60,58) rot=(0,0,1;0rad)
  Radius = 0.8
  SecondAngle = 0
FEATURE [Part::Box] Box380  label="Krychle339"
  AttacherType = Attacher::AttachEngine3D
  Height = 26
  Length = 58
  Placement = pos=(-0.5,0,-3) rot=(0,0,1;0rad)
  Width = 29
FEATURE [Part::Cut] Cut018020020009027020002003004004027014013  label="Základ009"
  Base = -> Box370
  Tool = -> Box380
FEATURE [Part::Box] Box381  label="Krychle340"
  AttacherType = Attacher::AttachEngine3D
  Height = 8
  Length = 6
  Placement = pos=(53.5,22.5,13.5) rot=(0,0,1;0rad)
  Width = 20
FEATURE [Part::Cylinder] Cylinder112024025003003006010004216  label="Válec949"
  Angle = 360
  AttacherType = Attacher::AttachEngine3D
  FirstAngle = 0
  Height = 6.5
  Placement = pos=(3.5,21.25,0) rot=(0,0,1;0rad)
  Radius = 3.5
  SecondAngle = 0
FEATURE [Part::Cylinder] Cylinder112024025003003006010004217  label="Válec950"
  Angle = 360
  AttacherType = Attacher::AttachEngine3D
  FirstAngle = 0
  Height = 3
  Placement = pos=(12,63,29.5) rot=(1,0,0;1.5708rad)
  Radius = 3.2
  SecondAngle = 0
FEATURE [Part::Cylinder] Cylinder112024025003003006010004218  label="Válec951"
  Angle = 360
  AttacherType = Attacher::AttachEngine3D
  FirstAngle = 0
  Height = 8
  Placement = pos=(53.5,6,0) rot=(0,0,1;0rad)
  Radius = 0.75
  SecondAngle = 0
FEATURE [Part::Box] Box382  label="Krychle341"
  AttacherType = Attacher::AttachEngine3D
  Height = 5
  Length = 62
  Placement = pos=(-2.5,-15,20.5) rot=(0,0,1;0rad)
  Width = 92
FEATURE [Part::Box] Box383  label="Krychle342"
  AttacherType = Attacher::AttachEngine3D
  Height = 25
  Length = 4
  Placement = pos=(23.5,56,32.5) rot=(0,0,1;0rad)
  Width = 8
FEATURE [Part::Cylinder] Cylinder112024025003003006010004219  label="Válec952"
  Angle = 360
  AttacherType = Attacher::AttachEngine3D
  FirstAngle = 0
  Height = 70
  Placement = pos=(-5,20,16.5) rot=(0,1,0;1.5708rad)
  Radius = 1
  SecondAngle = 0
FEATURE [Part::MultiFuse] Fusion005043005007002128  label="Horni diry018"
  Placement = pos=(0,0,3) rot=(0,0,1;0rad)
  Shapes = -> [Cylinder112024025003003006010004219,Cylinder112024025003003006010004206]
FEATURE [Part::Cylinder] Cylinder112024025003003006010004221  label="Válec954"
  Angle = 360
  AttacherType = Attacher::AttachEngine3D
  FirstAngle = 0
  Height = 10
  Placement = pos=(52,37,16.5) rot=(0,1,0;1.5708rad)
  Radius = 1.65
  SecondAngle = 0
FEATURE [Part::Cylinder] Cylinder112024025003003006010004222  label="Válec955"
  Angle = 360
  AttacherType = Attacher::AttachEngine3D
  FirstAngle = 0
  Height = 10
  Placement = pos=(39,64,29.5) rot=(1,0,0;1.5708rad)
  Radius = 1.65
  SecondAngle = 0
FEATURE [Part::Cylinder] Cylinder112024025003003006010004223  label="Válec956"
  Angle = 360
  AttacherType = Attacher::AttachEngine3D
  FirstAngle = 0
  Height = 6.5
  Placement = pos=(3.5,6,0) rot=(0,0,1;0rad)
  Radius = 3.5
  SecondAngle = 0
FEATURE [Part::Cylinder] Cylinder112024025003003006010004224  label="Válec957"
  Angle = 360
  AttacherType = Attacher::AttachEngine3D
  FirstAngle = 0
  Height = 6.5
  Placement = pos=(53.5,6,0) rot=(0,0,1;0rad)
  Radius = 3.5
  SecondAngle = 0
FEATURE [Part::MultiFuse] Fusion005043005007002122  label="sloupky012"
  Placement = pos=(0,0,-3.5) rot=(0,0,1;0rad)
  Shapes = -> [Cylinder112024025003003006010004216,Cylinder112024025003003006010004223,Cylinder112024025003003006010004210,Cylinder112024025003003006010004224]
FEATURE [Part::MultiFuse] Fusion005043005007002130  label="bez der009"
  Shapes = -> [Cut018020020009027020002003004004027014013,Fusion005043005007002122]
FEATURE [Part::Box] Box384  label="Krychle343"
  AttacherType = Attacher::AttachEngine3D
  Height = 8
  Length = 24
  Placement = pos=(-1.5,12.5,13.5) rot=(0,0,1;0rad)
  Width = 40
FEATURE [Part::MultiFuse] Fusion005043005007002119  label="spodek007"
  Shapes = -> [Box382,Box381,Box384,Box375]
FEATURE [Part::Cylinder] Cylinder112024025003003006010004225  label="Válec958"
  Angle = 360
  AttacherType = Attacher::AttachEngine3D
  FirstAngle = 0
  Height = 10
  Placement = pos=(8,64,60.5) rot=(1,0,0;1.5708rad)
  Radius = 1.65
  SecondAngle = 0
FEATURE [Part::Cylinder] Cylinder112024025003003006010004226  label="Válec959"
  Angle = 360
  AttacherType = Attacher::AttachEngine3D
  FirstAngle = 0
  Height = 8
  Placement = pos=(3.5,21.25,0) rot=(0,0,1;0rad)
  Radius = 0.75
  SecondAngle = 0
FEATURE [Part::MultiFuse] Fusion005043005007002129  label="diry033"
  Placement = pos=(0,0,-4) rot=(0,0,1;0rad)
  Shapes = -> [Cylinder112024025003003006010004226,Cylinder112024025003003006010004204,Cylinder112024025003003006010004211,Cylinder112024025003003006010004218]
FEATURE [Part::MultiFuse] Fusion005043005007002125
  Shapes = -> [Fusion005043005007002129,Fusion005043005007002128]
FEATURE [Part::Cut] Cut018020020009027020002003004004027014012
  Base = -> Fusion005043005007002130
  Tool = -> Fusion005043005007002125
FEATURE [Part::Cut] Cut018020020009027020002003004004027014011  label="PCB007"
  Base = -> Cut018020020009027020002003004004027014012
  Placement = pos=(0,-13,26) rot=(1,0,0;0rad)
  Tool = -> Fusion005043005007002120
FEATURE [Part::Box] Box386  label="Krychle344"
  AttacherType = Attacher::AttachEngine3D
  Height = 3.3
  Length = 10
  Placement = pos=(52,31,14.85) rot=(0,0,1;0rad)
  Width = 6
FEATURE [Part::MultiFuse] Fusion005043005007002124  label="Diryspodek004"
  Shapes = -> [Box386,Cylinder112024025003003006010004213,Cylinder112024025003003006010004221,Screw032,Screw033]
FEATURE [Part::Cut] Cut018020020009027020002003004004027014016  label="Spodek004"
  Base = -> Fusion005043005007002119
  Placement = pos=(0,0,-2) rot=(0,0,1;0rad)
  Tool = -> Fusion005043005007002124
FEATURE [Part::Cylinder] Cylinder112024025003003006010004227  label="Válec960"
  Angle = 360
  AttacherType = Attacher::AttachEngine3D
  FirstAngle = 0
  Height = 3
  Placement = pos=(8,63,29.5) rot=(1,0,0;1.5708rad)
  Radius = 3.2
  SecondAngle = 0
FEATURE [Part::MultiFuse] Fusion005043005007002131  label="Imbus023"
  Shapes = -> [Cylinder112024025003003006010004217,Cylinder112024025003003006010004227,Box374]
FEATURE [Part::Box] Box387  label="Krychle345"
  AttacherType = Attacher::AttachEngine3D
  Height = 8
  Length = 62
  Placement = pos=(-2.5,63,18.5) rot=(0,0,1;0rad)
  Width = 14
FEATURE [Part::Box] Box388  label="Krychle346"
  AttacherType = Attacher::AttachEngine3D
  Height = 43
  Length = 2.5
  Placement = pos=(-2.5,16,23) rot=(0,0,1;0rad)
  Width = 47
FEATURE [Part::MultiFuse] Fusion005043005007002123  label="Main010"
  Placement = pos=(0,0,0.5) rot=(0,0,1;0rad)
  Shapes = -> [Box378,Box379,Box388]
FEATURE [Part::Cylinder] Cylinder112024025003003006010004228  label="Válec961"
  Angle = 360
  AttacherType = Attacher::AttachEngine3D
  FirstAngle = 0
  Height = 10
  Placement = pos=(55,60,58) rot=(0,0,1;0rad)
  Radius = 0.8
  SecondAngle = 0
FEATURE [Part::Cylinder] Cylinder112024025003003006010004229  label="Válec962"
  Angle = 360
  AttacherType = Attacher::AttachEngine3D
  FirstAngle = 0
  Height = 10
  Placement = pos=(52,78,22.5) rot=(1,0,0;1.5708rad)
  Radius = 1.75
  SecondAngle = 0
FEATURE [Part::Cylinder] Cylinder112024025003003006010004230  label="Válec963"
  Angle = 360
  AttacherType = Attacher::AttachEngine3D
  FirstAngle = 0
  Height = 10
  Placement = pos=(4,78,22.5) rot=(1,0,0;1.5708rad)
  Radius = 1.75
  SecondAngle = 0
FEATURE [Part::MultiFuse] Fusion005043005007002132  label="dirky kryt006"
  Shapes = -> [Cylinder112024025003003006010004215,Cylinder112024025003003006010004228,Cylinder112024025003003006010004229,Cylinder112024025003003006010004230,Box368,Cylinder112024025003003006010004201,Cylinder112024025003003006010004202,Cut018020020009027020002003004004027014010]
FEATURE [Part::Cylinder] Cylinder112024025003003006010004231  label="Válec964"
  Angle = 360
  AttacherType = Attacher::AttachEngine3D
  FirstAngle = 0
  Height = 10
  Placement = pos=(8,64,29.5) rot=(1,0,0;1.5708rad)
  Radius = 1.65
  SecondAngle = 0
FEATURE [Part::MultiFuse] Fusion005043005007002127
  Placement = pos=(4,0,0) rot=(0,0,1;0rad)
  Shapes = -> [Cylinder112024025003003006010004231,Cylinder112024025003003006010004214,Cylinder112024025003003006010004205,Cylinder112024025003003006010004209,Cylinder112024025003003006010004222]
FEATURE [Part::MultiFuse] Fusion005043005007002118  label="diry032"
  Placement = pos=(0,0,0.5) rot=(0,0,1;0rad)
  Shapes = -> [Cylinder112024025003003006010004208,Cylinder112024025003003006010004212,Cylinder112024025003003006010004225,Cylinder112024025003003006010004207,Cylinder112024025003003006010004203,Screw031,Fusion005043005007002127,Box383,Box377,Box373,Box376,Box372,Box369,Box371,Fusion005043005007002131,Fusion005043005007002115,Fusion005043005007002117,Fusion005043005007002116]
FEATURE [Part::Cut] Cut018020020009027020002003004004027014015  label="RA005"
  Base = -> Fusion005043005007002123
  Tool = -> Fusion005043005007002118
FEATURE [Part::MultiFuse] Fusion005043005007002126  label="Raxxx003"
  Shapes = -> [Cut018020020009027020002003004004027014011,Cut018020020009027020002003004004027014016,Cut018020020009027020002003004004027014015,Box387,Box367]
FEATURE [Part::Cut] Cut018020020009027020002003004004027014014  label="RAv61"
  Base = -> Fusion005043005007002126
  Tool = -> Fusion005043005007002132
FEATURE [Part::Fillet] Fillet004005003002003002003004002002002003002002  label="RAv6"
  Base = -> Cut018020020009027020002003004004027014014
  Edges = 10 edges r=2: [Edge5,Edge24,Edge27,Edge68,Edge70,Edge72,Edge76,Edge154,Edge160,Edge162]
FEATURE [Part::FeaturePython] Screw034  label="M6x12-Screw014"  # Fasteners workbench fastener (typed FeaturePython)
  Placement = pos=(8.5,34,21.5) rot=(1,0,0;0rad)
  diameter = 8
  invert = false
  length = 0
  matchOuter = false
  offset = 0
  thread = false
  type = 14
FEATURE [Part::FeaturePython] Screw035  label="M6x12-Screw015"  # Fasteners workbench fastener (typed FeaturePython)
  Placement = pos=(8.5,34,20.5) rot=(1,0,0;0rad)
  diameter = 8
  invert = false
  length = 0
  matchOuter = false
  offset = 0
  thread = false
  type = 14
FEATURE [Part::FeaturePython] Screw036  label="M4x25-Screw012"  # Fasteners workbench fastener (typed FeaturePython)
  Placement = pos=(47.5,49,45) rot=(0,-1,0;1.5708rad)
  diameter = 6
  invert = false
  length = 0
  matchOuter = false
  offset = 0
  thread = false
  type = 13
FEATURE [Part::Feature] Cut018020020009027020002003004004027014021  label="Port16a015"
  Placement = pos=(17,-5,43) rot=(0,0,1;0rad)
  shape: bbox 14.5 x 15 x 16.4 mm, 6 faces (baked)
FEATURE [Part::Feature] Fusion005043005007002133  label="Imbus024"
  Placement = pos=(31,0,31) rot=(0,0,1;0rad)
  shape: bbox 10.4 x 3 x 6.4 mm, 6 faces (baked)
FEATURE [Part::Feature] Fusion005043005007002134  label="Imbus025"
  Placement = pos=(31,0,0) rot=(0,0,1;0rad)
  shape: bbox 10.4 x 3 x 6.4 mm, 6 faces (baked)
FEATURE [Part::Feature] Fusion005043005007002135  label="Imbus026"
  Placement = pos=(0,0,31) rot=(0,0,1;0rad)
  shape: bbox 10.4 x 3 x 6.4 mm, 6 faces (baked)
FEATURE [Part::MultiFuse] Fusion005043005007002140
  Shapes = -> [Screw034,Screw035]
FEATURE [Part::Cylinder] Cylinder112024025003003006010004232  label="Válec965"
  Angle = 360
  AttacherType = Attacher::AttachEngine3D
  FirstAngle = 0
  Height = 70
  Placement = pos=(-5,20,16.5) rot=(0,1,0;1.5708rad)
  Radius = 1
  SecondAngle = 0
FEATURE [Part::Cylinder] Cylinder112024025003003006010004233  label="Válec966"
  Angle = 360
  AttacherType = Attacher::AttachEngine3D
  FirstAngle = 0
  Height = 6.5
  Placement = pos=(53.5,21.25,0) rot=(0,0,1;0rad)
  Radius = 3.5
  SecondAngle = 0
FEATURE [Part::Cylinder] Cylinder112024025003003006010004234  label="Válec967"
  Angle = 360
  AttacherType = Attacher::AttachEngine3D
  FirstAngle = 0
  Height = 8
  Placement = pos=(53.5,21.25,0) rot=(0,0,1;0rad)
  Radius = 0.75
  SecondAngle = 0
FEATURE [Part::Box] Box390  label="Krychle347"
  AttacherType = Attacher::AttachEngine3D
  Height = 9
  Length = 26
  Placement = pos=(-2,24,13) rot=(0,0,1;0rad)
  Width = 20
FEATURE [Part::Cylinder] Cylinder112024025003003006010004235  label="Válec968"
  Angle = 360
  AttacherType = Attacher::AttachEngine3D
  FirstAngle = 0
  Height = 8
  Placement = pos=(3.5,6,0) rot=(0,0,1;0rad)
  Radius = 0.7
  SecondAngle = 0
FEATURE [Part::Cylinder] Cylinder112024025003003006010004236  label="Válec969"
  Angle = 360
  AttacherType = Attacher::AttachEngine3D
  FirstAngle = 0
  Height = 8
  Placement = pos=(53.5,6,0) rot=(0,0,1;0rad)
  Radius = 0.75
  SecondAngle = 0
FEATURE [Part::Box] Box391  label="Krychle348"
  AttacherType = Attacher::AttachEngine3D
  Height = 26
  Length = 58
  Placement = pos=(-0.5,0,-3) rot=(0,0,1;0rad)
  Width = 29
FEATURE [Part::Cylinder] Cylinder112024025003003006010004237  label="Válec970"
  Angle = 360
  AttacherType = Attacher::AttachEngine3D
  FirstAngle = 0
  Height = 3
  Placement = pos=(12,63,29.5) rot=(1,0,0;1.5708rad)
  Radius = 3.2
  SecondAngle = 0
FEATURE [Part::Box] Box392  label="Krychle349"
  AttacherType = Attacher::AttachEngine3D
  Height = 5
  Length = 62
  Placement = pos=(-2.5,-15,20.5) rot=(0,0,1;0rad)
  Width = 78
FEATURE [Part::MultiFuse] Fusion005043005007002145  label="spodek008"
  Shapes = -> [Box392,Box390]
FEATURE [Part::Cut] Cut018020020009027020002003004004027014018
  Base = -> Fusion005043005007002145
  Placement = pos=(0,0,-2) rot=(0,0,1;0rad)
  Tool = -> Fusion005043005007002140
FEATURE [Part::Cylinder] Cylinder112024025003003006010004238  label="Válec971"
  Angle = 360
  AttacherType = Attacher::AttachEngine3D
  FirstAngle = 0
  Height = 6.5
  Placement = pos=(53.5,6,0) rot=(0,0,1;0rad)
  Radius = 3.5
  SecondAngle = 0
FEATURE [Part::Cylinder] Cylinder112024025003003006010004239  label="Válec972"
  Angle = 360
  AttacherType = Attacher::AttachEngine3D
  FirstAngle = 0
  Height = 10
  Placement = pos=(8,64,29.5) rot=(1,0,0;1.5708rad)
  Radius = 1.65
  SecondAngle = 0
FEATURE [Part::Cylinder] Cylinder112024025003003006010004240  label="Válec973"
  Angle = 360
  AttacherType = Attacher::AttachEngine3D
  FirstAngle = 0
  Height = 10
  Placement = pos=(8,64,60.5) rot=(1,0,0;1.5708rad)
  Radius = 1.65
  SecondAngle = 0
FEATURE [Part::Cylinder] Cylinder112024025003003006010004241  label="Válec974"
  Angle = 360
  AttacherType = Attacher::AttachEngine3D
  FirstAngle = 0
  Height = 8
  Placement = pos=(3.5,21.25,0) rot=(0,0,1;0rad)
  Radius = 0.75
  SecondAngle = 0
FEATURE [Part::MultiFuse] Fusion005043005007002138  label="diry034"
  Placement = pos=(0,0,-4) rot=(0,0,1;0rad)
  Shapes = -> [Cylinder112024025003003006010004241,Cylinder112024025003003006010004235,Cylinder112024025003003006010004234,Cylinder112024025003003006010004236]
FEATURE [Part::Box] Box393  label="Krychle350"
  AttacherType = Attacher::AttachEngine3D
  Height = 25
  Length = 4
  Placement = pos=(23.5,56,32.5) rot=(0,0,1;0rad)
  Width = 8
FEATURE [Part::Box] Box394  label="Krychle351"
  AttacherType = Attacher::AttachEngine3D
  Height = 3.3
  Length = 4
  Placement = pos=(39,56,27.85) rot=(0,0,1;0rad)
  Width = 8
FEATURE [Part::Cylinder] Cylinder112024025003003006010004242  label="Válec975"
  Angle = 360
  AttacherType = Attacher::AttachEngine3D
  FirstAngle = 0
  Height = 10
  Placement = pos=(39,64,60.5) rot=(1,0,0;1.5708rad)
  Radius = 1.65
  SecondAngle = 0
FEATURE [Part::Cylinder] Cylinder112024025003003006010004243  label="Válec976"
  Angle = 360
  AttacherType = Attacher::AttachEngine3D
  FirstAngle = 0
  Height = 10
  Placement = pos=(8,64,29.5) rot=(1,0,0;1.5708rad)
  Radius = 1.65
  SecondAngle = 0
FEATURE [Part::Cylinder] Cylinder112024025003003006010004244  label="Válec977"
  Angle = 360
  AttacherType = Attacher::AttachEngine3D
  FirstAngle = 0
  Height = 10
  Placement = pos=(39,64,29.5) rot=(1,0,0;1.5708rad)
  Radius = 1.65
  SecondAngle = 0
FEATURE [Part::Box] Box395  label="Krychle352"
  AttacherType = Attacher::AttachEngine3D
  Height = 28
  Length = 62
  Placement = pos=(-2.5,-2,-5) rot=(0,0,1;0rad)
  Width = 31
FEATURE [Part::Cut] Cut018020020009027020002003004004027014020  label="Základ010"
  Base = -> Box395
  Tool = -> Box391
FEATURE [Part::Box] Box396  label="Krychle353"
  AttacherType = Attacher::AttachEngine3D
  Height = 43
  Length = 4
  Placement = pos=(55.5,16,23) rot=(0,0,1;0rad)
  Width = 40
FEATURE [Part::Box] Box397  label="Krychle354"
  AttacherType = Attacher::AttachEngine3D
  Height = 43
  Length = 65
  Placement = pos=(-5,15.5,49.5) rot=(1,0,0;0.523599rad)
  Width = 48
FEATURE [Part::Cylinder] Cylinder112024025003003006010004245  label="Válec978"
  Angle = 360
  AttacherType = Attacher::AttachEngine3D
  FirstAngle = 0
  Height = 10
  Placement = pos=(8,64,60.5) rot=(1,0,0;1.5708rad)
  Radius = 1.65
  SecondAngle = 0
FEATURE [Part::Cylinder] Cylinder112024025003003006010004246  label="Válec979"
  Angle = 360
  AttacherType = Attacher::AttachEngine3D
  FirstAngle = 0
  Height = 20
  Placement = pos=(23.5,64,45) rot=(1,0,0;1.5708rad)
  Radius = 12.5
  SecondAngle = 0
FEATURE [Part::Box] Box398  label="Krychle355"
  AttacherType = Attacher::AttachEngine3D
  Height = 43
  Length = 59.5
  Placement = pos=(0,56,23) rot=(0,0,1;0rad)
  Width = 7
FEATURE [Part::Box] Box399  label="konektor009"
  AttacherType = Attacher::AttachEngine3D
  Height = 29
  Length = 10
  Placement = pos=(50,16,37) rot=(0,0,1;0rad)
  Width = 12
FEATURE [Part::Cylinder] Cylinder112024025003003006010004248  label="Válec981"
  Angle = 360
  AttacherType = Attacher::AttachEngine3D
  FirstAngle = 0
  Height = 6.5
  Placement = pos=(3.5,21.25,0) rot=(0,0,1;0rad)
  Radius = 3.5
  SecondAngle = 0
FEATURE [Part::Cylinder] Cylinder112024025003003006010004249  label="Válec982"
  Angle = 360
  AttacherType = Attacher::AttachEngine3D
  FirstAngle = 0
  Height = 10
  Placement = pos=(39,64,60.5) rot=(1,0,0;1.5708rad)
  Radius = 1.65
  SecondAngle = 0
FEATURE [Part::Cylinder] Cylinder112024025003003006010004250  label="Válec983"
  Angle = 360
  AttacherType = Attacher::AttachEngine3D
  FirstAngle = 0
  Height = 70
  Placement = pos=(-5,6,16.5) rot=(0,1,0;1.5708rad)
  Radius = 1
  SecondAngle = 0
FEATURE [Part::MultiFuse] Fusion005043005007002141  label="Horni diry019"
  Placement = pos=(0,0,3) rot=(0,0,1;0rad)
  Shapes = -> [Cylinder112024025003003006010004232,Cylinder112024025003003006010004250]
FEATURE [Part::MultiFuse] Fusion005043005007002147
  Shapes = -> [Fusion005043005007002138,Fusion005043005007002141]
FEATURE [Part::Cylinder] Cylinder112024025003003006010004251  label="Válec984"
  Angle = 360
  AttacherType = Attacher::AttachEngine3D
  FirstAngle = 0
  Height = 6.5
  Placement = pos=(3.5,6,0) rot=(0,0,1;0rad)
  Radius = 3.5
  SecondAngle = 0
FEATURE [Part::MultiFuse] Fusion005043005007002148  label="sloupky013"
  Placement = pos=(0,0,-3.5) rot=(0,0,1;0rad)
  Shapes = -> [Cylinder112024025003003006010004248,Cylinder112024025003003006010004251,Cylinder112024025003003006010004233,Cylinder112024025003003006010004238]
FEATURE [Part::MultiFuse] Fusion005043005007002149  label="bez der010"
  Shapes = -> [Cut018020020009027020002003004004027014020,Fusion005043005007002148]
FEATURE [Part::Box] Box400  label="Krychle356"
  AttacherType = Attacher::AttachEngine3D
  Height = 3.3
  Length = 4
  Placement = pos=(8,56,27.85) rot=(0,0,1;0rad)
  Width = 8
FEATURE [Part::Box] Box401  label="Krychle357"
  AttacherType = Attacher::AttachEngine3D
  Height = 3.3
  Length = 4
  Placement = pos=(8,56,58.85) rot=(0,0,1;0rad)
  Width = 8
FEATURE [Part::Part2DObjectPython] ShapeString032  # Draft 2D object (typed FeaturePython)
  FontFile = <path>
  Placement = pos=(15.3452,-2,30.5072) rot=(1,0,0;1.5708rad)
  Size = 4
  String = DEC
  Tracking = 0
FEATURE [Part::Extrusion] Extrude102  label="Text RA010"
  Base = -> ShapeString032
  Dir = (0,-1,0)
  DirMode = 2
  FaceMakerClass = Part::FaceMakerBullseye
  LengthFwd = 1
  LengthRev = 0
  Placement = pos=(38,1,32.5) rot=(0,1,0;3.14159rad)
  Solid = false
  Symmetric = false
FEATURE [Part::Part2DObjectPython] ShapeString033  # Draft 2D object (typed FeaturePython)
  FontFile = <path>
  Placement = pos=(15.3452,-2,30.5072) rot=(1,0,0;1.5708rad)
  Size = 0.01
  String = .
  Tracking = 0
FEATURE [Part::Cut] Cut018020020009027020002003004004027014023
  Base = -> Fusion005043005007002149
  Tool = -> Fusion005043005007002147
FEATURE [Part::Box] Box402  label="Krychle358"
  AttacherType = Attacher::AttachEngine3D
  Height = 8
  Length = 62
  Placement = pos=(-2.5,63,18.5) rot=(0,0,1;0rad)
  Width = 14
FEATURE [Part::Cylinder] Cylinder112024025003003006010004252  label="Válec985"
  Angle = 360
  AttacherType = Attacher::AttachEngine3D
  FirstAngle = 0
  Height = 20
  Placement = pos=(23.5,64,45) rot=(1,0,0;1.5708rad)
  Radius = 12.5
  SecondAngle = 0
FEATURE [Part::MultiFuse] Fusion005043005007002143
  Placement = pos=(4,0,0) rot=(0,0,1;0rad)
  Shapes = -> [Cylinder112024025003003006010004243,Cylinder112024025003003006010004245,Cylinder112024025003003006010004249,Cylinder112024025003003006010004252,Cylinder112024025003003006010004244]
FEATURE [Part::Extrusion] Extrude103  label="Text TR010"
  Base = -> ShapeString033
  Dir = (0,-1,0)
  DirMode = 2
  FaceMakerClass = Part::FaceMakerBullseye
  LengthFwd = 1
  LengthRev = 0
  Placement = pos=(-6.75,1.5,-33) rot=(0,0,1;0rad)
  Solid = false
  Symmetric = false
FEATURE [Part::MultiFuse] Fusion005043005007002137
  Shapes = -> [Extrude103,Extrude102]
FEATURE [Part::Cut] Cut018020020009027020002003004004027014019  label="PCB008"
  Base = -> Cut018020020009027020002003004004027014023
  Placement = pos=(0,-13,26) rot=(1,0,0;0rad)
  Tool = -> Fusion005043005007002137
FEATURE [Part::Cylinder] Cylinder112024025003003006010004253  label="Válec986"
  Angle = 360
  AttacherType = Attacher::AttachEngine3D
  FirstAngle = 0
  Height = 10
  Placement = pos=(52,78,22.5) rot=(1,0,0;1.5708rad)
  Radius = 1.75
  SecondAngle = 0
FEATURE [Part::Box] Box403  label="Krychle359"
  AttacherType = Attacher::AttachEngine3D
  Height = 6.4
  Length = 4
  Placement = pos=(8,60,26.3) rot=(0,0,1;0rad)
  Width = 3
FEATURE [Part::Box] Box404  label="Krychle360"
  AttacherType = Attacher::AttachEngine3D
  Height = 3.3
  Length = 4
  Placement = pos=(39,56,58.85) rot=(0,0,1;0rad)
  Width = 8
FEATURE [Part::Cylinder] Cylinder112024025003003006010004254  label="Válec987"
  Angle = 360
  AttacherType = Attacher::AttachEngine3D
  FirstAngle = 0
  Height = 10
  Placement = pos=(39,64,29.5) rot=(1,0,0;1.5708rad)
  Radius = 1.65
  SecondAngle = 0
FEATURE [Part::Cylinder] Cylinder112024025003003006010004255  label="Válec988"
  Angle = 360
  AttacherType = Attacher::AttachEngine3D
  FirstAngle = 0
  Height = 10
  Placement = pos=(55,60,58) rot=(0,0,1;0rad)
  Radius = 0.8
  SecondAngle = 0
FEATURE [Part::Cylinder] Cylinder112024025003003006010004256  label="Válec989"
  Angle = 360
  AttacherType = Attacher::AttachEngine3D
  FirstAngle = 0
  Height = 3
  Placement = pos=(8,63,29.5) rot=(1,0,0;1.5708rad)
  Radius = 3.2
  SecondAngle = 0
FEATURE [Part::MultiFuse] Fusion005043005007002142  label="Imbus027"
  Shapes = -> [Cylinder112024025003003006010004237,Cylinder112024025003003006010004256,Box403]
FEATURE [Part::MultiFuse] Fusion005043005007002150  label="diry035"
  Placement = pos=(0,0,0.5) rot=(0,0,1;0rad)
  Shapes = -> [Cylinder112024025003003006010004239,Cylinder112024025003003006010004246,Cylinder112024025003003006010004240,Cylinder112024025003003006010004254,Cylinder112024025003003006010004242,Screw036,Fusion005043005007002143,Box393,Box400,Box404,Box394,Box401,Box399,Box397,Fusion005043005007002142,Fusion005043005007002134,Fusion005043005007002133,Fusion005043005007002135]
FEATURE [Part::Cylinder] Cylinder112024025003003006010004257  label="Válec990"
  Angle = 360
  AttacherType = Attacher::AttachEngine3D
  FirstAngle = 0
  Height = 10
  Placement = pos=(3,60,58) rot=(0,0,1;0rad)
  Radius = 0.8
  SecondAngle = 0
FEATURE [Part::Box] Box405  label="Krychle361"
  AttacherType = Attacher::AttachEngine3D
  Height = 43
  Length = 2.5
  Placement = pos=(-2.5,16,23) rot=(0,0,1;0rad)
  Width = 47
FEATURE [Part::MultiFuse] Fusion005043005007002144  label="Main011"
  Placement = pos=(0,0,0.5) rot=(0,0,1;0rad)
  Shapes = -> [Box398,Box396,Box405]
FEATURE [Part::Cut] Cut018020020009027020002003004004027014017  label="DE005"
  Base = -> Fusion005043005007002144
  Tool = -> Fusion005043005007002150
FEATURE [Part::MultiFuse] Fusion005043005007002146  label="DECV004"
  Shapes = -> [Cut018020020009027020002003004004027014019,Cut018020020009027020002003004004027014017,Cut018020020009027020002003004004027014018]
FEATURE [Part::Cylinder] Cylinder112024025003003006010004258  label="Válec991"
  Angle = 360
  AttacherType = Attacher::AttachEngine3D
  FirstAngle = 0
  Height = 10
  Placement = pos=(4,78,22.5) rot=(1,0,0;1.5708rad)
  Radius = 1.75
  SecondAngle = 0
FEATURE [Part::Box] Box406  label="Krychle362"
  AttacherType = Attacher::AttachEngine3D
  Height = 12
  Length = 62
  Placement = pos=(-2.5,-15,44) rot=(0,0,1;0rad)
  Width = 31
FEATURE [Part::Box] Box407  label="Krychle363"
  AttacherType = Attacher::AttachEngine3D
  Height = 12
  Length = 58
  Placement = pos=(-0.5,-13,44) rot=(0,0,1;0rad)
  Width = 29
FEATURE [Part::Cylinder] Cylinder112024025003003006010004259  label="Válec992"
  Angle = 360
  AttacherType = Attacher::AttachEngine3D
  FirstAngle = 0
  Height = 70
  Placement = pos=(-8,7,52.5) rot=(0,1,0;1.5708rad)
  Radius = 0.75
  SecondAngle = 0
FEATURE [Part::Cylinder] Cylinder112024025003003006010004260  label="Válec993"
  Angle = 360
  AttacherType = Attacher::AttachEngine3D
  FirstAngle = 0
  Height = 70
  Placement = pos=(-8,-7,52.5) rot=(0,1,0;1.5708rad)
  Radius = 0.75
  SecondAngle = 0
FEATURE [Part::MultiFuse] Fusion005043005007002139  label="dirky kryt007"
  Shapes = -> [Cylinder112024025003003006010004257,Cylinder112024025003003006010004255,Cylinder112024025003003006010004253,Cylinder112024025003003006010004258,Box407,Cut018020020009027020002003004004027014021,Cylinder112024025003003006010004259,Cylinder112024025003003006010004260]
FEATURE [Part::MultiFuse] Fusion005043005007002151  label="dec001"
  Shapes = -> [Fusion005043005007002146,Box402,Box406]
FEATURE [Part::Cut] Cut018020020009027020002003004004027014022  label="Dec-red001"
  Base = -> Fusion005043005007002151
  Tool = -> Fusion005043005007002139
FEATURE [Part::Fillet] Fillet004005003002003002003004002002002003002002002  label="DEv6"
  Base = -> Cut018020020009027020002003004004027014022
  Edges = 10 edges r=2: [Edge6,Edge27,Edge30,Edge37,Edge39,Edge43,Edge93,Edge103,Edge153,Edge237]
FEATURE [Part::Feature] Fillet004005003002003002003004002002002003002002002001  label="DEv004"
  shape: bbox 62 x 92 x 55.5 mm, 184 faces (baked)
FEATURE [Part::Feature] Fillet004005003002003002003004002002002003002002002002  label="RAv062"
  shape: bbox 62 x 92 x 55 mm, 181 faces (baked)
FEATURE [Part::Box] Box408  label="Krychle364"
  AttacherType = Attacher::AttachEngine3D
  Height = 8
  Length = 2
  Placement = pos=(-1,-20,0) rot=(0,0,1;0rad)
  Width = 40
FEATURE [Part::Box] Box409  label="Krychle365"
  AttacherType = Attacher::AttachEngine3D
  Height = 4
  Length = 6
  Placement = pos=(22,-7,12) rot=(0,0,1;0rad)
  Width = 14
FEATURE [Part::Cylinder] Cylinder112024025003003006010004261  label="Válec994"
  Angle = 360
  AttacherType = Attacher::AttachEngine3D
  FirstAngle = 0
  Height = 14
  Placement = pos=(0,0,8) rot=(0,0,1;0rad)
  Radius = 22
  SecondAngle = 0
FEATURE [Part::Cylinder] Cylinder112024025003003006010004262  label="Válec995"
  Angle = 360
  AttacherType = Attacher::AttachEngine3D
  FirstAngle = 0
  Height = 11
  Placement = pos=(25,4,12) rot=(0,0,1;0rad)
  Radius = 1
  SecondAngle = 0
FEATURE [Part::Box] Box410  label="Krychle366"
  AttacherType = Attacher::AttachEngine3D
  Height = 8
  Length = 40
  Placement = pos=(-20,-1,0) rot=(0,0,1;0rad)
  Width = 2
FEATURE [Part::Cylinder] Cylinder112024025003003006010004263  label="Válec996"
  Angle = 360
  AttacherType = Attacher::AttachEngine3D
  FirstAngle = 0
  Height = 25
  Radius = 16
  SecondAngle = 0
FEATURE [Part::Cylinder] Cylinder112024025003003006010004264  label="Válec997"
  Angle = 360
  AttacherType = Attacher::AttachEngine3D
  FirstAngle = 0
  Height = 22
  Radius = 17.6
  SecondAngle = 0
FEATURE [Part::Cylinder] Cylinder112024025003003006010004265  label="Válec998"
  Angle = 360
  AttacherType = Attacher::AttachEngine3D
  FirstAngle = 0
  Height = 8
  Placement = pos=(0,0,14) rot=(0,0,1;0rad)
  Radius = 17.8
  SecondAngle = 0
FEATURE [Part::Cylinder] Cylinder112024025003003006010004266  label="Válec999"
  Angle = 360
  AttacherType = Attacher::AttachEngine3D
  FirstAngle = 0
  Height = 13
  Placement = pos=(15,0,12) rot=(0,1,0;1.5708rad)
  Radius = 1.8
  SecondAngle = 0
FEATURE [Part::Cylinder] Cylinder112024025003003006010004267  label="Válec1000"
  Angle = 360
  AttacherType = Attacher::AttachEngine3D
  FirstAngle = 0
  Height = 11
  Placement = pos=(25,-4,12) rot=(0,0,1;0rad)
  Radius = 1
  SecondAngle = 0
FEATURE [Part::Box] Box411  label="Krychle367"
  AttacherType = Attacher::AttachEngine3D
  Height = 8
  Length = 10
  Placement = pos=(18,-7,8) rot=(0,0,1;0rad)
  Width = 14
FEATURE [Part::MultiFuse] Fusion005043005007002153  label="telo001"
  Shapes = -> [Cylinder112024025003003006010004264,Cylinder112024025003003006010004261,Box411]
FEATURE [Part::Cylinder] Cylinder112024025003003006010004268  label="Válec1001"
  Angle = 360
  AttacherType = Attacher::AttachEngine3D
  FirstAngle = 0
  Height = 13
  Placement = pos=(9,0,11.5) rot=(0,1,0;1.5708rad)
  Radius = 2.2
  SecondAngle = 0
FEATURE [Part::MultiFuse] Fusion005043005007002152  label="diry036"
  Shapes = -> [Cylinder112024025003003006010004265,Cylinder112024025003003006010004263,Cylinder112024025003003006010004266,Box408,Box410,Cylinder112024025003003006010004262,Cylinder112024025003003006010004267,Box409,Cylinder112024025003003006010004268]
FEATURE [Part::Cut] Cut018020020009027020002003004004027014024  label="Polar scope Iluminator001"
  Base = -> Fusion005043005007002153
  Tool = -> Fusion005043005007002152
FEATURE [Part::Cylinder] Cylinder112024025003003006010004269  label="Válec1002"
  Angle = 360
  AttacherType = Attacher::AttachEngine3D
  FirstAngle = 0
  Height = 16
  Placement = pos=(0,0,8) rot=(0,0,1;0rad)
  Radius = 32
  SecondAngle = 0
FEATURE [Part::Cut] Cut018020020009027020002003004004027014025
  Base = -> Cut018020020009027020002003004004027014024
  Tool = -> Cylinder112024025003003006010004269
FEATURE [Part::Cylinder] Cylinder112024025003003006010004270  label="Válec1003"
  Angle = 360
  AttacherType = Attacher::AttachEngine3D
  FirstAngle = 0
  Height = 2
  Radius = 21
  SecondAngle = 0
FEATURE [Part::MultiFuse] Fusion005043005007002154
  Shapes = -> [Cut018020020009027020002003004004027014025,Cylinder112024025003003006010004270]
FEATURE [Part::Fillet] Fillet004005003002003002003004002002002003002002002003
  Base = -> Fusion005043005007002154
  Edges = 1 edges r=1: [Edge3]
note: 22 file-system paths scrubbed to <path> (originals preserved in the JSON sidecar)
